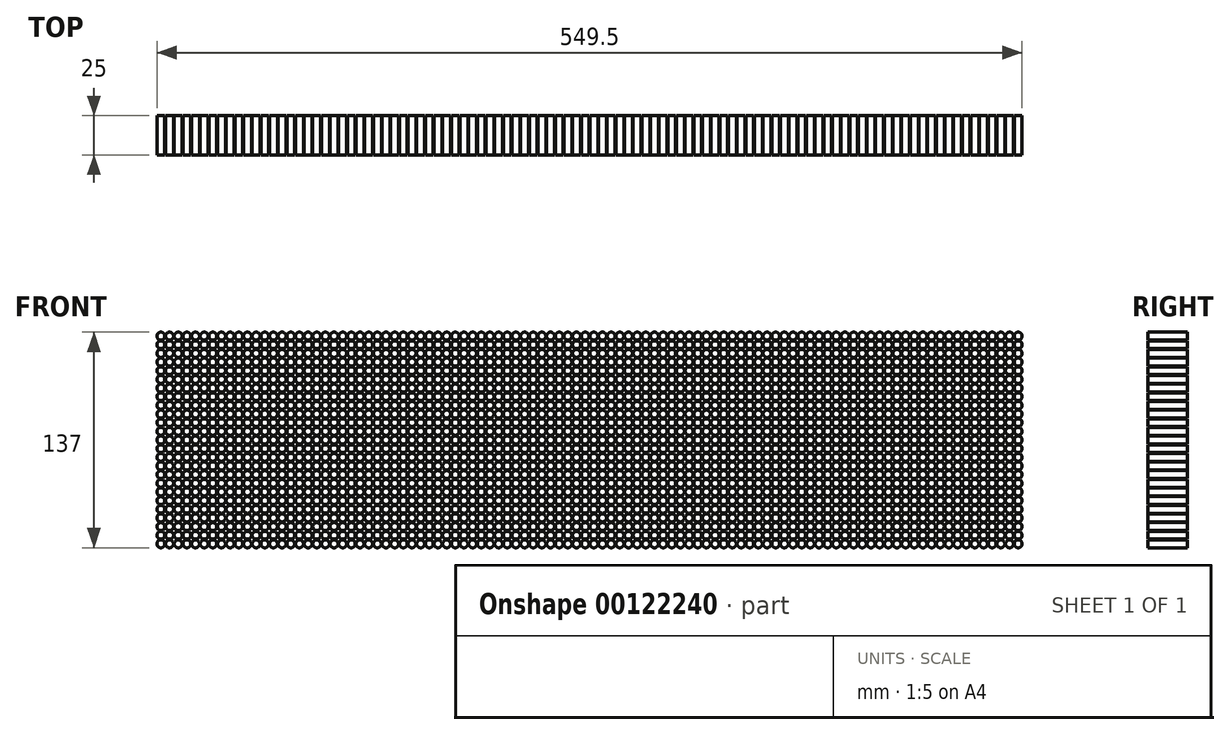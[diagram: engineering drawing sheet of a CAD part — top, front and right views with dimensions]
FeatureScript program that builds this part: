
annotation { "Feature Type Name" : "Feature", "Feature Type Description" : "" }
export const myFeature = defineFeature(function(context is Context, id is Id, definition is map)
    precondition{}
    {
        {
            var Q0;
            Q0=qCreatedBy(makeId("Front.planeOp"),FACE);
            var sketch = newSketch(context, id + "F0", { "sketchPlane" : qUnion([Q0])});
            skCircle(sketch, "E0", {"center": v(0, 0) * mm, "radius": 2.5 * mm});
            skCircle(sketch, "E1.0.1.0", {"center": v(0, -5.5) * mm, "radius": 2.5 * mm});
            skCircle(sketch, "E1.0.2.0", {"center": v(0, -11) * mm, "radius": 2.5 * mm});
            skCircle(sketch, "E1.0.3.0", {"center": v(0, -16.5) * mm, "radius": 2.5 * mm});
            skCircle(sketch, "E1.0.4.0", {"center": v(0, -22) * mm, "radius": 2.5 * mm});
            skCircle(sketch, "E1.0.5.0", {"center": v(0, -27.5) * mm, "radius": 2.5 * mm});
            skCircle(sketch, "E1.0.6.0", {"center": v(0, -33) * mm, "radius": 2.5 * mm});
            skCircle(sketch, "E1.0.7.0", {"center": v(0, -38.5) * mm, "radius": 2.5 * mm});
            skCircle(sketch, "E1.0.8.0", {"center": v(0, -44) * mm, "radius": 2.5 * mm});
            skCircle(sketch, "E1.0.9.0", {"center": v(0, -49.5) * mm, "radius": 2.5 * mm});
            skCircle(sketch, "E1.0.10.0", {"center": v(0, -55) * mm, "radius": 2.5 * mm});
            skCircle(sketch, "E1.0.11.0", {"center": v(0, -60.5) * mm, "radius": 2.5 * mm});
            skCircle(sketch, "E1.0.12.0", {"center": v(0, -66) * mm, "radius": 2.5 * mm});
            skCircle(sketch, "E1.0.13.0", {"center": v(0, -71.5) * mm, "radius": 2.5 * mm});
            skCircle(sketch, "E1.0.14.0", {"center": v(0, -77) * mm, "radius": 2.5 * mm});
            skCircle(sketch, "E1.0.15.0", {"center": v(0, -82.5) * mm, "radius": 2.5 * mm});
            skCircle(sketch, "E1.0.16.0", {"center": v(0, -88) * mm, "radius": 2.5 * mm});
            skCircle(sketch, "E1.0.17.0", {"center": v(0, -93.5) * mm, "radius": 2.5 * mm});
            skCircle(sketch, "E1.0.18.0", {"center": v(0, -99) * mm, "radius": 2.5 * mm});
            skCircle(sketch, "E1.0.19.0", {"center": v(0, -104.5) * mm, "radius": 2.5 * mm});
            skCircle(sketch, "E1.0.20.0", {"center": v(0, -110) * mm, "radius": 2.5 * mm});
            skCircle(sketch, "E1.0.21.0", {"center": v(0, -115.5) * mm, "radius": 2.5 * mm});
            skCircle(sketch, "E1.0.22.0", {"center": v(0, -121) * mm, "radius": 2.5 * mm});
            skCircle(sketch, "E1.0.23.0", {"center": v(0, -126.5) * mm, "radius": 2.5 * mm});
            skCircle(sketch, "E1.0.24.0", {"center": v(0, -132) * mm, "radius": 2.5 * mm});
            skCircle(sketch, "E1.1.0.0", {"center": v(5.5, 0) * mm, "radius": 2.5 * mm});
            skCircle(sketch, "E1.1.1.0", {"center": v(5.5, -5.5) * mm, "radius": 2.5 * mm});
            skCircle(sketch, "E1.1.2.0", {"center": v(5.5, -11) * mm, "radius": 2.5 * mm});
            skCircle(sketch, "E1.1.3.0", {"center": v(5.5, -16.5) * mm, "radius": 2.5 * mm});
            skCircle(sketch, "E1.1.4.0", {"center": v(5.5, -22) * mm, "radius": 2.5 * mm});
            skCircle(sketch, "E1.1.5.0", {"center": v(5.5, -27.5) * mm, "radius": 2.5 * mm});
            skCircle(sketch, "E1.1.6.0", {"center": v(5.5, -33) * mm, "radius": 2.5 * mm});
            skCircle(sketch, "E1.1.7.0", {"center": v(5.5, -38.5) * mm, "radius": 2.5 * mm});
            skCircle(sketch, "E1.1.8.0", {"center": v(5.5, -44) * mm, "radius": 2.5 * mm});
            skCircle(sketch, "E1.1.9.0", {"center": v(5.5, -49.5) * mm, "radius": 2.5 * mm});
            skCircle(sketch, "E1.1.10.0", {"center": v(5.5, -55) * mm, "radius": 2.5 * mm});
            skCircle(sketch, "E1.1.11.0", {"center": v(5.5, -60.5) * mm, "radius": 2.5 * mm});
            skCircle(sketch, "E1.1.12.0", {"center": v(5.5, -66) * mm, "radius": 2.5 * mm});
            skCircle(sketch, "E1.1.13.0", {"center": v(5.5, -71.5) * mm, "radius": 2.5 * mm});
            skCircle(sketch, "E1.1.14.0", {"center": v(5.5, -77) * mm, "radius": 2.5 * mm});
            skCircle(sketch, "E1.1.15.0", {"center": v(5.5, -82.5) * mm, "radius": 2.5 * mm});
            skCircle(sketch, "E1.1.16.0", {"center": v(5.5, -88) * mm, "radius": 2.5 * mm});
            skCircle(sketch, "E1.1.17.0", {"center": v(5.5, -93.5) * mm, "radius": 2.5 * mm});
            skCircle(sketch, "E1.1.18.0", {"center": v(5.5, -99) * mm, "radius": 2.5 * mm});
            skCircle(sketch, "E1.1.19.0", {"center": v(5.5, -104.5) * mm, "radius": 2.5 * mm});
            skCircle(sketch, "E1.1.20.0", {"center": v(5.5, -110) * mm, "radius": 2.5 * mm});
            skCircle(sketch, "E1.1.21.0", {"center": v(5.5, -115.5) * mm, "radius": 2.5 * mm});
            skCircle(sketch, "E1.1.22.0", {"center": v(5.5, -121) * mm, "radius": 2.5 * mm});
            skCircle(sketch, "E1.1.23.0", {"center": v(5.5, -126.5) * mm, "radius": 2.5 * mm});
            skCircle(sketch, "E1.1.24.0", {"center": v(5.5, -132) * mm, "radius": 2.5 * mm});
            skCircle(sketch, "E1.2.0.0", {"center": v(11, 0) * mm, "radius": 2.5 * mm});
            skCircle(sketch, "E1.2.1.0", {"center": v(11, -5.5) * mm, "radius": 2.5 * mm});
            skCircle(sketch, "E1.2.2.0", {"center": v(11, -11) * mm, "radius": 2.5 * mm});
            skCircle(sketch, "E1.2.3.0", {"center": v(11, -16.5) * mm, "radius": 2.5 * mm});
            skCircle(sketch, "E1.2.4.0", {"center": v(11, -22) * mm, "radius": 2.5 * mm});
            skCircle(sketch, "E1.2.5.0", {"center": v(11, -27.5) * mm, "radius": 2.5 * mm});
            skCircle(sketch, "E1.2.6.0", {"center": v(11, -33) * mm, "radius": 2.5 * mm});
            skCircle(sketch, "E1.2.7.0", {"center": v(11, -38.5) * mm, "radius": 2.5 * mm});
            skCircle(sketch, "E1.2.8.0", {"center": v(11, -44) * mm, "radius": 2.5 * mm});
            skCircle(sketch, "E1.2.9.0", {"center": v(11, -49.5) * mm, "radius": 2.5 * mm});
            skCircle(sketch, "E1.2.10.0", {"center": v(11, -55) * mm, "radius": 2.5 * mm});
            skCircle(sketch, "E1.2.11.0", {"center": v(11, -60.5) * mm, "radius": 2.5 * mm});
            skCircle(sketch, "E1.2.12.0", {"center": v(11, -66) * mm, "radius": 2.5 * mm});
            skCircle(sketch, "E1.2.13.0", {"center": v(11, -71.5) * mm, "radius": 2.5 * mm});
            skCircle(sketch, "E1.2.14.0", {"center": v(11, -77) * mm, "radius": 2.5 * mm});
            skCircle(sketch, "E1.2.15.0", {"center": v(11, -82.5) * mm, "radius": 2.5 * mm});
            skCircle(sketch, "E1.2.16.0", {"center": v(11, -88) * mm, "radius": 2.5 * mm});
            skCircle(sketch, "E1.2.17.0", {"center": v(11, -93.5) * mm, "radius": 2.5 * mm});
            skCircle(sketch, "E1.2.18.0", {"center": v(11, -99) * mm, "radius": 2.5 * mm});
            skCircle(sketch, "E1.2.19.0", {"center": v(11, -104.5) * mm, "radius": 2.5 * mm});
            skCircle(sketch, "E1.2.20.0", {"center": v(11, -110) * mm, "radius": 2.5 * mm});
            skCircle(sketch, "E1.2.21.0", {"center": v(11, -115.5) * mm, "radius": 2.5 * mm});
            skCircle(sketch, "E1.2.22.0", {"center": v(11, -121) * mm, "radius": 2.5 * mm});
            skCircle(sketch, "E1.2.23.0", {"center": v(11, -126.5) * mm, "radius": 2.5 * mm});
            skCircle(sketch, "E1.2.24.0", {"center": v(11, -132) * mm, "radius": 2.5 * mm});
            skCircle(sketch, "E1.3.0.0", {"center": v(16.5, 0) * mm, "radius": 2.5 * mm});
            skCircle(sketch, "E1.3.1.0", {"center": v(16.5, -5.5) * mm, "radius": 2.5 * mm});
            skCircle(sketch, "E1.3.2.0", {"center": v(16.5, -11) * mm, "radius": 2.5 * mm});
            skCircle(sketch, "E1.3.3.0", {"center": v(16.5, -16.5) * mm, "radius": 2.5 * mm});
            skCircle(sketch, "E1.3.4.0", {"center": v(16.5, -22) * mm, "radius": 2.5 * mm});
            skCircle(sketch, "E1.3.5.0", {"center": v(16.5, -27.5) * mm, "radius": 2.5 * mm});
            skCircle(sketch, "E1.3.6.0", {"center": v(16.5, -33) * mm, "radius": 2.5 * mm});
            skCircle(sketch, "E1.3.7.0", {"center": v(16.5, -38.5) * mm, "radius": 2.5 * mm});
            skCircle(sketch, "E1.3.8.0", {"center": v(16.5, -44) * mm, "radius": 2.5 * mm});
            skCircle(sketch, "E1.3.9.0", {"center": v(16.5, -49.5) * mm, "radius": 2.5 * mm});
            skCircle(sketch, "E1.3.10.0", {"center": v(16.5, -55) * mm, "radius": 2.5 * mm});
            skCircle(sketch, "E1.3.11.0", {"center": v(16.5, -60.5) * mm, "radius": 2.5 * mm});
            skCircle(sketch, "E1.3.12.0", {"center": v(16.5, -66) * mm, "radius": 2.5 * mm});
            skCircle(sketch, "E1.3.13.0", {"center": v(16.5, -71.5) * mm, "radius": 2.5 * mm});
            skCircle(sketch, "E1.3.14.0", {"center": v(16.5, -77) * mm, "radius": 2.5 * mm});
            skCircle(sketch, "E1.3.15.0", {"center": v(16.5, -82.5) * mm, "radius": 2.5 * mm});
            skCircle(sketch, "E1.3.16.0", {"center": v(16.5, -88) * mm, "radius": 2.5 * mm});
            skCircle(sketch, "E1.3.17.0", {"center": v(16.5, -93.5) * mm, "radius": 2.5 * mm});
            skCircle(sketch, "E1.3.18.0", {"center": v(16.5, -99) * mm, "radius": 2.5 * mm});
            skCircle(sketch, "E1.3.19.0", {"center": v(16.5, -104.5) * mm, "radius": 2.5 * mm});
            skCircle(sketch, "E1.3.20.0", {"center": v(16.5, -110) * mm, "radius": 2.5 * mm});
            skCircle(sketch, "E1.3.21.0", {"center": v(16.5, -115.5) * mm, "radius": 2.5 * mm});
            skCircle(sketch, "E1.3.22.0", {"center": v(16.5, -121) * mm, "radius": 2.5 * mm});
            skCircle(sketch, "E1.3.23.0", {"center": v(16.5, -126.5) * mm, "radius": 2.5 * mm});
            skCircle(sketch, "E1.3.24.0", {"center": v(16.5, -132) * mm, "radius": 2.5 * mm});
            skCircle(sketch, "E1.4.0.0", {"center": v(22, 0) * mm, "radius": 2.5 * mm});
            skCircle(sketch, "E1.4.1.0", {"center": v(22, -5.5) * mm, "radius": 2.5 * mm});
            skCircle(sketch, "E1.4.2.0", {"center": v(22, -11) * mm, "radius": 2.5 * mm});
            skCircle(sketch, "E1.4.3.0", {"center": v(22, -16.5) * mm, "radius": 2.5 * mm});
            skCircle(sketch, "E1.4.4.0", {"center": v(22, -22) * mm, "radius": 2.5 * mm});
            skCircle(sketch, "E1.4.5.0", {"center": v(22, -27.5) * mm, "radius": 2.5 * mm});
            skCircle(sketch, "E1.4.6.0", {"center": v(22, -33) * mm, "radius": 2.5 * mm});
            skCircle(sketch, "E1.4.7.0", {"center": v(22, -38.5) * mm, "radius": 2.5 * mm});
            skCircle(sketch, "E1.4.8.0", {"center": v(22, -44) * mm, "radius": 2.5 * mm});
            skCircle(sketch, "E1.4.9.0", {"center": v(22, -49.5) * mm, "radius": 2.5 * mm});
            skCircle(sketch, "E1.4.10.0", {"center": v(22, -55) * mm, "radius": 2.5 * mm});
            skCircle(sketch, "E1.4.11.0", {"center": v(22, -60.5) * mm, "radius": 2.5 * mm});
            skCircle(sketch, "E1.4.12.0", {"center": v(22, -66) * mm, "radius": 2.5 * mm});
            skCircle(sketch, "E1.4.13.0", {"center": v(22, -71.5) * mm, "radius": 2.5 * mm});
            skCircle(sketch, "E1.4.14.0", {"center": v(22, -77) * mm, "radius": 2.5 * mm});
            skCircle(sketch, "E1.4.15.0", {"center": v(22, -82.5) * mm, "radius": 2.5 * mm});
            skCircle(sketch, "E1.4.16.0", {"center": v(22, -88) * mm, "radius": 2.5 * mm});
            skCircle(sketch, "E1.4.17.0", {"center": v(22, -93.5) * mm, "radius": 2.5 * mm});
            skCircle(sketch, "E1.4.18.0", {"center": v(22, -99) * mm, "radius": 2.5 * mm});
            skCircle(sketch, "E1.4.19.0", {"center": v(22, -104.5) * mm, "radius": 2.5 * mm});
            skCircle(sketch, "E1.4.20.0", {"center": v(22, -110) * mm, "radius": 2.5 * mm});
            skCircle(sketch, "E1.4.21.0", {"center": v(22, -115.5) * mm, "radius": 2.5 * mm});
            skCircle(sketch, "E1.4.22.0", {"center": v(22, -121) * mm, "radius": 2.5 * mm});
            skCircle(sketch, "E1.4.23.0", {"center": v(22, -126.5) * mm, "radius": 2.5 * mm});
            skCircle(sketch, "E1.4.24.0", {"center": v(22, -132) * mm, "radius": 2.5 * mm});
            skCircle(sketch, "E1.5.0.0", {"center": v(27.5, 0) * mm, "radius": 2.5 * mm});
            skCircle(sketch, "E1.5.1.0", {"center": v(27.5, -5.5) * mm, "radius": 2.5 * mm});
            skCircle(sketch, "E1.5.2.0", {"center": v(27.5, -11) * mm, "radius": 2.5 * mm});
            skCircle(sketch, "E1.5.3.0", {"center": v(27.5, -16.5) * mm, "radius": 2.5 * mm});
            skCircle(sketch, "E1.5.4.0", {"center": v(27.5, -22) * mm, "radius": 2.5 * mm});
            skCircle(sketch, "E1.5.5.0", {"center": v(27.5, -27.5) * mm, "radius": 2.5 * mm});
            skCircle(sketch, "E1.5.6.0", {"center": v(27.5, -33) * mm, "radius": 2.5 * mm});
            skCircle(sketch, "E1.5.7.0", {"center": v(27.5, -38.5) * mm, "radius": 2.5 * mm});
            skCircle(sketch, "E1.5.8.0", {"center": v(27.5, -44) * mm, "radius": 2.5 * mm});
            skCircle(sketch, "E1.5.9.0", {"center": v(27.5, -49.5) * mm, "radius": 2.5 * mm});
            skCircle(sketch, "E1.5.10.0", {"center": v(27.5, -55) * mm, "radius": 2.5 * mm});
            skCircle(sketch, "E1.5.11.0", {"center": v(27.5, -60.5) * mm, "radius": 2.5 * mm});
            skCircle(sketch, "E1.5.12.0", {"center": v(27.5, -66) * mm, "radius": 2.5 * mm});
            skCircle(sketch, "E1.5.13.0", {"center": v(27.5, -71.5) * mm, "radius": 2.5 * mm});
            skCircle(sketch, "E1.5.14.0", {"center": v(27.5, -77) * mm, "radius": 2.5 * mm});
            skCircle(sketch, "E1.5.15.0", {"center": v(27.5, -82.5) * mm, "radius": 2.5 * mm});
            skCircle(sketch, "E1.5.16.0", {"center": v(27.5, -88) * mm, "radius": 2.5 * mm});
            skCircle(sketch, "E1.5.17.0", {"center": v(27.5, -93.5) * mm, "radius": 2.5 * mm});
            skCircle(sketch, "E1.5.18.0", {"center": v(27.5, -99) * mm, "radius": 2.5 * mm});
            skCircle(sketch, "E1.5.19.0", {"center": v(27.5, -104.5) * mm, "radius": 2.5 * mm});
            skCircle(sketch, "E1.5.20.0", {"center": v(27.5, -110) * mm, "radius": 2.5 * mm});
            skCircle(sketch, "E1.5.21.0", {"center": v(27.5, -115.5) * mm, "radius": 2.5 * mm});
            skCircle(sketch, "E1.5.22.0", {"center": v(27.5, -121) * mm, "radius": 2.5 * mm});
            skCircle(sketch, "E1.5.23.0", {"center": v(27.5, -126.5) * mm, "radius": 2.5 * mm});
            skCircle(sketch, "E1.5.24.0", {"center": v(27.5, -132) * mm, "radius": 2.5 * mm});
            skCircle(sketch, "E1.6.0.0", {"center": v(33, 0) * mm, "radius": 2.5 * mm});
            skCircle(sketch, "E1.6.1.0", {"center": v(33, -5.5) * mm, "radius": 2.5 * mm});
            skCircle(sketch, "E1.6.2.0", {"center": v(33, -11) * mm, "radius": 2.5 * mm});
            skCircle(sketch, "E1.6.3.0", {"center": v(33, -16.5) * mm, "radius": 2.5 * mm});
            skCircle(sketch, "E1.6.4.0", {"center": v(33, -22) * mm, "radius": 2.5 * mm});
            skCircle(sketch, "E1.6.5.0", {"center": v(33, -27.5) * mm, "radius": 2.5 * mm});
            skCircle(sketch, "E1.6.6.0", {"center": v(33, -33) * mm, "radius": 2.5 * mm});
            skCircle(sketch, "E1.6.7.0", {"center": v(33, -38.5) * mm, "radius": 2.5 * mm});
            skCircle(sketch, "E1.6.8.0", {"center": v(33, -44) * mm, "radius": 2.5 * mm});
            skCircle(sketch, "E1.6.9.0", {"center": v(33, -49.5) * mm, "radius": 2.5 * mm});
            skCircle(sketch, "E1.6.10.0", {"center": v(33, -55) * mm, "radius": 2.5 * mm});
            skCircle(sketch, "E1.6.11.0", {"center": v(33, -60.5) * mm, "radius": 2.5 * mm});
            skCircle(sketch, "E1.6.12.0", {"center": v(33, -66) * mm, "radius": 2.5 * mm});
            skCircle(sketch, "E1.6.13.0", {"center": v(33, -71.5) * mm, "radius": 2.5 * mm});
            skCircle(sketch, "E1.6.14.0", {"center": v(33, -77) * mm, "radius": 2.5 * mm});
            skCircle(sketch, "E1.6.15.0", {"center": v(33, -82.5) * mm, "radius": 2.5 * mm});
            skCircle(sketch, "E1.6.16.0", {"center": v(33, -88) * mm, "radius": 2.5 * mm});
            skCircle(sketch, "E1.6.17.0", {"center": v(33, -93.5) * mm, "radius": 2.5 * mm});
            skCircle(sketch, "E1.6.18.0", {"center": v(33, -99) * mm, "radius": 2.5 * mm});
            skCircle(sketch, "E1.6.19.0", {"center": v(33, -104.5) * mm, "radius": 2.5 * mm});
            skCircle(sketch, "E1.6.20.0", {"center": v(33, -110) * mm, "radius": 2.5 * mm});
            skCircle(sketch, "E1.6.21.0", {"center": v(33, -115.5) * mm, "radius": 2.5 * mm});
            skCircle(sketch, "E1.6.22.0", {"center": v(33, -121) * mm, "radius": 2.5 * mm});
            skCircle(sketch, "E1.6.23.0", {"center": v(33, -126.5) * mm, "radius": 2.5 * mm});
            skCircle(sketch, "E1.6.24.0", {"center": v(33, -132) * mm, "radius": 2.5 * mm});
            skCircle(sketch, "E1.7.0.0", {"center": v(38.5, 0) * mm, "radius": 2.5 * mm});
            skCircle(sketch, "E1.7.1.0", {"center": v(38.5, -5.5) * mm, "radius": 2.5 * mm});
            skCircle(sketch, "E1.7.2.0", {"center": v(38.5, -11) * mm, "radius": 2.5 * mm});
            skCircle(sketch, "E1.7.3.0", {"center": v(38.5, -16.5) * mm, "radius": 2.5 * mm});
            skCircle(sketch, "E1.7.4.0", {"center": v(38.5, -22) * mm, "radius": 2.5 * mm});
            skCircle(sketch, "E1.7.5.0", {"center": v(38.5, -27.5) * mm, "radius": 2.5 * mm});
            skCircle(sketch, "E1.7.6.0", {"center": v(38.5, -33) * mm, "radius": 2.5 * mm});
            skCircle(sketch, "E1.7.7.0", {"center": v(38.5, -38.5) * mm, "radius": 2.5 * mm});
            skCircle(sketch, "E1.7.8.0", {"center": v(38.5, -44) * mm, "radius": 2.5 * mm});
            skCircle(sketch, "E1.7.9.0", {"center": v(38.5, -49.5) * mm, "radius": 2.5 * mm});
            skCircle(sketch, "E1.7.10.0", {"center": v(38.5, -55) * mm, "radius": 2.5 * mm});
            skCircle(sketch, "E1.7.11.0", {"center": v(38.5, -60.5) * mm, "radius": 2.5 * mm});
            skCircle(sketch, "E1.7.12.0", {"center": v(38.5, -66) * mm, "radius": 2.5 * mm});
            skCircle(sketch, "E1.7.13.0", {"center": v(38.5, -71.5) * mm, "radius": 2.5 * mm});
            skCircle(sketch, "E1.7.14.0", {"center": v(38.5, -77) * mm, "radius": 2.5 * mm});
            skCircle(sketch, "E1.7.15.0", {"center": v(38.5, -82.5) * mm, "radius": 2.5 * mm});
            skCircle(sketch, "E1.7.16.0", {"center": v(38.5, -88) * mm, "radius": 2.5 * mm});
            skCircle(sketch, "E1.7.17.0", {"center": v(38.5, -93.5) * mm, "radius": 2.5 * mm});
            skCircle(sketch, "E1.7.18.0", {"center": v(38.5, -99) * mm, "radius": 2.5 * mm});
            skCircle(sketch, "E1.7.19.0", {"center": v(38.5, -104.5) * mm, "radius": 2.5 * mm});
            skCircle(sketch, "E1.7.20.0", {"center": v(38.5, -110) * mm, "radius": 2.5 * mm});
            skCircle(sketch, "E1.7.21.0", {"center": v(38.5, -115.5) * mm, "radius": 2.5 * mm});
            skCircle(sketch, "E1.7.22.0", {"center": v(38.5, -121) * mm, "radius": 2.5 * mm});
            skCircle(sketch, "E1.7.23.0", {"center": v(38.5, -126.5) * mm, "radius": 2.5 * mm});
            skCircle(sketch, "E1.7.24.0", {"center": v(38.5, -132) * mm, "radius": 2.5 * mm});
            skCircle(sketch, "E1.8.0.0", {"center": v(44, 0) * mm, "radius": 2.5 * mm});
            skCircle(sketch, "E1.8.1.0", {"center": v(44, -5.5) * mm, "radius": 2.5 * mm});
            skCircle(sketch, "E1.8.2.0", {"center": v(44, -11) * mm, "radius": 2.5 * mm});
            skCircle(sketch, "E1.8.3.0", {"center": v(44, -16.5) * mm, "radius": 2.5 * mm});
            skCircle(sketch, "E1.8.4.0", {"center": v(44, -22) * mm, "radius": 2.5 * mm});
            skCircle(sketch, "E1.8.5.0", {"center": v(44, -27.5) * mm, "radius": 2.5 * mm});
            skCircle(sketch, "E1.8.6.0", {"center": v(44, -33) * mm, "radius": 2.5 * mm});
            skCircle(sketch, "E1.8.7.0", {"center": v(44, -38.5) * mm, "radius": 2.5 * mm});
            skCircle(sketch, "E1.8.8.0", {"center": v(44, -44) * mm, "radius": 2.5 * mm});
            skCircle(sketch, "E1.8.9.0", {"center": v(44, -49.5) * mm, "radius": 2.5 * mm});
            skCircle(sketch, "E1.8.10.0", {"center": v(44, -55) * mm, "radius": 2.5 * mm});
            skCircle(sketch, "E1.8.11.0", {"center": v(44, -60.5) * mm, "radius": 2.5 * mm});
            skCircle(sketch, "E1.8.12.0", {"center": v(44, -66) * mm, "radius": 2.5 * mm});
            skCircle(sketch, "E1.8.13.0", {"center": v(44, -71.5) * mm, "radius": 2.5 * mm});
            skCircle(sketch, "E1.8.14.0", {"center": v(44, -77) * mm, "radius": 2.5 * mm});
            skCircle(sketch, "E1.8.15.0", {"center": v(44, -82.5) * mm, "radius": 2.5 * mm});
            skCircle(sketch, "E1.8.16.0", {"center": v(44, -88) * mm, "radius": 2.5 * mm});
            skCircle(sketch, "E1.8.17.0", {"center": v(44, -93.5) * mm, "radius": 2.5 * mm});
            skCircle(sketch, "E1.8.18.0", {"center": v(44, -99) * mm, "radius": 2.5 * mm});
            skCircle(sketch, "E1.8.19.0", {"center": v(44, -104.5) * mm, "radius": 2.5 * mm});
            skCircle(sketch, "E1.8.20.0", {"center": v(44, -110) * mm, "radius": 2.5 * mm});
            skCircle(sketch, "E1.8.21.0", {"center": v(44, -115.5) * mm, "radius": 2.5 * mm});
            skCircle(sketch, "E1.8.22.0", {"center": v(44, -121) * mm, "radius": 2.5 * mm});
            skCircle(sketch, "E1.8.23.0", {"center": v(44, -126.5) * mm, "radius": 2.5 * mm});
            skCircle(sketch, "E1.8.24.0", {"center": v(44, -132) * mm, "radius": 2.5 * mm});
            skCircle(sketch, "E1.9.0.0", {"center": v(49.5, 0) * mm, "radius": 2.5 * mm});
            skCircle(sketch, "E1.9.1.0", {"center": v(49.5, -5.5) * mm, "radius": 2.5 * mm});
            skCircle(sketch, "E1.9.2.0", {"center": v(49.5, -11) * mm, "radius": 2.5 * mm});
            skCircle(sketch, "E1.9.3.0", {"center": v(49.5, -16.5) * mm, "radius": 2.5 * mm});
            skCircle(sketch, "E1.9.4.0", {"center": v(49.5, -22) * mm, "radius": 2.5 * mm});
            skCircle(sketch, "E1.9.5.0", {"center": v(49.5, -27.5) * mm, "radius": 2.5 * mm});
            skCircle(sketch, "E1.9.6.0", {"center": v(49.5, -33) * mm, "radius": 2.5 * mm});
            skCircle(sketch, "E1.9.7.0", {"center": v(49.5, -38.5) * mm, "radius": 2.5 * mm});
            skCircle(sketch, "E1.9.8.0", {"center": v(49.5, -44) * mm, "radius": 2.5 * mm});
            skCircle(sketch, "E1.9.9.0", {"center": v(49.5, -49.5) * mm, "radius": 2.5 * mm});
            skCircle(sketch, "E1.9.10.0", {"center": v(49.5, -55) * mm, "radius": 2.5 * mm});
            skCircle(sketch, "E1.9.11.0", {"center": v(49.5, -60.5) * mm, "radius": 2.5 * mm});
            skCircle(sketch, "E1.9.12.0", {"center": v(49.5, -66) * mm, "radius": 2.5 * mm});
            skCircle(sketch, "E1.9.13.0", {"center": v(49.5, -71.5) * mm, "radius": 2.5 * mm});
            skCircle(sketch, "E1.9.14.0", {"center": v(49.5, -77) * mm, "radius": 2.5 * mm});
            skCircle(sketch, "E1.9.15.0", {"center": v(49.5, -82.5) * mm, "radius": 2.5 * mm});
            skCircle(sketch, "E1.9.16.0", {"center": v(49.5, -88) * mm, "radius": 2.5 * mm});
            skCircle(sketch, "E1.9.17.0", {"center": v(49.5, -93.5) * mm, "radius": 2.5 * mm});
            skCircle(sketch, "E1.9.18.0", {"center": v(49.5, -99) * mm, "radius": 2.5 * mm});
            skCircle(sketch, "E1.9.19.0", {"center": v(49.5, -104.5) * mm, "radius": 2.5 * mm});
            skCircle(sketch, "E1.9.20.0", {"center": v(49.5, -110) * mm, "radius": 2.5 * mm});
            skCircle(sketch, "E1.9.21.0", {"center": v(49.5, -115.5) * mm, "radius": 2.5 * mm});
            skCircle(sketch, "E1.9.22.0", {"center": v(49.5, -121) * mm, "radius": 2.5 * mm});
            skCircle(sketch, "E1.9.23.0", {"center": v(49.5, -126.5) * mm, "radius": 2.5 * mm});
            skCircle(sketch, "E1.9.24.0", {"center": v(49.5, -132) * mm, "radius": 2.5 * mm});
            skCircle(sketch, "E1.10.0.0", {"center": v(55, 0) * mm, "radius": 2.5 * mm});
            skCircle(sketch, "E1.10.1.0", {"center": v(55, -5.5) * mm, "radius": 2.5 * mm});
            skCircle(sketch, "E1.10.2.0", {"center": v(55, -11) * mm, "radius": 2.5 * mm});
            skCircle(sketch, "E1.10.3.0", {"center": v(55, -16.5) * mm, "radius": 2.5 * mm});
            skCircle(sketch, "E1.10.4.0", {"center": v(55, -22) * mm, "radius": 2.5 * mm});
            skCircle(sketch, "E1.10.5.0", {"center": v(55, -27.5) * mm, "radius": 2.5 * mm});
            skCircle(sketch, "E1.10.6.0", {"center": v(55, -33) * mm, "radius": 2.5 * mm});
            skCircle(sketch, "E1.10.7.0", {"center": v(55, -38.5) * mm, "radius": 2.5 * mm});
            skCircle(sketch, "E1.10.8.0", {"center": v(55, -44) * mm, "radius": 2.5 * mm});
            skCircle(sketch, "E1.10.9.0", {"center": v(55, -49.5) * mm, "radius": 2.5 * mm});
            skCircle(sketch, "E1.10.10.0", {"center": v(55, -55) * mm, "radius": 2.5 * mm});
            skCircle(sketch, "E1.10.11.0", {"center": v(55, -60.5) * mm, "radius": 2.5 * mm});
            skCircle(sketch, "E1.10.12.0", {"center": v(55, -66) * mm, "radius": 2.5 * mm});
            skCircle(sketch, "E1.10.13.0", {"center": v(55, -71.5) * mm, "radius": 2.5 * mm});
            skCircle(sketch, "E1.10.14.0", {"center": v(55, -77) * mm, "radius": 2.5 * mm});
            skCircle(sketch, "E1.10.15.0", {"center": v(55, -82.5) * mm, "radius": 2.5 * mm});
            skCircle(sketch, "E1.10.16.0", {"center": v(55, -88) * mm, "radius": 2.5 * mm});
            skCircle(sketch, "E1.10.17.0", {"center": v(55, -93.5) * mm, "radius": 2.5 * mm});
            skCircle(sketch, "E1.10.18.0", {"center": v(55, -99) * mm, "radius": 2.5 * mm});
            skCircle(sketch, "E1.10.19.0", {"center": v(55, -104.5) * mm, "radius": 2.5 * mm});
            skCircle(sketch, "E1.10.20.0", {"center": v(55, -110) * mm, "radius": 2.5 * mm});
            skCircle(sketch, "E1.10.21.0", {"center": v(55, -115.5) * mm, "radius": 2.5 * mm});
            skCircle(sketch, "E1.10.22.0", {"center": v(55, -121) * mm, "radius": 2.5 * mm});
            skCircle(sketch, "E1.10.23.0", {"center": v(55, -126.5) * mm, "radius": 2.5 * mm});
            skCircle(sketch, "E1.10.24.0", {"center": v(55, -132) * mm, "radius": 2.5 * mm});
            skCircle(sketch, "E1.11.0.0", {"center": v(60.5, 0) * mm, "radius": 2.5 * mm});
            skCircle(sketch, "E1.11.1.0", {"center": v(60.5, -5.5) * mm, "radius": 2.5 * mm});
            skCircle(sketch, "E1.11.2.0", {"center": v(60.5, -11) * mm, "radius": 2.5 * mm});
            skCircle(sketch, "E1.11.3.0", {"center": v(60.5, -16.5) * mm, "radius": 2.5 * mm});
            skCircle(sketch, "E1.11.4.0", {"center": v(60.5, -22) * mm, "radius": 2.5 * mm});
            skCircle(sketch, "E1.11.5.0", {"center": v(60.5, -27.5) * mm, "radius": 2.5 * mm});
            skCircle(sketch, "E1.11.6.0", {"center": v(60.5, -33) * mm, "radius": 2.5 * mm});
            skCircle(sketch, "E1.11.7.0", {"center": v(60.5, -38.5) * mm, "radius": 2.5 * mm});
            skCircle(sketch, "E1.11.8.0", {"center": v(60.5, -44) * mm, "radius": 2.5 * mm});
            skCircle(sketch, "E1.11.9.0", {"center": v(60.5, -49.5) * mm, "radius": 2.5 * mm});
            skCircle(sketch, "E1.11.10.0", {"center": v(60.5, -55) * mm, "radius": 2.5 * mm});
            skCircle(sketch, "E1.11.11.0", {"center": v(60.5, -60.5) * mm, "radius": 2.5 * mm});
            skCircle(sketch, "E1.11.12.0", {"center": v(60.5, -66) * mm, "radius": 2.5 * mm});
            skCircle(sketch, "E1.11.13.0", {"center": v(60.5, -71.5) * mm, "radius": 2.5 * mm});
            skCircle(sketch, "E1.11.14.0", {"center": v(60.5, -77) * mm, "radius": 2.5 * mm});
            skCircle(sketch, "E1.11.15.0", {"center": v(60.5, -82.5) * mm, "radius": 2.5 * mm});
            skCircle(sketch, "E1.11.16.0", {"center": v(60.5, -88) * mm, "radius": 2.5 * mm});
            skCircle(sketch, "E1.11.17.0", {"center": v(60.5, -93.5) * mm, "radius": 2.5 * mm});
            skCircle(sketch, "E1.11.18.0", {"center": v(60.5, -99) * mm, "radius": 2.5 * mm});
            skCircle(sketch, "E1.11.19.0", {"center": v(60.5, -104.5) * mm, "radius": 2.5 * mm});
            skCircle(sketch, "E1.11.20.0", {"center": v(60.5, -110) * mm, "radius": 2.5 * mm});
            skCircle(sketch, "E1.11.21.0", {"center": v(60.5, -115.5) * mm, "radius": 2.5 * mm});
            skCircle(sketch, "E1.11.22.0", {"center": v(60.5, -121) * mm, "radius": 2.5 * mm});
            skCircle(sketch, "E1.11.23.0", {"center": v(60.5, -126.5) * mm, "radius": 2.5 * mm});
            skCircle(sketch, "E1.11.24.0", {"center": v(60.5, -132) * mm, "radius": 2.5 * mm});
            skCircle(sketch, "E1.12.0.0", {"center": v(66, 0) * mm, "radius": 2.5 * mm});
            skCircle(sketch, "E1.12.1.0", {"center": v(66, -5.5) * mm, "radius": 2.5 * mm});
            skCircle(sketch, "E1.12.2.0", {"center": v(66, -11) * mm, "radius": 2.5 * mm});
            skCircle(sketch, "E1.12.3.0", {"center": v(66, -16.5) * mm, "radius": 2.5 * mm});
            skCircle(sketch, "E1.12.4.0", {"center": v(66, -22) * mm, "radius": 2.5 * mm});
            skCircle(sketch, "E1.12.5.0", {"center": v(66, -27.5) * mm, "radius": 2.5 * mm});
            skCircle(sketch, "E1.12.6.0", {"center": v(66, -33) * mm, "radius": 2.5 * mm});
            skCircle(sketch, "E1.12.7.0", {"center": v(66, -38.5) * mm, "radius": 2.5 * mm});
            skCircle(sketch, "E1.12.8.0", {"center": v(66, -44) * mm, "radius": 2.5 * mm});
            skCircle(sketch, "E1.12.9.0", {"center": v(66, -49.5) * mm, "radius": 2.5 * mm});
            skCircle(sketch, "E1.12.10.0", {"center": v(66, -55) * mm, "radius": 2.5 * mm});
            skCircle(sketch, "E1.12.11.0", {"center": v(66, -60.5) * mm, "radius": 2.5 * mm});
            skCircle(sketch, "E1.12.12.0", {"center": v(66, -66) * mm, "radius": 2.5 * mm});
            skCircle(sketch, "E1.12.13.0", {"center": v(66, -71.5) * mm, "radius": 2.5 * mm});
            skCircle(sketch, "E1.12.14.0", {"center": v(66, -77) * mm, "radius": 2.5 * mm});
            skCircle(sketch, "E1.12.15.0", {"center": v(66, -82.5) * mm, "radius": 2.5 * mm});
            skCircle(sketch, "E1.12.16.0", {"center": v(66, -88) * mm, "radius": 2.5 * mm});
            skCircle(sketch, "E1.12.17.0", {"center": v(66, -93.5) * mm, "radius": 2.5 * mm});
            skCircle(sketch, "E1.12.18.0", {"center": v(66, -99) * mm, "radius": 2.5 * mm});
            skCircle(sketch, "E1.12.19.0", {"center": v(66, -104.5) * mm, "radius": 2.5 * mm});
            skCircle(sketch, "E1.12.20.0", {"center": v(66, -110) * mm, "radius": 2.5 * mm});
            skCircle(sketch, "E1.12.21.0", {"center": v(66, -115.5) * mm, "radius": 2.5 * mm});
            skCircle(sketch, "E1.12.22.0", {"center": v(66, -121) * mm, "radius": 2.5 * mm});
            skCircle(sketch, "E1.12.23.0", {"center": v(66, -126.5) * mm, "radius": 2.5 * mm});
            skCircle(sketch, "E1.12.24.0", {"center": v(66, -132) * mm, "radius": 2.5 * mm});
            skCircle(sketch, "E1.13.0.0", {"center": v(71.5, 0) * mm, "radius": 2.5 * mm});
            skCircle(sketch, "E1.13.1.0", {"center": v(71.5, -5.5) * mm, "radius": 2.5 * mm});
            skCircle(sketch, "E1.13.2.0", {"center": v(71.5, -11) * mm, "radius": 2.5 * mm});
            skCircle(sketch, "E1.13.3.0", {"center": v(71.5, -16.5) * mm, "radius": 2.5 * mm});
            skCircle(sketch, "E1.13.4.0", {"center": v(71.5, -22) * mm, "radius": 2.5 * mm});
            skCircle(sketch, "E1.13.5.0", {"center": v(71.5, -27.5) * mm, "radius": 2.5 * mm});
            skCircle(sketch, "E1.13.6.0", {"center": v(71.5, -33) * mm, "radius": 2.5 * mm});
            skCircle(sketch, "E1.13.7.0", {"center": v(71.5, -38.5) * mm, "radius": 2.5 * mm});
            skCircle(sketch, "E1.13.8.0", {"center": v(71.5, -44) * mm, "radius": 2.5 * mm});
            skCircle(sketch, "E1.13.9.0", {"center": v(71.5, -49.5) * mm, "radius": 2.5 * mm});
            skCircle(sketch, "E1.13.10.0", {"center": v(71.5, -55) * mm, "radius": 2.5 * mm});
            skCircle(sketch, "E1.13.11.0", {"center": v(71.5, -60.5) * mm, "radius": 2.5 * mm});
            skCircle(sketch, "E1.13.12.0", {"center": v(71.5, -66) * mm, "radius": 2.5 * mm});
            skCircle(sketch, "E1.13.13.0", {"center": v(71.5, -71.5) * mm, "radius": 2.5 * mm});
            skCircle(sketch, "E1.13.14.0", {"center": v(71.5, -77) * mm, "radius": 2.5 * mm});
            skCircle(sketch, "E1.13.15.0", {"center": v(71.5, -82.5) * mm, "radius": 2.5 * mm});
            skCircle(sketch, "E1.13.16.0", {"center": v(71.5, -88) * mm, "radius": 2.5 * mm});
            skCircle(sketch, "E1.13.17.0", {"center": v(71.5, -93.5) * mm, "radius": 2.5 * mm});
            skCircle(sketch, "E1.13.18.0", {"center": v(71.5, -99) * mm, "radius": 2.5 * mm});
            skCircle(sketch, "E1.13.19.0", {"center": v(71.5, -104.5) * mm, "radius": 2.5 * mm});
            skCircle(sketch, "E1.13.20.0", {"center": v(71.5, -110) * mm, "radius": 2.5 * mm});
            skCircle(sketch, "E1.13.21.0", {"center": v(71.5, -115.5) * mm, "radius": 2.5 * mm});
            skCircle(sketch, "E1.13.22.0", {"center": v(71.5, -121) * mm, "radius": 2.5 * mm});
            skCircle(sketch, "E1.13.23.0", {"center": v(71.5, -126.5) * mm, "radius": 2.5 * mm});
            skCircle(sketch, "E1.13.24.0", {"center": v(71.5, -132) * mm, "radius": 2.5 * mm});
            skCircle(sketch, "E1.14.0.0", {"center": v(77, 0) * mm, "radius": 2.5 * mm});
            skCircle(sketch, "E1.14.1.0", {"center": v(77, -5.5) * mm, "radius": 2.5 * mm});
            skCircle(sketch, "E1.14.2.0", {"center": v(77, -11) * mm, "radius": 2.5 * mm});
            skCircle(sketch, "E1.14.3.0", {"center": v(77, -16.5) * mm, "radius": 2.5 * mm});
            skCircle(sketch, "E1.14.4.0", {"center": v(77, -22) * mm, "radius": 2.5 * mm});
            skCircle(sketch, "E1.14.5.0", {"center": v(77, -27.5) * mm, "radius": 2.5 * mm});
            skCircle(sketch, "E1.14.6.0", {"center": v(77, -33) * mm, "radius": 2.5 * mm});
            skCircle(sketch, "E1.14.7.0", {"center": v(77, -38.5) * mm, "radius": 2.5 * mm});
            skCircle(sketch, "E1.14.8.0", {"center": v(77, -44) * mm, "radius": 2.5 * mm});
            skCircle(sketch, "E1.14.9.0", {"center": v(77, -49.5) * mm, "radius": 2.5 * mm});
            skCircle(sketch, "E1.14.10.0", {"center": v(77, -55) * mm, "radius": 2.5 * mm});
            skCircle(sketch, "E1.14.11.0", {"center": v(77, -60.5) * mm, "radius": 2.5 * mm});
            skCircle(sketch, "E1.14.12.0", {"center": v(77, -66) * mm, "radius": 2.5 * mm});
            skCircle(sketch, "E1.14.13.0", {"center": v(77, -71.5) * mm, "radius": 2.5 * mm});
            skCircle(sketch, "E1.14.14.0", {"center": v(77, -77) * mm, "radius": 2.5 * mm});
            skCircle(sketch, "E1.14.15.0", {"center": v(77, -82.5) * mm, "radius": 2.5 * mm});
            skCircle(sketch, "E1.14.16.0", {"center": v(77, -88) * mm, "radius": 2.5 * mm});
            skCircle(sketch, "E1.14.17.0", {"center": v(77, -93.5) * mm, "radius": 2.5 * mm});
            skCircle(sketch, "E1.14.18.0", {"center": v(77, -99) * mm, "radius": 2.5 * mm});
            skCircle(sketch, "E1.14.19.0", {"center": v(77, -104.5) * mm, "radius": 2.5 * mm});
            skCircle(sketch, "E1.14.20.0", {"center": v(77, -110) * mm, "radius": 2.5 * mm});
            skCircle(sketch, "E1.14.21.0", {"center": v(77, -115.5) * mm, "radius": 2.5 * mm});
            skCircle(sketch, "E1.14.22.0", {"center": v(77, -121) * mm, "radius": 2.5 * mm});
            skCircle(sketch, "E1.14.23.0", {"center": v(77, -126.5) * mm, "radius": 2.5 * mm});
            skCircle(sketch, "E1.14.24.0", {"center": v(77, -132) * mm, "radius": 2.5 * mm});
            skCircle(sketch, "E1.15.0.0", {"center": v(82.5, 0) * mm, "radius": 2.5 * mm});
            skCircle(sketch, "E1.15.1.0", {"center": v(82.5, -5.5) * mm, "radius": 2.5 * mm});
            skCircle(sketch, "E1.15.2.0", {"center": v(82.5, -11) * mm, "radius": 2.5 * mm});
            skCircle(sketch, "E1.15.3.0", {"center": v(82.5, -16.5) * mm, "radius": 2.5 * mm});
            skCircle(sketch, "E1.15.4.0", {"center": v(82.5, -22) * mm, "radius": 2.5 * mm});
            skCircle(sketch, "E1.15.5.0", {"center": v(82.5, -27.5) * mm, "radius": 2.5 * mm});
            skCircle(sketch, "E1.15.6.0", {"center": v(82.5, -33) * mm, "radius": 2.5 * mm});
            skCircle(sketch, "E1.15.7.0", {"center": v(82.5, -38.5) * mm, "radius": 2.5 * mm});
            skCircle(sketch, "E1.15.8.0", {"center": v(82.5, -44) * mm, "radius": 2.5 * mm});
            skCircle(sketch, "E1.15.9.0", {"center": v(82.5, -49.5) * mm, "radius": 2.5 * mm});
            skCircle(sketch, "E1.15.10.0", {"center": v(82.5, -55) * mm, "radius": 2.5 * mm});
            skCircle(sketch, "E1.15.11.0", {"center": v(82.5, -60.5) * mm, "radius": 2.5 * mm});
            skCircle(sketch, "E1.15.12.0", {"center": v(82.5, -66) * mm, "radius": 2.5 * mm});
            skCircle(sketch, "E1.15.13.0", {"center": v(82.5, -71.5) * mm, "radius": 2.5 * mm});
            skCircle(sketch, "E1.15.14.0", {"center": v(82.5, -77) * mm, "radius": 2.5 * mm});
            skCircle(sketch, "E1.15.15.0", {"center": v(82.5, -82.5) * mm, "radius": 2.5 * mm});
            skCircle(sketch, "E1.15.16.0", {"center": v(82.5, -88) * mm, "radius": 2.5 * mm});
            skCircle(sketch, "E1.15.17.0", {"center": v(82.5, -93.5) * mm, "radius": 2.5 * mm});
            skCircle(sketch, "E1.15.18.0", {"center": v(82.5, -99) * mm, "radius": 2.5 * mm});
            skCircle(sketch, "E1.15.19.0", {"center": v(82.5, -104.5) * mm, "radius": 2.5 * mm});
            skCircle(sketch, "E1.15.20.0", {"center": v(82.5, -110) * mm, "radius": 2.5 * mm});
            skCircle(sketch, "E1.15.21.0", {"center": v(82.5, -115.5) * mm, "radius": 2.5 * mm});
            skCircle(sketch, "E1.15.22.0", {"center": v(82.5, -121) * mm, "radius": 2.5 * mm});
            skCircle(sketch, "E1.15.23.0", {"center": v(82.5, -126.5) * mm, "radius": 2.5 * mm});
            skCircle(sketch, "E1.15.24.0", {"center": v(82.5, -132) * mm, "radius": 2.5 * mm});
            skCircle(sketch, "E1.16.0.0", {"center": v(88, 0) * mm, "radius": 2.5 * mm});
            skCircle(sketch, "E1.16.1.0", {"center": v(88, -5.5) * mm, "radius": 2.5 * mm});
            skCircle(sketch, "E1.16.2.0", {"center": v(88, -11) * mm, "radius": 2.5 * mm});
            skCircle(sketch, "E1.16.3.0", {"center": v(88, -16.5) * mm, "radius": 2.5 * mm});
            skCircle(sketch, "E1.16.4.0", {"center": v(88, -22) * mm, "radius": 2.5 * mm});
            skCircle(sketch, "E1.16.5.0", {"center": v(88, -27.5) * mm, "radius": 2.5 * mm});
            skCircle(sketch, "E1.16.6.0", {"center": v(88, -33) * mm, "radius": 2.5 * mm});
            skCircle(sketch, "E1.16.7.0", {"center": v(88, -38.5) * mm, "radius": 2.5 * mm});
            skCircle(sketch, "E1.16.8.0", {"center": v(88, -44) * mm, "radius": 2.5 * mm});
            skCircle(sketch, "E1.16.9.0", {"center": v(88, -49.5) * mm, "radius": 2.5 * mm});
            skCircle(sketch, "E1.16.10.0", {"center": v(88, -55) * mm, "radius": 2.5 * mm});
            skCircle(sketch, "E1.16.11.0", {"center": v(88, -60.5) * mm, "radius": 2.5 * mm});
            skCircle(sketch, "E1.16.12.0", {"center": v(88, -66) * mm, "radius": 2.5 * mm});
            skCircle(sketch, "E1.16.13.0", {"center": v(88, -71.5) * mm, "radius": 2.5 * mm});
            skCircle(sketch, "E1.16.14.0", {"center": v(88, -77) * mm, "radius": 2.5 * mm});
            skCircle(sketch, "E1.16.15.0", {"center": v(88, -82.5) * mm, "radius": 2.5 * mm});
            skCircle(sketch, "E1.16.16.0", {"center": v(88, -88) * mm, "radius": 2.5 * mm});
            skCircle(sketch, "E1.16.17.0", {"center": v(88, -93.5) * mm, "radius": 2.5 * mm});
            skCircle(sketch, "E1.16.18.0", {"center": v(88, -99) * mm, "radius": 2.5 * mm});
            skCircle(sketch, "E1.16.19.0", {"center": v(88, -104.5) * mm, "radius": 2.5 * mm});
            skCircle(sketch, "E1.16.20.0", {"center": v(88, -110) * mm, "radius": 2.5 * mm});
            skCircle(sketch, "E1.16.21.0", {"center": v(88, -115.5) * mm, "radius": 2.5 * mm});
            skCircle(sketch, "E1.16.22.0", {"center": v(88, -121) * mm, "radius": 2.5 * mm});
            skCircle(sketch, "E1.16.23.0", {"center": v(88, -126.5) * mm, "radius": 2.5 * mm});
            skCircle(sketch, "E1.16.24.0", {"center": v(88, -132) * mm, "radius": 2.5 * mm});
            skCircle(sketch, "E1.17.0.0", {"center": v(93.5, 0) * mm, "radius": 2.5 * mm});
            skCircle(sketch, "E1.17.1.0", {"center": v(93.5, -5.5) * mm, "radius": 2.5 * mm});
            skCircle(sketch, "E1.17.2.0", {"center": v(93.5, -11) * mm, "radius": 2.5 * mm});
            skCircle(sketch, "E1.17.3.0", {"center": v(93.5, -16.5) * mm, "radius": 2.5 * mm});
            skCircle(sketch, "E1.17.4.0", {"center": v(93.5, -22) * mm, "radius": 2.5 * mm});
            skCircle(sketch, "E1.17.5.0", {"center": v(93.5, -27.5) * mm, "radius": 2.5 * mm});
            skCircle(sketch, "E1.17.6.0", {"center": v(93.5, -33) * mm, "radius": 2.5 * mm});
            skCircle(sketch, "E1.17.7.0", {"center": v(93.5, -38.5) * mm, "radius": 2.5 * mm});
            skCircle(sketch, "E1.17.8.0", {"center": v(93.5, -44) * mm, "radius": 2.5 * mm});
            skCircle(sketch, "E1.17.9.0", {"center": v(93.5, -49.5) * mm, "radius": 2.5 * mm});
            skCircle(sketch, "E1.17.10.0", {"center": v(93.5, -55) * mm, "radius": 2.5 * mm});
            skCircle(sketch, "E1.17.11.0", {"center": v(93.5, -60.5) * mm, "radius": 2.5 * mm});
            skCircle(sketch, "E1.17.12.0", {"center": v(93.5, -66) * mm, "radius": 2.5 * mm});
            skCircle(sketch, "E1.17.13.0", {"center": v(93.5, -71.5) * mm, "radius": 2.5 * mm});
            skCircle(sketch, "E1.17.14.0", {"center": v(93.5, -77) * mm, "radius": 2.5 * mm});
            skCircle(sketch, "E1.17.15.0", {"center": v(93.5, -82.5) * mm, "radius": 2.5 * mm});
            skCircle(sketch, "E1.17.16.0", {"center": v(93.5, -88) * mm, "radius": 2.5 * mm});
            skCircle(sketch, "E1.17.17.0", {"center": v(93.5, -93.5) * mm, "radius": 2.5 * mm});
            skCircle(sketch, "E1.17.18.0", {"center": v(93.5, -99) * mm, "radius": 2.5 * mm});
            skCircle(sketch, "E1.17.19.0", {"center": v(93.5, -104.5) * mm, "radius": 2.5 * mm});
            skCircle(sketch, "E1.17.20.0", {"center": v(93.5, -110) * mm, "radius": 2.5 * mm});
            skCircle(sketch, "E1.17.21.0", {"center": v(93.5, -115.5) * mm, "radius": 2.5 * mm});
            skCircle(sketch, "E1.17.22.0", {"center": v(93.5, -121) * mm, "radius": 2.5 * mm});
            skCircle(sketch, "E1.17.23.0", {"center": v(93.5, -126.5) * mm, "radius": 2.5 * mm});
            skCircle(sketch, "E1.17.24.0", {"center": v(93.5, -132) * mm, "radius": 2.5 * mm});
            skCircle(sketch, "E1.18.0.0", {"center": v(99, 0) * mm, "radius": 2.5 * mm});
            skCircle(sketch, "E1.18.1.0", {"center": v(99, -5.5) * mm, "radius": 2.5 * mm});
            skCircle(sketch, "E1.18.2.0", {"center": v(99, -11) * mm, "radius": 2.5 * mm});
            skCircle(sketch, "E1.18.3.0", {"center": v(99, -16.5) * mm, "radius": 2.5 * mm});
            skCircle(sketch, "E1.18.4.0", {"center": v(99, -22) * mm, "radius": 2.5 * mm});
            skCircle(sketch, "E1.18.5.0", {"center": v(99, -27.5) * mm, "radius": 2.5 * mm});
            skCircle(sketch, "E1.18.6.0", {"center": v(99, -33) * mm, "radius": 2.5 * mm});
            skCircle(sketch, "E1.18.7.0", {"center": v(99, -38.5) * mm, "radius": 2.5 * mm});
            skCircle(sketch, "E1.18.8.0", {"center": v(99, -44) * mm, "radius": 2.5 * mm});
            skCircle(sketch, "E1.18.9.0", {"center": v(99, -49.5) * mm, "radius": 2.5 * mm});
            skCircle(sketch, "E1.18.10.0", {"center": v(99, -55) * mm, "radius": 2.5 * mm});
            skCircle(sketch, "E1.18.11.0", {"center": v(99, -60.5) * mm, "radius": 2.5 * mm});
            skCircle(sketch, "E1.18.12.0", {"center": v(99, -66) * mm, "radius": 2.5 * mm});
            skCircle(sketch, "E1.18.13.0", {"center": v(99, -71.5) * mm, "radius": 2.5 * mm});
            skCircle(sketch, "E1.18.14.0", {"center": v(99, -77) * mm, "radius": 2.5 * mm});
            skCircle(sketch, "E1.18.15.0", {"center": v(99, -82.5) * mm, "radius": 2.5 * mm});
            skCircle(sketch, "E1.18.16.0", {"center": v(99, -88) * mm, "radius": 2.5 * mm});
            skCircle(sketch, "E1.18.17.0", {"center": v(99, -93.5) * mm, "radius": 2.5 * mm});
            skCircle(sketch, "E1.18.18.0", {"center": v(99, -99) * mm, "radius": 2.5 * mm});
            skCircle(sketch, "E1.18.19.0", {"center": v(99, -104.5) * mm, "radius": 2.5 * mm});
            skCircle(sketch, "E1.18.20.0", {"center": v(99, -110) * mm, "radius": 2.5 * mm});
            skCircle(sketch, "E1.18.21.0", {"center": v(99, -115.5) * mm, "radius": 2.5 * mm});
            skCircle(sketch, "E1.18.22.0", {"center": v(99, -121) * mm, "radius": 2.5 * mm});
            skCircle(sketch, "E1.18.23.0", {"center": v(99, -126.5) * mm, "radius": 2.5 * mm});
            skCircle(sketch, "E1.18.24.0", {"center": v(99, -132) * mm, "radius": 2.5 * mm});
            skCircle(sketch, "E1.19.0.0", {"center": v(104.5, 0) * mm, "radius": 2.5 * mm});
            skCircle(sketch, "E1.19.1.0", {"center": v(104.5, -5.5) * mm, "radius": 2.5 * mm});
            skCircle(sketch, "E1.19.2.0", {"center": v(104.5, -11) * mm, "radius": 2.5 * mm});
            skCircle(sketch, "E1.19.3.0", {"center": v(104.5, -16.5) * mm, "radius": 2.5 * mm});
            skCircle(sketch, "E1.19.4.0", {"center": v(104.5, -22) * mm, "radius": 2.5 * mm});
            skCircle(sketch, "E1.19.5.0", {"center": v(104.5, -27.5) * mm, "radius": 2.5 * mm});
            skCircle(sketch, "E1.19.6.0", {"center": v(104.5, -33) * mm, "radius": 2.5 * mm});
            skCircle(sketch, "E1.19.7.0", {"center": v(104.5, -38.5) * mm, "radius": 2.5 * mm});
            skCircle(sketch, "E1.19.8.0", {"center": v(104.5, -44) * mm, "radius": 2.5 * mm});
            skCircle(sketch, "E1.19.9.0", {"center": v(104.5, -49.5) * mm, "radius": 2.5 * mm});
            skCircle(sketch, "E1.19.10.0", {"center": v(104.5, -55) * mm, "radius": 2.5 * mm});
            skCircle(sketch, "E1.19.11.0", {"center": v(104.5, -60.5) * mm, "radius": 2.5 * mm});
            skCircle(sketch, "E1.19.12.0", {"center": v(104.5, -66) * mm, "radius": 2.5 * mm});
            skCircle(sketch, "E1.19.13.0", {"center": v(104.5, -71.5) * mm, "radius": 2.5 * mm});
            skCircle(sketch, "E1.19.14.0", {"center": v(104.5, -77) * mm, "radius": 2.5 * mm});
            skCircle(sketch, "E1.19.15.0", {"center": v(104.5, -82.5) * mm, "radius": 2.5 * mm});
            skCircle(sketch, "E1.19.16.0", {"center": v(104.5, -88) * mm, "radius": 2.5 * mm});
            skCircle(sketch, "E1.19.17.0", {"center": v(104.5, -93.5) * mm, "radius": 2.5 * mm});
            skCircle(sketch, "E1.19.18.0", {"center": v(104.5, -99) * mm, "radius": 2.5 * mm});
            skCircle(sketch, "E1.19.19.0", {"center": v(104.5, -104.5) * mm, "radius": 2.5 * mm});
            skCircle(sketch, "E1.19.20.0", {"center": v(104.5, -110) * mm, "radius": 2.5 * mm});
            skCircle(sketch, "E1.19.21.0", {"center": v(104.5, -115.5) * mm, "radius": 2.5 * mm});
            skCircle(sketch, "E1.19.22.0", {"center": v(104.5, -121) * mm, "radius": 2.5 * mm});
            skCircle(sketch, "E1.19.23.0", {"center": v(104.5, -126.5) * mm, "radius": 2.5 * mm});
            skCircle(sketch, "E1.19.24.0", {"center": v(104.5, -132) * mm, "radius": 2.5 * mm});
            skCircle(sketch, "E1.20.0.0", {"center": v(110, 0) * mm, "radius": 2.5 * mm});
            skCircle(sketch, "E1.20.1.0", {"center": v(110, -5.5) * mm, "radius": 2.5 * mm});
            skCircle(sketch, "E1.20.2.0", {"center": v(110, -11) * mm, "radius": 2.5 * mm});
            skCircle(sketch, "E1.20.3.0", {"center": v(110, -16.5) * mm, "radius": 2.5 * mm});
            skCircle(sketch, "E1.20.4.0", {"center": v(110, -22) * mm, "radius": 2.5 * mm});
            skCircle(sketch, "E1.20.5.0", {"center": v(110, -27.5) * mm, "radius": 2.5 * mm});
            skCircle(sketch, "E1.20.6.0", {"center": v(110, -33) * mm, "radius": 2.5 * mm});
            skCircle(sketch, "E1.20.7.0", {"center": v(110, -38.5) * mm, "radius": 2.5 * mm});
            skCircle(sketch, "E1.20.8.0", {"center": v(110, -44) * mm, "radius": 2.5 * mm});
            skCircle(sketch, "E1.20.9.0", {"center": v(110, -49.5) * mm, "radius": 2.5 * mm});
            skCircle(sketch, "E1.20.10.0", {"center": v(110, -55) * mm, "radius": 2.5 * mm});
            skCircle(sketch, "E1.20.11.0", {"center": v(110, -60.5) * mm, "radius": 2.5 * mm});
            skCircle(sketch, "E1.20.12.0", {"center": v(110, -66) * mm, "radius": 2.5 * mm});
            skCircle(sketch, "E1.20.13.0", {"center": v(110, -71.5) * mm, "radius": 2.5 * mm});
            skCircle(sketch, "E1.20.14.0", {"center": v(110, -77) * mm, "radius": 2.5 * mm});
            skCircle(sketch, "E1.20.15.0", {"center": v(110, -82.5) * mm, "radius": 2.5 * mm});
            skCircle(sketch, "E1.20.16.0", {"center": v(110, -88) * mm, "radius": 2.5 * mm});
            skCircle(sketch, "E1.20.17.0", {"center": v(110, -93.5) * mm, "radius": 2.5 * mm});
            skCircle(sketch, "E1.20.18.0", {"center": v(110, -99) * mm, "radius": 2.5 * mm});
            skCircle(sketch, "E1.20.19.0", {"center": v(110, -104.5) * mm, "radius": 2.5 * mm});
            skCircle(sketch, "E1.20.20.0", {"center": v(110, -110) * mm, "radius": 2.5 * mm});
            skCircle(sketch, "E1.20.21.0", {"center": v(110, -115.5) * mm, "radius": 2.5 * mm});
            skCircle(sketch, "E1.20.22.0", {"center": v(110, -121) * mm, "radius": 2.5 * mm});
            skCircle(sketch, "E1.20.23.0", {"center": v(110, -126.5) * mm, "radius": 2.5 * mm});
            skCircle(sketch, "E1.20.24.0", {"center": v(110, -132) * mm, "radius": 2.5 * mm});
            skCircle(sketch, "E1.21.0.0", {"center": v(115.5, 0) * mm, "radius": 2.5 * mm});
            skCircle(sketch, "E1.21.1.0", {"center": v(115.5, -5.5) * mm, "radius": 2.5 * mm});
            skCircle(sketch, "E1.21.2.0", {"center": v(115.5, -11) * mm, "radius": 2.5 * mm});
            skCircle(sketch, "E1.21.3.0", {"center": v(115.5, -16.5) * mm, "radius": 2.5 * mm});
            skCircle(sketch, "E1.21.4.0", {"center": v(115.5, -22) * mm, "radius": 2.5 * mm});
            skCircle(sketch, "E1.21.5.0", {"center": v(115.5, -27.5) * mm, "radius": 2.5 * mm});
            skCircle(sketch, "E1.21.6.0", {"center": v(115.5, -33) * mm, "radius": 2.5 * mm});
            skCircle(sketch, "E1.21.7.0", {"center": v(115.5, -38.5) * mm, "radius": 2.5 * mm});
            skCircle(sketch, "E1.21.8.0", {"center": v(115.5, -44) * mm, "radius": 2.5 * mm});
            skCircle(sketch, "E1.21.9.0", {"center": v(115.5, -49.5) * mm, "radius": 2.5 * mm});
            skCircle(sketch, "E1.21.10.0", {"center": v(115.5, -55) * mm, "radius": 2.5 * mm});
            skCircle(sketch, "E1.21.11.0", {"center": v(115.5, -60.5) * mm, "radius": 2.5 * mm});
            skCircle(sketch, "E1.21.12.0", {"center": v(115.5, -66) * mm, "radius": 2.5 * mm});
            skCircle(sketch, "E1.21.13.0", {"center": v(115.5, -71.5) * mm, "radius": 2.5 * mm});
            skCircle(sketch, "E1.21.14.0", {"center": v(115.5, -77) * mm, "radius": 2.5 * mm});
            skCircle(sketch, "E1.21.15.0", {"center": v(115.5, -82.5) * mm, "radius": 2.5 * mm});
            skCircle(sketch, "E1.21.16.0", {"center": v(115.5, -88) * mm, "radius": 2.5 * mm});
            skCircle(sketch, "E1.21.17.0", {"center": v(115.5, -93.5) * mm, "radius": 2.5 * mm});
            skCircle(sketch, "E1.21.18.0", {"center": v(115.5, -99) * mm, "radius": 2.5 * mm});
            skCircle(sketch, "E1.21.19.0", {"center": v(115.5, -104.5) * mm, "radius": 2.5 * mm});
            skCircle(sketch, "E1.21.20.0", {"center": v(115.5, -110) * mm, "radius": 2.5 * mm});
            skCircle(sketch, "E1.21.21.0", {"center": v(115.5, -115.5) * mm, "radius": 2.5 * mm});
            skCircle(sketch, "E1.21.22.0", {"center": v(115.5, -121) * mm, "radius": 2.5 * mm});
            skCircle(sketch, "E1.21.23.0", {"center": v(115.5, -126.5) * mm, "radius": 2.5 * mm});
            skCircle(sketch, "E1.21.24.0", {"center": v(115.5, -132) * mm, "radius": 2.5 * mm});
            skCircle(sketch, "E1.22.0.0", {"center": v(121, 0) * mm, "radius": 2.5 * mm});
            skCircle(sketch, "E1.22.1.0", {"center": v(121, -5.5) * mm, "radius": 2.5 * mm});
            skCircle(sketch, "E1.22.2.0", {"center": v(121, -11) * mm, "radius": 2.5 * mm});
            skCircle(sketch, "E1.22.3.0", {"center": v(121, -16.5) * mm, "radius": 2.5 * mm});
            skCircle(sketch, "E1.22.4.0", {"center": v(121, -22) * mm, "radius": 2.5 * mm});
            skCircle(sketch, "E1.22.5.0", {"center": v(121, -27.5) * mm, "radius": 2.5 * mm});
            skCircle(sketch, "E1.22.6.0", {"center": v(121, -33) * mm, "radius": 2.5 * mm});
            skCircle(sketch, "E1.22.7.0", {"center": v(121, -38.5) * mm, "radius": 2.5 * mm});
            skCircle(sketch, "E1.22.8.0", {"center": v(121, -44) * mm, "radius": 2.5 * mm});
            skCircle(sketch, "E1.22.9.0", {"center": v(121, -49.5) * mm, "radius": 2.5 * mm});
            skCircle(sketch, "E1.22.10.0", {"center": v(121, -55) * mm, "radius": 2.5 * mm});
            skCircle(sketch, "E1.22.11.0", {"center": v(121, -60.5) * mm, "radius": 2.5 * mm});
            skCircle(sketch, "E1.22.12.0", {"center": v(121, -66) * mm, "radius": 2.5 * mm});
            skCircle(sketch, "E1.22.13.0", {"center": v(121, -71.5) * mm, "radius": 2.5 * mm});
            skCircle(sketch, "E1.22.14.0", {"center": v(121, -77) * mm, "radius": 2.5 * mm});
            skCircle(sketch, "E1.22.15.0", {"center": v(121, -82.5) * mm, "radius": 2.5 * mm});
            skCircle(sketch, "E1.22.16.0", {"center": v(121, -88) * mm, "radius": 2.5 * mm});
            skCircle(sketch, "E1.22.17.0", {"center": v(121, -93.5) * mm, "radius": 2.5 * mm});
            skCircle(sketch, "E1.22.18.0", {"center": v(121, -99) * mm, "radius": 2.5 * mm});
            skCircle(sketch, "E1.22.19.0", {"center": v(121, -104.5) * mm, "radius": 2.5 * mm});
            skCircle(sketch, "E1.22.20.0", {"center": v(121, -110) * mm, "radius": 2.5 * mm});
            skCircle(sketch, "E1.22.21.0", {"center": v(121, -115.5) * mm, "radius": 2.5 * mm});
            skCircle(sketch, "E1.22.22.0", {"center": v(121, -121) * mm, "radius": 2.5 * mm});
            skCircle(sketch, "E1.22.23.0", {"center": v(121, -126.5) * mm, "radius": 2.5 * mm});
            skCircle(sketch, "E1.22.24.0", {"center": v(121, -132) * mm, "radius": 2.5 * mm});
            skCircle(sketch, "E1.23.0.0", {"center": v(126.5, 0) * mm, "radius": 2.5 * mm});
            skCircle(sketch, "E1.23.1.0", {"center": v(126.5, -5.5) * mm, "radius": 2.5 * mm});
            skCircle(sketch, "E1.23.2.0", {"center": v(126.5, -11) * mm, "radius": 2.5 * mm});
            skCircle(sketch, "E1.23.3.0", {"center": v(126.5, -16.5) * mm, "radius": 2.5 * mm});
            skCircle(sketch, "E1.23.4.0", {"center": v(126.5, -22) * mm, "radius": 2.5 * mm});
            skCircle(sketch, "E1.23.5.0", {"center": v(126.5, -27.5) * mm, "radius": 2.5 * mm});
            skCircle(sketch, "E1.23.6.0", {"center": v(126.5, -33) * mm, "radius": 2.5 * mm});
            skCircle(sketch, "E1.23.7.0", {"center": v(126.5, -38.5) * mm, "radius": 2.5 * mm});
            skCircle(sketch, "E1.23.8.0", {"center": v(126.5, -44) * mm, "radius": 2.5 * mm});
            skCircle(sketch, "E1.23.9.0", {"center": v(126.5, -49.5) * mm, "radius": 2.5 * mm});
            skCircle(sketch, "E1.23.10.0", {"center": v(126.5, -55) * mm, "radius": 2.5 * mm});
            skCircle(sketch, "E1.23.11.0", {"center": v(126.5, -60.5) * mm, "radius": 2.5 * mm});
            skCircle(sketch, "E1.23.12.0", {"center": v(126.5, -66) * mm, "radius": 2.5 * mm});
            skCircle(sketch, "E1.23.13.0", {"center": v(126.5, -71.5) * mm, "radius": 2.5 * mm});
            skCircle(sketch, "E1.23.14.0", {"center": v(126.5, -77) * mm, "radius": 2.5 * mm});
            skCircle(sketch, "E1.23.15.0", {"center": v(126.5, -82.5) * mm, "radius": 2.5 * mm});
            skCircle(sketch, "E1.23.16.0", {"center": v(126.5, -88) * mm, "radius": 2.5 * mm});
            skCircle(sketch, "E1.23.17.0", {"center": v(126.5, -93.5) * mm, "radius": 2.5 * mm});
            skCircle(sketch, "E1.23.18.0", {"center": v(126.5, -99) * mm, "radius": 2.5 * mm});
            skCircle(sketch, "E1.23.19.0", {"center": v(126.5, -104.5) * mm, "radius": 2.5 * mm});
            skCircle(sketch, "E1.23.20.0", {"center": v(126.5, -110) * mm, "radius": 2.5 * mm});
            skCircle(sketch, "E1.23.21.0", {"center": v(126.5, -115.5) * mm, "radius": 2.5 * mm});
            skCircle(sketch, "E1.23.22.0", {"center": v(126.5, -121) * mm, "radius": 2.5 * mm});
            skCircle(sketch, "E1.23.23.0", {"center": v(126.5, -126.5) * mm, "radius": 2.5 * mm});
            skCircle(sketch, "E1.23.24.0", {"center": v(126.5, -132) * mm, "radius": 2.5 * mm});
            skCircle(sketch, "E1.24.0.0", {"center": v(132, 0) * mm, "radius": 2.5 * mm});
            skCircle(sketch, "E1.24.1.0", {"center": v(132, -5.5) * mm, "radius": 2.5 * mm});
            skCircle(sketch, "E1.24.2.0", {"center": v(132, -11) * mm, "radius": 2.5 * mm});
            skCircle(sketch, "E1.24.3.0", {"center": v(132, -16.5) * mm, "radius": 2.5 * mm});
            skCircle(sketch, "E1.24.4.0", {"center": v(132, -22) * mm, "radius": 2.5 * mm});
            skCircle(sketch, "E1.24.5.0", {"center": v(132, -27.5) * mm, "radius": 2.5 * mm});
            skCircle(sketch, "E1.24.6.0", {"center": v(132, -33) * mm, "radius": 2.5 * mm});
            skCircle(sketch, "E1.24.7.0", {"center": v(132, -38.5) * mm, "radius": 2.5 * mm});
            skCircle(sketch, "E1.24.8.0", {"center": v(132, -44) * mm, "radius": 2.5 * mm});
            skCircle(sketch, "E1.24.9.0", {"center": v(132, -49.5) * mm, "radius": 2.5 * mm});
            skCircle(sketch, "E1.24.10.0", {"center": v(132, -55) * mm, "radius": 2.5 * mm});
            skCircle(sketch, "E1.24.11.0", {"center": v(132, -60.5) * mm, "radius": 2.5 * mm});
            skCircle(sketch, "E1.24.12.0", {"center": v(132, -66) * mm, "radius": 2.5 * mm});
            skCircle(sketch, "E1.24.13.0", {"center": v(132, -71.5) * mm, "radius": 2.5 * mm});
            skCircle(sketch, "E1.24.14.0", {"center": v(132, -77) * mm, "radius": 2.5 * mm});
            skCircle(sketch, "E1.24.15.0", {"center": v(132, -82.5) * mm, "radius": 2.5 * mm});
            skCircle(sketch, "E1.24.16.0", {"center": v(132, -88) * mm, "radius": 2.5 * mm});
            skCircle(sketch, "E1.24.17.0", {"center": v(132, -93.5) * mm, "radius": 2.5 * mm});
            skCircle(sketch, "E1.24.18.0", {"center": v(132, -99) * mm, "radius": 2.5 * mm});
            skCircle(sketch, "E1.24.19.0", {"center": v(132, -104.5) * mm, "radius": 2.5 * mm});
            skCircle(sketch, "E1.24.20.0", {"center": v(132, -110) * mm, "radius": 2.5 * mm});
            skCircle(sketch, "E1.24.21.0", {"center": v(132, -115.5) * mm, "radius": 2.5 * mm});
            skCircle(sketch, "E1.24.22.0", {"center": v(132, -121) * mm, "radius": 2.5 * mm});
            skCircle(sketch, "E1.24.23.0", {"center": v(132, -126.5) * mm, "radius": 2.5 * mm});
            skCircle(sketch, "E1.24.24.0", {"center": v(132, -132) * mm, "radius": 2.5 * mm});
            skCircle(sketch, "E1.25.0.0", {"center": v(137.5, 0) * mm, "radius": 2.5 * mm});
            skCircle(sketch, "E1.25.1.0", {"center": v(137.5, -5.5) * mm, "radius": 2.5 * mm});
            skCircle(sketch, "E1.25.2.0", {"center": v(137.5, -11) * mm, "radius": 2.5 * mm});
            skCircle(sketch, "E1.25.3.0", {"center": v(137.5, -16.5) * mm, "radius": 2.5 * mm});
            skCircle(sketch, "E1.25.4.0", {"center": v(137.5, -22) * mm, "radius": 2.5 * mm});
            skCircle(sketch, "E1.25.5.0", {"center": v(137.5, -27.5) * mm, "radius": 2.5 * mm});
            skCircle(sketch, "E1.25.6.0", {"center": v(137.5, -33) * mm, "radius": 2.5 * mm});
            skCircle(sketch, "E1.25.7.0", {"center": v(137.5, -38.5) * mm, "radius": 2.5 * mm});
            skCircle(sketch, "E1.25.8.0", {"center": v(137.5, -44) * mm, "radius": 2.5 * mm});
            skCircle(sketch, "E1.25.9.0", {"center": v(137.5, -49.5) * mm, "radius": 2.5 * mm});
            skCircle(sketch, "E1.25.10.0", {"center": v(137.5, -55) * mm, "radius": 2.5 * mm});
            skCircle(sketch, "E1.25.11.0", {"center": v(137.5, -60.5) * mm, "radius": 2.5 * mm});
            skCircle(sketch, "E1.25.12.0", {"center": v(137.5, -66) * mm, "radius": 2.5 * mm});
            skCircle(sketch, "E1.25.13.0", {"center": v(137.5, -71.5) * mm, "radius": 2.5 * mm});
            skCircle(sketch, "E1.25.14.0", {"center": v(137.5, -77) * mm, "radius": 2.5 * mm});
            skCircle(sketch, "E1.25.15.0", {"center": v(137.5, -82.5) * mm, "radius": 2.5 * mm});
            skCircle(sketch, "E1.25.16.0", {"center": v(137.5, -88) * mm, "radius": 2.5 * mm});
            skCircle(sketch, "E1.25.17.0", {"center": v(137.5, -93.5) * mm, "radius": 2.5 * mm});
            skCircle(sketch, "E1.25.18.0", {"center": v(137.5, -99) * mm, "radius": 2.5 * mm});
            skCircle(sketch, "E1.25.19.0", {"center": v(137.5, -104.5) * mm, "radius": 2.5 * mm});
            skCircle(sketch, "E1.25.20.0", {"center": v(137.5, -110) * mm, "radius": 2.5 * mm});
            skCircle(sketch, "E1.25.21.0", {"center": v(137.5, -115.5) * mm, "radius": 2.5 * mm});
            skCircle(sketch, "E1.25.22.0", {"center": v(137.5, -121) * mm, "radius": 2.5 * mm});
            skCircle(sketch, "E1.25.23.0", {"center": v(137.5, -126.5) * mm, "radius": 2.5 * mm});
            skCircle(sketch, "E1.25.24.0", {"center": v(137.5, -132) * mm, "radius": 2.5 * mm});
            skCircle(sketch, "E1.26.0.0", {"center": v(143, 0) * mm, "radius": 2.5 * mm});
            skCircle(sketch, "E1.26.1.0", {"center": v(143, -5.5) * mm, "radius": 2.5 * mm});
            skCircle(sketch, "E1.26.2.0", {"center": v(143, -11) * mm, "radius": 2.5 * mm});
            skCircle(sketch, "E1.26.3.0", {"center": v(143, -16.5) * mm, "radius": 2.5 * mm});
            skCircle(sketch, "E1.26.4.0", {"center": v(143, -22) * mm, "radius": 2.5 * mm});
            skCircle(sketch, "E1.26.5.0", {"center": v(143, -27.5) * mm, "radius": 2.5 * mm});
            skCircle(sketch, "E1.26.6.0", {"center": v(143, -33) * mm, "radius": 2.5 * mm});
            skCircle(sketch, "E1.26.7.0", {"center": v(143, -38.5) * mm, "radius": 2.5 * mm});
            skCircle(sketch, "E1.26.8.0", {"center": v(143, -44) * mm, "radius": 2.5 * mm});
            skCircle(sketch, "E1.26.9.0", {"center": v(143, -49.5) * mm, "radius": 2.5 * mm});
            skCircle(sketch, "E1.26.10.0", {"center": v(143, -55) * mm, "radius": 2.5 * mm});
            skCircle(sketch, "E1.26.11.0", {"center": v(143, -60.5) * mm, "radius": 2.5 * mm});
            skCircle(sketch, "E1.26.12.0", {"center": v(143, -66) * mm, "radius": 2.5 * mm});
            skCircle(sketch, "E1.26.13.0", {"center": v(143, -71.5) * mm, "radius": 2.5 * mm});
            skCircle(sketch, "E1.26.14.0", {"center": v(143, -77) * mm, "radius": 2.5 * mm});
            skCircle(sketch, "E1.26.15.0", {"center": v(143, -82.5) * mm, "radius": 2.5 * mm});
            skCircle(sketch, "E1.26.16.0", {"center": v(143, -88) * mm, "radius": 2.5 * mm});
            skCircle(sketch, "E1.26.17.0", {"center": v(143, -93.5) * mm, "radius": 2.5 * mm});
            skCircle(sketch, "E1.26.18.0", {"center": v(143, -99) * mm, "radius": 2.5 * mm});
            skCircle(sketch, "E1.26.19.0", {"center": v(143, -104.5) * mm, "radius": 2.5 * mm});
            skCircle(sketch, "E1.26.20.0", {"center": v(143, -110) * mm, "radius": 2.5 * mm});
            skCircle(sketch, "E1.26.21.0", {"center": v(143, -115.5) * mm, "radius": 2.5 * mm});
            skCircle(sketch, "E1.26.22.0", {"center": v(143, -121) * mm, "radius": 2.5 * mm});
            skCircle(sketch, "E1.26.23.0", {"center": v(143, -126.5) * mm, "radius": 2.5 * mm});
            skCircle(sketch, "E1.26.24.0", {"center": v(143, -132) * mm, "radius": 2.5 * mm});
            skCircle(sketch, "E1.27.0.0", {"center": v(148.5, 0) * mm, "radius": 2.5 * mm});
            skCircle(sketch, "E1.27.1.0", {"center": v(148.5, -5.5) * mm, "radius": 2.5 * mm});
            skCircle(sketch, "E1.27.2.0", {"center": v(148.5, -11) * mm, "radius": 2.5 * mm});
            skCircle(sketch, "E1.27.3.0", {"center": v(148.5, -16.5) * mm, "radius": 2.5 * mm});
            skCircle(sketch, "E1.27.4.0", {"center": v(148.5, -22) * mm, "radius": 2.5 * mm});
            skCircle(sketch, "E1.27.5.0", {"center": v(148.5, -27.5) * mm, "radius": 2.5 * mm});
            skCircle(sketch, "E1.27.6.0", {"center": v(148.5, -33) * mm, "radius": 2.5 * mm});
            skCircle(sketch, "E1.27.7.0", {"center": v(148.5, -38.5) * mm, "radius": 2.5 * mm});
            skCircle(sketch, "E1.27.8.0", {"center": v(148.5, -44) * mm, "radius": 2.5 * mm});
            skCircle(sketch, "E1.27.9.0", {"center": v(148.5, -49.5) * mm, "radius": 2.5 * mm});
            skCircle(sketch, "E1.27.10.0", {"center": v(148.5, -55) * mm, "radius": 2.5 * mm});
            skCircle(sketch, "E1.27.11.0", {"center": v(148.5, -60.5) * mm, "radius": 2.5 * mm});
            skCircle(sketch, "E1.27.12.0", {"center": v(148.5, -66) * mm, "radius": 2.5 * mm});
            skCircle(sketch, "E1.27.13.0", {"center": v(148.5, -71.5) * mm, "radius": 2.5 * mm});
            skCircle(sketch, "E1.27.14.0", {"center": v(148.5, -77) * mm, "radius": 2.5 * mm});
            skCircle(sketch, "E1.27.15.0", {"center": v(148.5, -82.5) * mm, "radius": 2.5 * mm});
            skCircle(sketch, "E1.27.16.0", {"center": v(148.5, -88) * mm, "radius": 2.5 * mm});
            skCircle(sketch, "E1.27.17.0", {"center": v(148.5, -93.5) * mm, "radius": 2.5 * mm});
            skCircle(sketch, "E1.27.18.0", {"center": v(148.5, -99) * mm, "radius": 2.5 * mm});
            skCircle(sketch, "E1.27.19.0", {"center": v(148.5, -104.5) * mm, "radius": 2.5 * mm});
            skCircle(sketch, "E1.27.20.0", {"center": v(148.5, -110) * mm, "radius": 2.5 * mm});
            skCircle(sketch, "E1.27.21.0", {"center": v(148.5, -115.5) * mm, "radius": 2.5 * mm});
            skCircle(sketch, "E1.27.22.0", {"center": v(148.5, -121) * mm, "radius": 2.5 * mm});
            skCircle(sketch, "E1.27.23.0", {"center": v(148.5, -126.5) * mm, "radius": 2.5 * mm});
            skCircle(sketch, "E1.27.24.0", {"center": v(148.5, -132) * mm, "radius": 2.5 * mm});
            skCircle(sketch, "E1.28.0.0", {"center": v(154, 0) * mm, "radius": 2.5 * mm});
            skCircle(sketch, "E1.28.1.0", {"center": v(154, -5.5) * mm, "radius": 2.5 * mm});
            skCircle(sketch, "E1.28.2.0", {"center": v(154, -11) * mm, "radius": 2.5 * mm});
            skCircle(sketch, "E1.28.3.0", {"center": v(154, -16.5) * mm, "radius": 2.5 * mm});
            skCircle(sketch, "E1.28.4.0", {"center": v(154, -22) * mm, "radius": 2.5 * mm});
            skCircle(sketch, "E1.28.5.0", {"center": v(154, -27.5) * mm, "radius": 2.5 * mm});
            skCircle(sketch, "E1.28.6.0", {"center": v(154, -33) * mm, "radius": 2.5 * mm});
            skCircle(sketch, "E1.28.7.0", {"center": v(154, -38.5) * mm, "radius": 2.5 * mm});
            skCircle(sketch, "E1.28.8.0", {"center": v(154, -44) * mm, "radius": 2.5 * mm});
            skCircle(sketch, "E1.28.9.0", {"center": v(154, -49.5) * mm, "radius": 2.5 * mm});
            skCircle(sketch, "E1.28.10.0", {"center": v(154, -55) * mm, "radius": 2.5 * mm});
            skCircle(sketch, "E1.28.11.0", {"center": v(154, -60.5) * mm, "radius": 2.5 * mm});
            skCircle(sketch, "E1.28.12.0", {"center": v(154, -66) * mm, "radius": 2.5 * mm});
            skCircle(sketch, "E1.28.13.0", {"center": v(154, -71.5) * mm, "radius": 2.5 * mm});
            skCircle(sketch, "E1.28.14.0", {"center": v(154, -77) * mm, "radius": 2.5 * mm});
            skCircle(sketch, "E1.28.15.0", {"center": v(154, -82.5) * mm, "radius": 2.5 * mm});
            skCircle(sketch, "E1.28.16.0", {"center": v(154, -88) * mm, "radius": 2.5 * mm});
            skCircle(sketch, "E1.28.17.0", {"center": v(154, -93.5) * mm, "radius": 2.5 * mm});
            skCircle(sketch, "E1.28.18.0", {"center": v(154, -99) * mm, "radius": 2.5 * mm});
            skCircle(sketch, "E1.28.19.0", {"center": v(154, -104.5) * mm, "radius": 2.5 * mm});
            skCircle(sketch, "E1.28.20.0", {"center": v(154, -110) * mm, "radius": 2.5 * mm});
            skCircle(sketch, "E1.28.21.0", {"center": v(154, -115.5) * mm, "radius": 2.5 * mm});
            skCircle(sketch, "E1.28.22.0", {"center": v(154, -121) * mm, "radius": 2.5 * mm});
            skCircle(sketch, "E1.28.23.0", {"center": v(154, -126.5) * mm, "radius": 2.5 * mm});
            skCircle(sketch, "E1.28.24.0", {"center": v(154, -132) * mm, "radius": 2.5 * mm});
            skCircle(sketch, "E1.29.0.0", {"center": v(159.5, 0) * mm, "radius": 2.5 * mm});
            skCircle(sketch, "E1.29.1.0", {"center": v(159.5, -5.5) * mm, "radius": 2.5 * mm});
            skCircle(sketch, "E1.29.2.0", {"center": v(159.5, -11) * mm, "radius": 2.5 * mm});
            skCircle(sketch, "E1.29.3.0", {"center": v(159.5, -16.5) * mm, "radius": 2.5 * mm});
            skCircle(sketch, "E1.29.4.0", {"center": v(159.5, -22) * mm, "radius": 2.5 * mm});
            skCircle(sketch, "E1.29.5.0", {"center": v(159.5, -27.5) * mm, "radius": 2.5 * mm});
            skCircle(sketch, "E1.29.6.0", {"center": v(159.5, -33) * mm, "radius": 2.5 * mm});
            skCircle(sketch, "E1.29.7.0", {"center": v(159.5, -38.5) * mm, "radius": 2.5 * mm});
            skCircle(sketch, "E1.29.8.0", {"center": v(159.5, -44) * mm, "radius": 2.5 * mm});
            skCircle(sketch, "E1.29.9.0", {"center": v(159.5, -49.5) * mm, "radius": 2.5 * mm});
            skCircle(sketch, "E1.29.10.0", {"center": v(159.5, -55) * mm, "radius": 2.5 * mm});
            skCircle(sketch, "E1.29.11.0", {"center": v(159.5, -60.5) * mm, "radius": 2.5 * mm});
            skCircle(sketch, "E1.29.12.0", {"center": v(159.5, -66) * mm, "radius": 2.5 * mm});
            skCircle(sketch, "E1.29.13.0", {"center": v(159.5, -71.5) * mm, "radius": 2.5 * mm});
            skCircle(sketch, "E1.29.14.0", {"center": v(159.5, -77) * mm, "radius": 2.5 * mm});
            skCircle(sketch, "E1.29.15.0", {"center": v(159.5, -82.5) * mm, "radius": 2.5 * mm});
            skCircle(sketch, "E1.29.16.0", {"center": v(159.5, -88) * mm, "radius": 2.5 * mm});
            skCircle(sketch, "E1.29.17.0", {"center": v(159.5, -93.5) * mm, "radius": 2.5 * mm});
            skCircle(sketch, "E1.29.18.0", {"center": v(159.5, -99) * mm, "radius": 2.5 * mm});
            skCircle(sketch, "E1.29.19.0", {"center": v(159.5, -104.5) * mm, "radius": 2.5 * mm});
            skCircle(sketch, "E1.29.20.0", {"center": v(159.5, -110) * mm, "radius": 2.5 * mm});
            skCircle(sketch, "E1.29.21.0", {"center": v(159.5, -115.5) * mm, "radius": 2.5 * mm});
            skCircle(sketch, "E1.29.22.0", {"center": v(159.5, -121) * mm, "radius": 2.5 * mm});
            skCircle(sketch, "E1.29.23.0", {"center": v(159.5, -126.5) * mm, "radius": 2.5 * mm});
            skCircle(sketch, "E1.29.24.0", {"center": v(159.5, -132) * mm, "radius": 2.5 * mm});
            skCircle(sketch, "E1.30.0.0", {"center": v(165, 0) * mm, "radius": 2.5 * mm});
            skCircle(sketch, "E1.30.1.0", {"center": v(165, -5.5) * mm, "radius": 2.5 * mm});
            skCircle(sketch, "E1.30.2.0", {"center": v(165, -11) * mm, "radius": 2.5 * mm});
            skCircle(sketch, "E1.30.3.0", {"center": v(165, -16.5) * mm, "radius": 2.5 * mm});
            skCircle(sketch, "E1.30.4.0", {"center": v(165, -22) * mm, "radius": 2.5 * mm});
            skCircle(sketch, "E1.30.5.0", {"center": v(165, -27.5) * mm, "radius": 2.5 * mm});
            skCircle(sketch, "E1.30.6.0", {"center": v(165, -33) * mm, "radius": 2.5 * mm});
            skCircle(sketch, "E1.30.7.0", {"center": v(165, -38.5) * mm, "radius": 2.5 * mm});
            skCircle(sketch, "E1.30.8.0", {"center": v(165, -44) * mm, "radius": 2.5 * mm});
            skCircle(sketch, "E1.30.9.0", {"center": v(165, -49.5) * mm, "radius": 2.5 * mm});
            skCircle(sketch, "E1.30.10.0", {"center": v(165, -55) * mm, "radius": 2.5 * mm});
            skCircle(sketch, "E1.30.11.0", {"center": v(165, -60.5) * mm, "radius": 2.5 * mm});
            skCircle(sketch, "E1.30.12.0", {"center": v(165, -66) * mm, "radius": 2.5 * mm});
            skCircle(sketch, "E1.30.13.0", {"center": v(165, -71.5) * mm, "radius": 2.5 * mm});
            skCircle(sketch, "E1.30.14.0", {"center": v(165, -77) * mm, "radius": 2.5 * mm});
            skCircle(sketch, "E1.30.15.0", {"center": v(165, -82.5) * mm, "radius": 2.5 * mm});
            skCircle(sketch, "E1.30.16.0", {"center": v(165, -88) * mm, "radius": 2.5 * mm});
            skCircle(sketch, "E1.30.17.0", {"center": v(165, -93.5) * mm, "radius": 2.5 * mm});
            skCircle(sketch, "E1.30.18.0", {"center": v(165, -99) * mm, "radius": 2.5 * mm});
            skCircle(sketch, "E1.30.19.0", {"center": v(165, -104.5) * mm, "radius": 2.5 * mm});
            skCircle(sketch, "E1.30.20.0", {"center": v(165, -110) * mm, "radius": 2.5 * mm});
            skCircle(sketch, "E1.30.21.0", {"center": v(165, -115.5) * mm, "radius": 2.5 * mm});
            skCircle(sketch, "E1.30.22.0", {"center": v(165, -121) * mm, "radius": 2.5 * mm});
            skCircle(sketch, "E1.30.23.0", {"center": v(165, -126.5) * mm, "radius": 2.5 * mm});
            skCircle(sketch, "E1.30.24.0", {"center": v(165, -132) * mm, "radius": 2.5 * mm});
            skCircle(sketch, "E1.31.0.0", {"center": v(170.5, 0) * mm, "radius": 2.5 * mm});
            skCircle(sketch, "E1.31.1.0", {"center": v(170.5, -5.5) * mm, "radius": 2.5 * mm});
            skCircle(sketch, "E1.31.2.0", {"center": v(170.5, -11) * mm, "radius": 2.5 * mm});
            skCircle(sketch, "E1.31.3.0", {"center": v(170.5, -16.5) * mm, "radius": 2.5 * mm});
            skCircle(sketch, "E1.31.4.0", {"center": v(170.5, -22) * mm, "radius": 2.5 * mm});
            skCircle(sketch, "E1.31.5.0", {"center": v(170.5, -27.5) * mm, "radius": 2.5 * mm});
            skCircle(sketch, "E1.31.6.0", {"center": v(170.5, -33) * mm, "radius": 2.5 * mm});
            skCircle(sketch, "E1.31.7.0", {"center": v(170.5, -38.5) * mm, "radius": 2.5 * mm});
            skCircle(sketch, "E1.31.8.0", {"center": v(170.5, -44) * mm, "radius": 2.5 * mm});
            skCircle(sketch, "E1.31.9.0", {"center": v(170.5, -49.5) * mm, "radius": 2.5 * mm});
            skCircle(sketch, "E1.31.10.0", {"center": v(170.5, -55) * mm, "radius": 2.5 * mm});
            skCircle(sketch, "E1.31.11.0", {"center": v(170.5, -60.5) * mm, "radius": 2.5 * mm});
            skCircle(sketch, "E1.31.12.0", {"center": v(170.5, -66) * mm, "radius": 2.5 * mm});
            skCircle(sketch, "E1.31.13.0", {"center": v(170.5, -71.5) * mm, "radius": 2.5 * mm});
            skCircle(sketch, "E1.31.14.0", {"center": v(170.5, -77) * mm, "radius": 2.5 * mm});
            skCircle(sketch, "E1.31.15.0", {"center": v(170.5, -82.5) * mm, "radius": 2.5 * mm});
            skCircle(sketch, "E1.31.16.0", {"center": v(170.5, -88) * mm, "radius": 2.5 * mm});
            skCircle(sketch, "E1.31.17.0", {"center": v(170.5, -93.5) * mm, "radius": 2.5 * mm});
            skCircle(sketch, "E1.31.18.0", {"center": v(170.5, -99) * mm, "radius": 2.5 * mm});
            skCircle(sketch, "E1.31.19.0", {"center": v(170.5, -104.5) * mm, "radius": 2.5 * mm});
            skCircle(sketch, "E1.31.20.0", {"center": v(170.5, -110) * mm, "radius": 2.5 * mm});
            skCircle(sketch, "E1.31.21.0", {"center": v(170.5, -115.5) * mm, "radius": 2.5 * mm});
            skCircle(sketch, "E1.31.22.0", {"center": v(170.5, -121) * mm, "radius": 2.5 * mm});
            skCircle(sketch, "E1.31.23.0", {"center": v(170.5, -126.5) * mm, "radius": 2.5 * mm});
            skCircle(sketch, "E1.31.24.0", {"center": v(170.5, -132) * mm, "radius": 2.5 * mm});
            skCircle(sketch, "E1.32.0.0", {"center": v(176, 0) * mm, "radius": 2.5 * mm});
            skCircle(sketch, "E1.32.1.0", {"center": v(176, -5.5) * mm, "radius": 2.5 * mm});
            skCircle(sketch, "E1.32.2.0", {"center": v(176, -11) * mm, "radius": 2.5 * mm});
            skCircle(sketch, "E1.32.3.0", {"center": v(176, -16.5) * mm, "radius": 2.5 * mm});
            skCircle(sketch, "E1.32.4.0", {"center": v(176, -22) * mm, "radius": 2.5 * mm});
            skCircle(sketch, "E1.32.5.0", {"center": v(176, -27.5) * mm, "radius": 2.5 * mm});
            skCircle(sketch, "E1.32.6.0", {"center": v(176, -33) * mm, "radius": 2.5 * mm});
            skCircle(sketch, "E1.32.7.0", {"center": v(176, -38.5) * mm, "radius": 2.5 * mm});
            skCircle(sketch, "E1.32.8.0", {"center": v(176, -44) * mm, "radius": 2.5 * mm});
            skCircle(sketch, "E1.32.9.0", {"center": v(176, -49.5) * mm, "radius": 2.5 * mm});
            skCircle(sketch, "E1.32.10.0", {"center": v(176, -55) * mm, "radius": 2.5 * mm});
            skCircle(sketch, "E1.32.11.0", {"center": v(176, -60.5) * mm, "radius": 2.5 * mm});
            skCircle(sketch, "E1.32.12.0", {"center": v(176, -66) * mm, "radius": 2.5 * mm});
            skCircle(sketch, "E1.32.13.0", {"center": v(176, -71.5) * mm, "radius": 2.5 * mm});
            skCircle(sketch, "E1.32.14.0", {"center": v(176, -77) * mm, "radius": 2.5 * mm});
            skCircle(sketch, "E1.32.15.0", {"center": v(176, -82.5) * mm, "radius": 2.5 * mm});
            skCircle(sketch, "E1.32.16.0", {"center": v(176, -88) * mm, "radius": 2.5 * mm});
            skCircle(sketch, "E1.32.17.0", {"center": v(176, -93.5) * mm, "radius": 2.5 * mm});
            skCircle(sketch, "E1.32.18.0", {"center": v(176, -99) * mm, "radius": 2.5 * mm});
            skCircle(sketch, "E1.32.19.0", {"center": v(176, -104.5) * mm, "radius": 2.5 * mm});
            skCircle(sketch, "E1.32.20.0", {"center": v(176, -110) * mm, "radius": 2.5 * mm});
            skCircle(sketch, "E1.32.21.0", {"center": v(176, -115.5) * mm, "radius": 2.5 * mm});
            skCircle(sketch, "E1.32.22.0", {"center": v(176, -121) * mm, "radius": 2.5 * mm});
            skCircle(sketch, "E1.32.23.0", {"center": v(176, -126.5) * mm, "radius": 2.5 * mm});
            skCircle(sketch, "E1.32.24.0", {"center": v(176, -132) * mm, "radius": 2.5 * mm});
            skCircle(sketch, "E1.33.0.0", {"center": v(181.5, 0) * mm, "radius": 2.5 * mm});
            skCircle(sketch, "E1.33.1.0", {"center": v(181.5, -5.5) * mm, "radius": 2.5 * mm});
            skCircle(sketch, "E1.33.2.0", {"center": v(181.5, -11) * mm, "radius": 2.5 * mm});
            skCircle(sketch, "E1.33.3.0", {"center": v(181.5, -16.5) * mm, "radius": 2.5 * mm});
            skCircle(sketch, "E1.33.4.0", {"center": v(181.5, -22) * mm, "radius": 2.5 * mm});
            skCircle(sketch, "E1.33.5.0", {"center": v(181.5, -27.5) * mm, "radius": 2.5 * mm});
            skCircle(sketch, "E1.33.6.0", {"center": v(181.5, -33) * mm, "radius": 2.5 * mm});
            skCircle(sketch, "E1.33.7.0", {"center": v(181.5, -38.5) * mm, "radius": 2.5 * mm});
            skCircle(sketch, "E1.33.8.0", {"center": v(181.5, -44) * mm, "radius": 2.5 * mm});
            skCircle(sketch, "E1.33.9.0", {"center": v(181.5, -49.5) * mm, "radius": 2.5 * mm});
            skCircle(sketch, "E1.33.10.0", {"center": v(181.5, -55) * mm, "radius": 2.5 * mm});
            skCircle(sketch, "E1.33.11.0", {"center": v(181.5, -60.5) * mm, "radius": 2.5 * mm});
            skCircle(sketch, "E1.33.12.0", {"center": v(181.5, -66) * mm, "radius": 2.5 * mm});
            skCircle(sketch, "E1.33.13.0", {"center": v(181.5, -71.5) * mm, "radius": 2.5 * mm});
            skCircle(sketch, "E1.33.14.0", {"center": v(181.5, -77) * mm, "radius": 2.5 * mm});
            skCircle(sketch, "E1.33.15.0", {"center": v(181.5, -82.5) * mm, "radius": 2.5 * mm});
            skCircle(sketch, "E1.33.16.0", {"center": v(181.5, -88) * mm, "radius": 2.5 * mm});
            skCircle(sketch, "E1.33.17.0", {"center": v(181.5, -93.5) * mm, "radius": 2.5 * mm});
            skCircle(sketch, "E1.33.18.0", {"center": v(181.5, -99) * mm, "radius": 2.5 * mm});
            skCircle(sketch, "E1.33.19.0", {"center": v(181.5, -104.5) * mm, "radius": 2.5 * mm});
            skCircle(sketch, "E1.33.20.0", {"center": v(181.5, -110) * mm, "radius": 2.5 * mm});
            skCircle(sketch, "E1.33.21.0", {"center": v(181.5, -115.5) * mm, "radius": 2.5 * mm});
            skCircle(sketch, "E1.33.22.0", {"center": v(181.5, -121) * mm, "radius": 2.5 * mm});
            skCircle(sketch, "E1.33.23.0", {"center": v(181.5, -126.5) * mm, "radius": 2.5 * mm});
            skCircle(sketch, "E1.33.24.0", {"center": v(181.5, -132) * mm, "radius": 2.5 * mm});
            skCircle(sketch, "E1.34.0.0", {"center": v(187, 0) * mm, "radius": 2.5 * mm});
            skCircle(sketch, "E1.34.1.0", {"center": v(187, -5.5) * mm, "radius": 2.5 * mm});
            skCircle(sketch, "E1.34.2.0", {"center": v(187, -11) * mm, "radius": 2.5 * mm});
            skCircle(sketch, "E1.34.3.0", {"center": v(187, -16.5) * mm, "radius": 2.5 * mm});
            skCircle(sketch, "E1.34.4.0", {"center": v(187, -22) * mm, "radius": 2.5 * mm});
            skCircle(sketch, "E1.34.5.0", {"center": v(187, -27.5) * mm, "radius": 2.5 * mm});
            skCircle(sketch, "E1.34.6.0", {"center": v(187, -33) * mm, "radius": 2.5 * mm});
            skCircle(sketch, "E1.34.7.0", {"center": v(187, -38.5) * mm, "radius": 2.5 * mm});
            skCircle(sketch, "E1.34.8.0", {"center": v(187, -44) * mm, "radius": 2.5 * mm});
            skCircle(sketch, "E1.34.9.0", {"center": v(187, -49.5) * mm, "radius": 2.5 * mm});
            skCircle(sketch, "E1.34.10.0", {"center": v(187, -55) * mm, "radius": 2.5 * mm});
            skCircle(sketch, "E1.34.11.0", {"center": v(187, -60.5) * mm, "radius": 2.5 * mm});
            skCircle(sketch, "E1.34.12.0", {"center": v(187, -66) * mm, "radius": 2.5 * mm});
            skCircle(sketch, "E1.34.13.0", {"center": v(187, -71.5) * mm, "radius": 2.5 * mm});
            skCircle(sketch, "E1.34.14.0", {"center": v(187, -77) * mm, "radius": 2.5 * mm});
            skCircle(sketch, "E1.34.15.0", {"center": v(187, -82.5) * mm, "radius": 2.5 * mm});
            skCircle(sketch, "E1.34.16.0", {"center": v(187, -88) * mm, "radius": 2.5 * mm});
            skCircle(sketch, "E1.34.17.0", {"center": v(187, -93.5) * mm, "radius": 2.5 * mm});
            skCircle(sketch, "E1.34.18.0", {"center": v(187, -99) * mm, "radius": 2.5 * mm});
            skCircle(sketch, "E1.34.19.0", {"center": v(187, -104.5) * mm, "radius": 2.5 * mm});
            skCircle(sketch, "E1.34.20.0", {"center": v(187, -110) * mm, "radius": 2.5 * mm});
            skCircle(sketch, "E1.34.21.0", {"center": v(187, -115.5) * mm, "radius": 2.5 * mm});
            skCircle(sketch, "E1.34.22.0", {"center": v(187, -121) * mm, "radius": 2.5 * mm});
            skCircle(sketch, "E1.34.23.0", {"center": v(187, -126.5) * mm, "radius": 2.5 * mm});
            skCircle(sketch, "E1.34.24.0", {"center": v(187, -132) * mm, "radius": 2.5 * mm});
            skCircle(sketch, "E1.35.0.0", {"center": v(192.5, 0) * mm, "radius": 2.5 * mm});
            skCircle(sketch, "E1.35.1.0", {"center": v(192.5, -5.5) * mm, "radius": 2.5 * mm});
            skCircle(sketch, "E1.35.2.0", {"center": v(192.5, -11) * mm, "radius": 2.5 * mm});
            skCircle(sketch, "E1.35.3.0", {"center": v(192.5, -16.5) * mm, "radius": 2.5 * mm});
            skCircle(sketch, "E1.35.4.0", {"center": v(192.5, -22) * mm, "radius": 2.5 * mm});
            skCircle(sketch, "E1.35.5.0", {"center": v(192.5, -27.5) * mm, "radius": 2.5 * mm});
            skCircle(sketch, "E1.35.6.0", {"center": v(192.5, -33) * mm, "radius": 2.5 * mm});
            skCircle(sketch, "E1.35.7.0", {"center": v(192.5, -38.5) * mm, "radius": 2.5 * mm});
            skCircle(sketch, "E1.35.8.0", {"center": v(192.5, -44) * mm, "radius": 2.5 * mm});
            skCircle(sketch, "E1.35.9.0", {"center": v(192.5, -49.5) * mm, "radius": 2.5 * mm});
            skCircle(sketch, "E1.35.10.0", {"center": v(192.5, -55) * mm, "radius": 2.5 * mm});
            skCircle(sketch, "E1.35.11.0", {"center": v(192.5, -60.5) * mm, "radius": 2.5 * mm});
            skCircle(sketch, "E1.35.12.0", {"center": v(192.5, -66) * mm, "radius": 2.5 * mm});
            skCircle(sketch, "E1.35.13.0", {"center": v(192.5, -71.5) * mm, "radius": 2.5 * mm});
            skCircle(sketch, "E1.35.14.0", {"center": v(192.5, -77) * mm, "radius": 2.5 * mm});
            skCircle(sketch, "E1.35.15.0", {"center": v(192.5, -82.5) * mm, "radius": 2.5 * mm});
            skCircle(sketch, "E1.35.16.0", {"center": v(192.5, -88) * mm, "radius": 2.5 * mm});
            skCircle(sketch, "E1.35.17.0", {"center": v(192.5, -93.5) * mm, "radius": 2.5 * mm});
            skCircle(sketch, "E1.35.18.0", {"center": v(192.5, -99) * mm, "radius": 2.5 * mm});
            skCircle(sketch, "E1.35.19.0", {"center": v(192.5, -104.5) * mm, "radius": 2.5 * mm});
            skCircle(sketch, "E1.35.20.0", {"center": v(192.5, -110) * mm, "radius": 2.5 * mm});
            skCircle(sketch, "E1.35.21.0", {"center": v(192.5, -115.5) * mm, "radius": 2.5 * mm});
            skCircle(sketch, "E1.35.22.0", {"center": v(192.5, -121) * mm, "radius": 2.5 * mm});
            skCircle(sketch, "E1.35.23.0", {"center": v(192.5, -126.5) * mm, "radius": 2.5 * mm});
            skCircle(sketch, "E1.35.24.0", {"center": v(192.5, -132) * mm, "radius": 2.5 * mm});
            skCircle(sketch, "E1.36.0.0", {"center": v(198, 0) * mm, "radius": 2.5 * mm});
            skCircle(sketch, "E1.36.1.0", {"center": v(198, -5.5) * mm, "radius": 2.5 * mm});
            skCircle(sketch, "E1.36.2.0", {"center": v(198, -11) * mm, "radius": 2.5 * mm});
            skCircle(sketch, "E1.36.3.0", {"center": v(198, -16.5) * mm, "radius": 2.5 * mm});
            skCircle(sketch, "E1.36.4.0", {"center": v(198, -22) * mm, "radius": 2.5 * mm});
            skCircle(sketch, "E1.36.5.0", {"center": v(198, -27.5) * mm, "radius": 2.5 * mm});
            skCircle(sketch, "E1.36.6.0", {"center": v(198, -33) * mm, "radius": 2.5 * mm});
            skCircle(sketch, "E1.36.7.0", {"center": v(198, -38.5) * mm, "radius": 2.5 * mm});
            skCircle(sketch, "E1.36.8.0", {"center": v(198, -44) * mm, "radius": 2.5 * mm});
            skCircle(sketch, "E1.36.9.0", {"center": v(198, -49.5) * mm, "radius": 2.5 * mm});
            skCircle(sketch, "E1.36.10.0", {"center": v(198, -55) * mm, "radius": 2.5 * mm});
            skCircle(sketch, "E1.36.11.0", {"center": v(198, -60.5) * mm, "radius": 2.5 * mm});
            skCircle(sketch, "E1.36.12.0", {"center": v(198, -66) * mm, "radius": 2.5 * mm});
            skCircle(sketch, "E1.36.13.0", {"center": v(198, -71.5) * mm, "radius": 2.5 * mm});
            skCircle(sketch, "E1.36.14.0", {"center": v(198, -77) * mm, "radius": 2.5 * mm});
            skCircle(sketch, "E1.36.15.0", {"center": v(198, -82.5) * mm, "radius": 2.5 * mm});
            skCircle(sketch, "E1.36.16.0", {"center": v(198, -88) * mm, "radius": 2.5 * mm});
            skCircle(sketch, "E1.36.17.0", {"center": v(198, -93.5) * mm, "radius": 2.5 * mm});
            skCircle(sketch, "E1.36.18.0", {"center": v(198, -99) * mm, "radius": 2.5 * mm});
            skCircle(sketch, "E1.36.19.0", {"center": v(198, -104.5) * mm, "radius": 2.5 * mm});
            skCircle(sketch, "E1.36.20.0", {"center": v(198, -110) * mm, "radius": 2.5 * mm});
            skCircle(sketch, "E1.36.21.0", {"center": v(198, -115.5) * mm, "radius": 2.5 * mm});
            skCircle(sketch, "E1.36.22.0", {"center": v(198, -121) * mm, "radius": 2.5 * mm});
            skCircle(sketch, "E1.36.23.0", {"center": v(198, -126.5) * mm, "radius": 2.5 * mm});
            skCircle(sketch, "E1.36.24.0", {"center": v(198, -132) * mm, "radius": 2.5 * mm});
            skCircle(sketch, "E1.37.0.0", {"center": v(203.5, 0) * mm, "radius": 2.5 * mm});
            skCircle(sketch, "E1.37.1.0", {"center": v(203.5, -5.5) * mm, "radius": 2.5 * mm});
            skCircle(sketch, "E1.37.2.0", {"center": v(203.5, -11) * mm, "radius": 2.5 * mm});
            skCircle(sketch, "E1.37.3.0", {"center": v(203.5, -16.5) * mm, "radius": 2.5 * mm});
            skCircle(sketch, "E1.37.4.0", {"center": v(203.5, -22) * mm, "radius": 2.5 * mm});
            skCircle(sketch, "E1.37.5.0", {"center": v(203.5, -27.5) * mm, "radius": 2.5 * mm});
            skCircle(sketch, "E1.37.6.0", {"center": v(203.5, -33) * mm, "radius": 2.5 * mm});
            skCircle(sketch, "E1.37.7.0", {"center": v(203.5, -38.5) * mm, "radius": 2.5 * mm});
            skCircle(sketch, "E1.37.8.0", {"center": v(203.5, -44) * mm, "radius": 2.5 * mm});
            skCircle(sketch, "E1.37.9.0", {"center": v(203.5, -49.5) * mm, "radius": 2.5 * mm});
            skCircle(sketch, "E1.37.10.0", {"center": v(203.5, -55) * mm, "radius": 2.5 * mm});
            skCircle(sketch, "E1.37.11.0", {"center": v(203.5, -60.5) * mm, "radius": 2.5 * mm});
            skCircle(sketch, "E1.37.12.0", {"center": v(203.5, -66) * mm, "radius": 2.5 * mm});
            skCircle(sketch, "E1.37.13.0", {"center": v(203.5, -71.5) * mm, "radius": 2.5 * mm});
            skCircle(sketch, "E1.37.14.0", {"center": v(203.5, -77) * mm, "radius": 2.5 * mm});
            skCircle(sketch, "E1.37.15.0", {"center": v(203.5, -82.5) * mm, "radius": 2.5 * mm});
            skCircle(sketch, "E1.37.16.0", {"center": v(203.5, -88) * mm, "radius": 2.5 * mm});
            skCircle(sketch, "E1.37.17.0", {"center": v(203.5, -93.5) * mm, "radius": 2.5 * mm});
            skCircle(sketch, "E1.37.18.0", {"center": v(203.5, -99) * mm, "radius": 2.5 * mm});
            skCircle(sketch, "E1.37.19.0", {"center": v(203.5, -104.5) * mm, "radius": 2.5 * mm});
            skCircle(sketch, "E1.37.20.0", {"center": v(203.5, -110) * mm, "radius": 2.5 * mm});
            skCircle(sketch, "E1.37.21.0", {"center": v(203.5, -115.5) * mm, "radius": 2.5 * mm});
            skCircle(sketch, "E1.37.22.0", {"center": v(203.5, -121) * mm, "radius": 2.5 * mm});
            skCircle(sketch, "E1.37.23.0", {"center": v(203.5, -126.5) * mm, "radius": 2.5 * mm});
            skCircle(sketch, "E1.37.24.0", {"center": v(203.5, -132) * mm, "radius": 2.5 * mm});
            skCircle(sketch, "E1.38.0.0", {"center": v(209, 0) * mm, "radius": 2.5 * mm});
            skCircle(sketch, "E1.38.1.0", {"center": v(209, -5.5) * mm, "radius": 2.5 * mm});
            skCircle(sketch, "E1.38.2.0", {"center": v(209, -11) * mm, "radius": 2.5 * mm});
            skCircle(sketch, "E1.38.3.0", {"center": v(209, -16.5) * mm, "radius": 2.5 * mm});
            skCircle(sketch, "E1.38.4.0", {"center": v(209, -22) * mm, "radius": 2.5 * mm});
            skCircle(sketch, "E1.38.5.0", {"center": v(209, -27.5) * mm, "radius": 2.5 * mm});
            skCircle(sketch, "E1.38.6.0", {"center": v(209, -33) * mm, "radius": 2.5 * mm});
            skCircle(sketch, "E1.38.7.0", {"center": v(209, -38.5) * mm, "radius": 2.5 * mm});
            skCircle(sketch, "E1.38.8.0", {"center": v(209, -44) * mm, "radius": 2.5 * mm});
            skCircle(sketch, "E1.38.9.0", {"center": v(209, -49.5) * mm, "radius": 2.5 * mm});
            skCircle(sketch, "E1.38.10.0", {"center": v(209, -55) * mm, "radius": 2.5 * mm});
            skCircle(sketch, "E1.38.11.0", {"center": v(209, -60.5) * mm, "radius": 2.5 * mm});
            skCircle(sketch, "E1.38.12.0", {"center": v(209, -66) * mm, "radius": 2.5 * mm});
            skCircle(sketch, "E1.38.13.0", {"center": v(209, -71.5) * mm, "radius": 2.5 * mm});
            skCircle(sketch, "E1.38.14.0", {"center": v(209, -77) * mm, "radius": 2.5 * mm});
            skCircle(sketch, "E1.38.15.0", {"center": v(209, -82.5) * mm, "radius": 2.5 * mm});
            skCircle(sketch, "E1.38.16.0", {"center": v(209, -88) * mm, "radius": 2.5 * mm});
            skCircle(sketch, "E1.38.17.0", {"center": v(209, -93.5) * mm, "radius": 2.5 * mm});
            skCircle(sketch, "E1.38.18.0", {"center": v(209, -99) * mm, "radius": 2.5 * mm});
            skCircle(sketch, "E1.38.19.0", {"center": v(209, -104.5) * mm, "radius": 2.5 * mm});
            skCircle(sketch, "E1.38.20.0", {"center": v(209, -110) * mm, "radius": 2.5 * mm});
            skCircle(sketch, "E1.38.21.0", {"center": v(209, -115.5) * mm, "radius": 2.5 * mm});
            skCircle(sketch, "E1.38.22.0", {"center": v(209, -121) * mm, "radius": 2.5 * mm});
            skCircle(sketch, "E1.38.23.0", {"center": v(209, -126.5) * mm, "radius": 2.5 * mm});
            skCircle(sketch, "E1.38.24.0", {"center": v(209, -132) * mm, "radius": 2.5 * mm});
            skCircle(sketch, "E1.39.0.0", {"center": v(214.5, 0) * mm, "radius": 2.5 * mm});
            skCircle(sketch, "E1.39.1.0", {"center": v(214.5, -5.5) * mm, "radius": 2.5 * mm});
            skCircle(sketch, "E1.39.2.0", {"center": v(214.5, -11) * mm, "radius": 2.5 * mm});
            skCircle(sketch, "E1.39.3.0", {"center": v(214.5, -16.5) * mm, "radius": 2.5 * mm});
            skCircle(sketch, "E1.39.4.0", {"center": v(214.5, -22) * mm, "radius": 2.5 * mm});
            skCircle(sketch, "E1.39.5.0", {"center": v(214.5, -27.5) * mm, "radius": 2.5 * mm});
            skCircle(sketch, "E1.39.6.0", {"center": v(214.5, -33) * mm, "radius": 2.5 * mm});
            skCircle(sketch, "E1.39.7.0", {"center": v(214.5, -38.5) * mm, "radius": 2.5 * mm});
            skCircle(sketch, "E1.39.8.0", {"center": v(214.5, -44) * mm, "radius": 2.5 * mm});
            skCircle(sketch, "E1.39.9.0", {"center": v(214.5, -49.5) * mm, "radius": 2.5 * mm});
            skCircle(sketch, "E1.39.10.0", {"center": v(214.5, -55) * mm, "radius": 2.5 * mm});
            skCircle(sketch, "E1.39.11.0", {"center": v(214.5, -60.5) * mm, "radius": 2.5 * mm});
            skCircle(sketch, "E1.39.12.0", {"center": v(214.5, -66) * mm, "radius": 2.5 * mm});
            skCircle(sketch, "E1.39.13.0", {"center": v(214.5, -71.5) * mm, "radius": 2.5 * mm});
            skCircle(sketch, "E1.39.14.0", {"center": v(214.5, -77) * mm, "radius": 2.5 * mm});
            skCircle(sketch, "E1.39.15.0", {"center": v(214.5, -82.5) * mm, "radius": 2.5 * mm});
            skCircle(sketch, "E1.39.16.0", {"center": v(214.5, -88) * mm, "radius": 2.5 * mm});
            skCircle(sketch, "E1.39.17.0", {"center": v(214.5, -93.5) * mm, "radius": 2.5 * mm});
            skCircle(sketch, "E1.39.18.0", {"center": v(214.5, -99) * mm, "radius": 2.5 * mm});
            skCircle(sketch, "E1.39.19.0", {"center": v(214.5, -104.5) * mm, "radius": 2.5 * mm});
            skCircle(sketch, "E1.39.20.0", {"center": v(214.5, -110) * mm, "radius": 2.5 * mm});
            skCircle(sketch, "E1.39.21.0", {"center": v(214.5, -115.5) * mm, "radius": 2.5 * mm});
            skCircle(sketch, "E1.39.22.0", {"center": v(214.5, -121) * mm, "radius": 2.5 * mm});
            skCircle(sketch, "E1.39.23.0", {"center": v(214.5, -126.5) * mm, "radius": 2.5 * mm});
            skCircle(sketch, "E1.39.24.0", {"center": v(214.5, -132) * mm, "radius": 2.5 * mm});
            skCircle(sketch, "E1.40.0.0", {"center": v(220, 0) * mm, "radius": 2.5 * mm});
            skCircle(sketch, "E1.40.1.0", {"center": v(220, -5.5) * mm, "radius": 2.5 * mm});
            skCircle(sketch, "E1.40.2.0", {"center": v(220, -11) * mm, "radius": 2.5 * mm});
            skCircle(sketch, "E1.40.3.0", {"center": v(220, -16.5) * mm, "radius": 2.5 * mm});
            skCircle(sketch, "E1.40.4.0", {"center": v(220, -22) * mm, "radius": 2.5 * mm});
            skCircle(sketch, "E1.40.5.0", {"center": v(220, -27.5) * mm, "radius": 2.5 * mm});
            skCircle(sketch, "E1.40.6.0", {"center": v(220, -33) * mm, "radius": 2.5 * mm});
            skCircle(sketch, "E1.40.7.0", {"center": v(220, -38.5) * mm, "radius": 2.5 * mm});
            skCircle(sketch, "E1.40.8.0", {"center": v(220, -44) * mm, "radius": 2.5 * mm});
            skCircle(sketch, "E1.40.9.0", {"center": v(220, -49.5) * mm, "radius": 2.5 * mm});
            skCircle(sketch, "E1.40.10.0", {"center": v(220, -55) * mm, "radius": 2.5 * mm});
            skCircle(sketch, "E1.40.11.0", {"center": v(220, -60.5) * mm, "radius": 2.5 * mm});
            skCircle(sketch, "E1.40.12.0", {"center": v(220, -66) * mm, "radius": 2.5 * mm});
            skCircle(sketch, "E1.40.13.0", {"center": v(220, -71.5) * mm, "radius": 2.5 * mm});
            skCircle(sketch, "E1.40.14.0", {"center": v(220, -77) * mm, "radius": 2.5 * mm});
            skCircle(sketch, "E1.40.15.0", {"center": v(220, -82.5) * mm, "radius": 2.5 * mm});
            skCircle(sketch, "E1.40.16.0", {"center": v(220, -88) * mm, "radius": 2.5 * mm});
            skCircle(sketch, "E1.40.17.0", {"center": v(220, -93.5) * mm, "radius": 2.5 * mm});
            skCircle(sketch, "E1.40.18.0", {"center": v(220, -99) * mm, "radius": 2.5 * mm});
            skCircle(sketch, "E1.40.19.0", {"center": v(220, -104.5) * mm, "radius": 2.5 * mm});
            skCircle(sketch, "E1.40.20.0", {"center": v(220, -110) * mm, "radius": 2.5 * mm});
            skCircle(sketch, "E1.40.21.0", {"center": v(220, -115.5) * mm, "radius": 2.5 * mm});
            skCircle(sketch, "E1.40.22.0", {"center": v(220, -121) * mm, "radius": 2.5 * mm});
            skCircle(sketch, "E1.40.23.0", {"center": v(220, -126.5) * mm, "radius": 2.5 * mm});
            skCircle(sketch, "E1.40.24.0", {"center": v(220, -132) * mm, "radius": 2.5 * mm});
            skCircle(sketch, "E1.41.0.0", {"center": v(225.5, 0) * mm, "radius": 2.5 * mm});
            skCircle(sketch, "E1.41.1.0", {"center": v(225.5, -5.5) * mm, "radius": 2.5 * mm});
            skCircle(sketch, "E1.41.2.0", {"center": v(225.5, -11) * mm, "radius": 2.5 * mm});
            skCircle(sketch, "E1.41.3.0", {"center": v(225.5, -16.5) * mm, "radius": 2.5 * mm});
            skCircle(sketch, "E1.41.4.0", {"center": v(225.5, -22) * mm, "radius": 2.5 * mm});
            skCircle(sketch, "E1.41.5.0", {"center": v(225.5, -27.5) * mm, "radius": 2.5 * mm});
            skCircle(sketch, "E1.41.6.0", {"center": v(225.5, -33) * mm, "radius": 2.5 * mm});
            skCircle(sketch, "E1.41.7.0", {"center": v(225.5, -38.5) * mm, "radius": 2.5 * mm});
            skCircle(sketch, "E1.41.8.0", {"center": v(225.5, -44) * mm, "radius": 2.5 * mm});
            skCircle(sketch, "E1.41.9.0", {"center": v(225.5, -49.5) * mm, "radius": 2.5 * mm});
            skCircle(sketch, "E1.41.10.0", {"center": v(225.5, -55) * mm, "radius": 2.5 * mm});
            skCircle(sketch, "E1.41.11.0", {"center": v(225.5, -60.5) * mm, "radius": 2.5 * mm});
            skCircle(sketch, "E1.41.12.0", {"center": v(225.5, -66) * mm, "radius": 2.5 * mm});
            skCircle(sketch, "E1.41.13.0", {"center": v(225.5, -71.5) * mm, "radius": 2.5 * mm});
            skCircle(sketch, "E1.41.14.0", {"center": v(225.5, -77) * mm, "radius": 2.5 * mm});
            skCircle(sketch, "E1.41.15.0", {"center": v(225.5, -82.5) * mm, "radius": 2.5 * mm});
            skCircle(sketch, "E1.41.16.0", {"center": v(225.5, -88) * mm, "radius": 2.5 * mm});
            skCircle(sketch, "E1.41.17.0", {"center": v(225.5, -93.5) * mm, "radius": 2.5 * mm});
            skCircle(sketch, "E1.41.18.0", {"center": v(225.5, -99) * mm, "radius": 2.5 * mm});
            skCircle(sketch, "E1.41.19.0", {"center": v(225.5, -104.5) * mm, "radius": 2.5 * mm});
            skCircle(sketch, "E1.41.20.0", {"center": v(225.5, -110) * mm, "radius": 2.5 * mm});
            skCircle(sketch, "E1.41.21.0", {"center": v(225.5, -115.5) * mm, "radius": 2.5 * mm});
            skCircle(sketch, "E1.41.22.0", {"center": v(225.5, -121) * mm, "radius": 2.5 * mm});
            skCircle(sketch, "E1.41.23.0", {"center": v(225.5, -126.5) * mm, "radius": 2.5 * mm});
            skCircle(sketch, "E1.41.24.0", {"center": v(225.5, -132) * mm, "radius": 2.5 * mm});
            skCircle(sketch, "E1.42.0.0", {"center": v(231, 0) * mm, "radius": 2.5 * mm});
            skCircle(sketch, "E1.42.1.0", {"center": v(231, -5.5) * mm, "radius": 2.5 * mm});
            skCircle(sketch, "E1.42.2.0", {"center": v(231, -11) * mm, "radius": 2.5 * mm});
            skCircle(sketch, "E1.42.3.0", {"center": v(231, -16.5) * mm, "radius": 2.5 * mm});
            skCircle(sketch, "E1.42.4.0", {"center": v(231, -22) * mm, "radius": 2.5 * mm});
            skCircle(sketch, "E1.42.5.0", {"center": v(231, -27.5) * mm, "radius": 2.5 * mm});
            skCircle(sketch, "E1.42.6.0", {"center": v(231, -33) * mm, "radius": 2.5 * mm});
            skCircle(sketch, "E1.42.7.0", {"center": v(231, -38.5) * mm, "radius": 2.5 * mm});
            skCircle(sketch, "E1.42.8.0", {"center": v(231, -44) * mm, "radius": 2.5 * mm});
            skCircle(sketch, "E1.42.9.0", {"center": v(231, -49.5) * mm, "radius": 2.5 * mm});
            skCircle(sketch, "E1.42.10.0", {"center": v(231, -55) * mm, "radius": 2.5 * mm});
            skCircle(sketch, "E1.42.11.0", {"center": v(231, -60.5) * mm, "radius": 2.5 * mm});
            skCircle(sketch, "E1.42.12.0", {"center": v(231, -66) * mm, "radius": 2.5 * mm});
            skCircle(sketch, "E1.42.13.0", {"center": v(231, -71.5) * mm, "radius": 2.5 * mm});
            skCircle(sketch, "E1.42.14.0", {"center": v(231, -77) * mm, "radius": 2.5 * mm});
            skCircle(sketch, "E1.42.15.0", {"center": v(231, -82.5) * mm, "radius": 2.5 * mm});
            skCircle(sketch, "E1.42.16.0", {"center": v(231, -88) * mm, "radius": 2.5 * mm});
            skCircle(sketch, "E1.42.17.0", {"center": v(231, -93.5) * mm, "radius": 2.5 * mm});
            skCircle(sketch, "E1.42.18.0", {"center": v(231, -99) * mm, "radius": 2.5 * mm});
            skCircle(sketch, "E1.42.19.0", {"center": v(231, -104.5) * mm, "radius": 2.5 * mm});
            skCircle(sketch, "E1.42.20.0", {"center": v(231, -110) * mm, "radius": 2.5 * mm});
            skCircle(sketch, "E1.42.21.0", {"center": v(231, -115.5) * mm, "radius": 2.5 * mm});
            skCircle(sketch, "E1.42.22.0", {"center": v(231, -121) * mm, "radius": 2.5 * mm});
            skCircle(sketch, "E1.42.23.0", {"center": v(231, -126.5) * mm, "radius": 2.5 * mm});
            skCircle(sketch, "E1.42.24.0", {"center": v(231, -132) * mm, "radius": 2.5 * mm});
            skCircle(sketch, "E1.43.0.0", {"center": v(236.5, 0) * mm, "radius": 2.5 * mm});
            skCircle(sketch, "E1.43.1.0", {"center": v(236.5, -5.5) * mm, "radius": 2.5 * mm});
            skCircle(sketch, "E1.43.2.0", {"center": v(236.5, -11) * mm, "radius": 2.5 * mm});
            skCircle(sketch, "E1.43.3.0", {"center": v(236.5, -16.5) * mm, "radius": 2.5 * mm});
            skCircle(sketch, "E1.43.4.0", {"center": v(236.5, -22) * mm, "radius": 2.5 * mm});
            skCircle(sketch, "E1.43.5.0", {"center": v(236.5, -27.5) * mm, "radius": 2.5 * mm});
            skCircle(sketch, "E1.43.6.0", {"center": v(236.5, -33) * mm, "radius": 2.5 * mm});
            skCircle(sketch, "E1.43.7.0", {"center": v(236.5, -38.5) * mm, "radius": 2.5 * mm});
            skCircle(sketch, "E1.43.8.0", {"center": v(236.5, -44) * mm, "radius": 2.5 * mm});
            skCircle(sketch, "E1.43.9.0", {"center": v(236.5, -49.5) * mm, "radius": 2.5 * mm});
            skCircle(sketch, "E1.43.10.0", {"center": v(236.5, -55) * mm, "radius": 2.5 * mm});
            skCircle(sketch, "E1.43.11.0", {"center": v(236.5, -60.5) * mm, "radius": 2.5 * mm});
            skCircle(sketch, "E1.43.12.0", {"center": v(236.5, -66) * mm, "radius": 2.5 * mm});
            skCircle(sketch, "E1.43.13.0", {"center": v(236.5, -71.5) * mm, "radius": 2.5 * mm});
            skCircle(sketch, "E1.43.14.0", {"center": v(236.5, -77) * mm, "radius": 2.5 * mm});
            skCircle(sketch, "E1.43.15.0", {"center": v(236.5, -82.5) * mm, "radius": 2.5 * mm});
            skCircle(sketch, "E1.43.16.0", {"center": v(236.5, -88) * mm, "radius": 2.5 * mm});
            skCircle(sketch, "E1.43.17.0", {"center": v(236.5, -93.5) * mm, "radius": 2.5 * mm});
            skCircle(sketch, "E1.43.18.0", {"center": v(236.5, -99) * mm, "radius": 2.5 * mm});
            skCircle(sketch, "E1.43.19.0", {"center": v(236.5, -104.5) * mm, "radius": 2.5 * mm});
            skCircle(sketch, "E1.43.20.0", {"center": v(236.5, -110) * mm, "radius": 2.5 * mm});
            skCircle(sketch, "E1.43.21.0", {"center": v(236.5, -115.5) * mm, "radius": 2.5 * mm});
            skCircle(sketch, "E1.43.22.0", {"center": v(236.5, -121) * mm, "radius": 2.5 * mm});
            skCircle(sketch, "E1.43.23.0", {"center": v(236.5, -126.5) * mm, "radius": 2.5 * mm});
            skCircle(sketch, "E1.43.24.0", {"center": v(236.5, -132) * mm, "radius": 2.5 * mm});
            skCircle(sketch, "E1.44.0.0", {"center": v(242, 0) * mm, "radius": 2.5 * mm});
            skCircle(sketch, "E1.44.1.0", {"center": v(242, -5.5) * mm, "radius": 2.5 * mm});
            skCircle(sketch, "E1.44.2.0", {"center": v(242, -11) * mm, "radius": 2.5 * mm});
            skCircle(sketch, "E1.44.3.0", {"center": v(242, -16.5) * mm, "radius": 2.5 * mm});
            skCircle(sketch, "E1.44.4.0", {"center": v(242, -22) * mm, "radius": 2.5 * mm});
            skCircle(sketch, "E1.44.5.0", {"center": v(242, -27.5) * mm, "radius": 2.5 * mm});
            skCircle(sketch, "E1.44.6.0", {"center": v(242, -33) * mm, "radius": 2.5 * mm});
            skCircle(sketch, "E1.44.7.0", {"center": v(242, -38.5) * mm, "radius": 2.5 * mm});
            skCircle(sketch, "E1.44.8.0", {"center": v(242, -44) * mm, "radius": 2.5 * mm});
            skCircle(sketch, "E1.44.9.0", {"center": v(242, -49.5) * mm, "radius": 2.5 * mm});
            skCircle(sketch, "E1.44.10.0", {"center": v(242, -55) * mm, "radius": 2.5 * mm});
            skCircle(sketch, "E1.44.11.0", {"center": v(242, -60.5) * mm, "radius": 2.5 * mm});
            skCircle(sketch, "E1.44.12.0", {"center": v(242, -66) * mm, "radius": 2.5 * mm});
            skCircle(sketch, "E1.44.13.0", {"center": v(242, -71.5) * mm, "radius": 2.5 * mm});
            skCircle(sketch, "E1.44.14.0", {"center": v(242, -77) * mm, "radius": 2.5 * mm});
            skCircle(sketch, "E1.44.15.0", {"center": v(242, -82.5) * mm, "radius": 2.5 * mm});
            skCircle(sketch, "E1.44.16.0", {"center": v(242, -88) * mm, "radius": 2.5 * mm});
            skCircle(sketch, "E1.44.17.0", {"center": v(242, -93.5) * mm, "radius": 2.5 * mm});
            skCircle(sketch, "E1.44.18.0", {"center": v(242, -99) * mm, "radius": 2.5 * mm});
            skCircle(sketch, "E1.44.19.0", {"center": v(242, -104.5) * mm, "radius": 2.5 * mm});
            skCircle(sketch, "E1.44.20.0", {"center": v(242, -110) * mm, "radius": 2.5 * mm});
            skCircle(sketch, "E1.44.21.0", {"center": v(242, -115.5) * mm, "radius": 2.5 * mm});
            skCircle(sketch, "E1.44.22.0", {"center": v(242, -121) * mm, "radius": 2.5 * mm});
            skCircle(sketch, "E1.44.23.0", {"center": v(242, -126.5) * mm, "radius": 2.5 * mm});
            skCircle(sketch, "E1.44.24.0", {"center": v(242, -132) * mm, "radius": 2.5 * mm});
            skCircle(sketch, "E1.45.0.0", {"center": v(247.5, 0) * mm, "radius": 2.5 * mm});
            skCircle(sketch, "E1.45.1.0", {"center": v(247.5, -5.5) * mm, "radius": 2.5 * mm});
            skCircle(sketch, "E1.45.2.0", {"center": v(247.5, -11) * mm, "radius": 2.5 * mm});
            skCircle(sketch, "E1.45.3.0", {"center": v(247.5, -16.5) * mm, "radius": 2.5 * mm});
            skCircle(sketch, "E1.45.4.0", {"center": v(247.5, -22) * mm, "radius": 2.5 * mm});
            skCircle(sketch, "E1.45.5.0", {"center": v(247.5, -27.5) * mm, "radius": 2.5 * mm});
            skCircle(sketch, "E1.45.6.0", {"center": v(247.5, -33) * mm, "radius": 2.5 * mm});
            skCircle(sketch, "E1.45.7.0", {"center": v(247.5, -38.5) * mm, "radius": 2.5 * mm});
            skCircle(sketch, "E1.45.8.0", {"center": v(247.5, -44) * mm, "radius": 2.5 * mm});
            skCircle(sketch, "E1.45.9.0", {"center": v(247.5, -49.5) * mm, "radius": 2.5 * mm});
            skCircle(sketch, "E1.45.10.0", {"center": v(247.5, -55) * mm, "radius": 2.5 * mm});
            skCircle(sketch, "E1.45.11.0", {"center": v(247.5, -60.5) * mm, "radius": 2.5 * mm});
            skCircle(sketch, "E1.45.12.0", {"center": v(247.5, -66) * mm, "radius": 2.5 * mm});
            skCircle(sketch, "E1.45.13.0", {"center": v(247.5, -71.5) * mm, "radius": 2.5 * mm});
            skCircle(sketch, "E1.45.14.0", {"center": v(247.5, -77) * mm, "radius": 2.5 * mm});
            skCircle(sketch, "E1.45.15.0", {"center": v(247.5, -82.5) * mm, "radius": 2.5 * mm});
            skCircle(sketch, "E1.45.16.0", {"center": v(247.5, -88) * mm, "radius": 2.5 * mm});
            skCircle(sketch, "E1.45.17.0", {"center": v(247.5, -93.5) * mm, "radius": 2.5 * mm});
            skCircle(sketch, "E1.45.18.0", {"center": v(247.5, -99) * mm, "radius": 2.5 * mm});
            skCircle(sketch, "E1.45.19.0", {"center": v(247.5, -104.5) * mm, "radius": 2.5 * mm});
            skCircle(sketch, "E1.45.20.0", {"center": v(247.5, -110) * mm, "radius": 2.5 * mm});
            skCircle(sketch, "E1.45.21.0", {"center": v(247.5, -115.5) * mm, "radius": 2.5 * mm});
            skCircle(sketch, "E1.45.22.0", {"center": v(247.5, -121) * mm, "radius": 2.5 * mm});
            skCircle(sketch, "E1.45.23.0", {"center": v(247.5, -126.5) * mm, "radius": 2.5 * mm});
            skCircle(sketch, "E1.45.24.0", {"center": v(247.5, -132) * mm, "radius": 2.5 * mm});
            skCircle(sketch, "E1.46.0.0", {"center": v(253, 0) * mm, "radius": 2.5 * mm});
            skCircle(sketch, "E1.46.1.0", {"center": v(253, -5.5) * mm, "radius": 2.5 * mm});
            skCircle(sketch, "E1.46.2.0", {"center": v(253, -11) * mm, "radius": 2.5 * mm});
            skCircle(sketch, "E1.46.3.0", {"center": v(253, -16.5) * mm, "radius": 2.5 * mm});
            skCircle(sketch, "E1.46.4.0", {"center": v(253, -22) * mm, "radius": 2.5 * mm});
            skCircle(sketch, "E1.46.5.0", {"center": v(253, -27.5) * mm, "radius": 2.5 * mm});
            skCircle(sketch, "E1.46.6.0", {"center": v(253, -33) * mm, "radius": 2.5 * mm});
            skCircle(sketch, "E1.46.7.0", {"center": v(253, -38.5) * mm, "radius": 2.5 * mm});
            skCircle(sketch, "E1.46.8.0", {"center": v(253, -44) * mm, "radius": 2.5 * mm});
            skCircle(sketch, "E1.46.9.0", {"center": v(253, -49.5) * mm, "radius": 2.5 * mm});
            skCircle(sketch, "E1.46.10.0", {"center": v(253, -55) * mm, "radius": 2.5 * mm});
            skCircle(sketch, "E1.46.11.0", {"center": v(253, -60.5) * mm, "radius": 2.5 * mm});
            skCircle(sketch, "E1.46.12.0", {"center": v(253, -66) * mm, "radius": 2.5 * mm});
            skCircle(sketch, "E1.46.13.0", {"center": v(253, -71.5) * mm, "radius": 2.5 * mm});
            skCircle(sketch, "E1.46.14.0", {"center": v(253, -77) * mm, "radius": 2.5 * mm});
            skCircle(sketch, "E1.46.15.0", {"center": v(253, -82.5) * mm, "radius": 2.5 * mm});
            skCircle(sketch, "E1.46.16.0", {"center": v(253, -88) * mm, "radius": 2.5 * mm});
            skCircle(sketch, "E1.46.17.0", {"center": v(253, -93.5) * mm, "radius": 2.5 * mm});
            skCircle(sketch, "E1.46.18.0", {"center": v(253, -99) * mm, "radius": 2.5 * mm});
            skCircle(sketch, "E1.46.19.0", {"center": v(253, -104.5) * mm, "radius": 2.5 * mm});
            skCircle(sketch, "E1.46.20.0", {"center": v(253, -110) * mm, "radius": 2.5 * mm});
            skCircle(sketch, "E1.46.21.0", {"center": v(253, -115.5) * mm, "radius": 2.5 * mm});
            skCircle(sketch, "E1.46.22.0", {"center": v(253, -121) * mm, "radius": 2.5 * mm});
            skCircle(sketch, "E1.46.23.0", {"center": v(253, -126.5) * mm, "radius": 2.5 * mm});
            skCircle(sketch, "E1.46.24.0", {"center": v(253, -132) * mm, "radius": 2.5 * mm});
            skCircle(sketch, "E1.47.0.0", {"center": v(258.5, 0) * mm, "radius": 2.5 * mm});
            skCircle(sketch, "E1.47.1.0", {"center": v(258.5, -5.5) * mm, "radius": 2.5 * mm});
            skCircle(sketch, "E1.47.2.0", {"center": v(258.5, -11) * mm, "radius": 2.5 * mm});
            skCircle(sketch, "E1.47.3.0", {"center": v(258.5, -16.5) * mm, "radius": 2.5 * mm});
            skCircle(sketch, "E1.47.4.0", {"center": v(258.5, -22) * mm, "radius": 2.5 * mm});
            skCircle(sketch, "E1.47.5.0", {"center": v(258.5, -27.5) * mm, "radius": 2.5 * mm});
            skCircle(sketch, "E1.47.6.0", {"center": v(258.5, -33) * mm, "radius": 2.5 * mm});
            skCircle(sketch, "E1.47.7.0", {"center": v(258.5, -38.5) * mm, "radius": 2.5 * mm});
            skCircle(sketch, "E1.47.8.0", {"center": v(258.5, -44) * mm, "radius": 2.5 * mm});
            skCircle(sketch, "E1.47.9.0", {"center": v(258.5, -49.5) * mm, "radius": 2.5 * mm});
            skCircle(sketch, "E1.47.10.0", {"center": v(258.5, -55) * mm, "radius": 2.5 * mm});
            skCircle(sketch, "E1.47.11.0", {"center": v(258.5, -60.5) * mm, "radius": 2.5 * mm});
            skCircle(sketch, "E1.47.12.0", {"center": v(258.5, -66) * mm, "radius": 2.5 * mm});
            skCircle(sketch, "E1.47.13.0", {"center": v(258.5, -71.5) * mm, "radius": 2.5 * mm});
            skCircle(sketch, "E1.47.14.0", {"center": v(258.5, -77) * mm, "radius": 2.5 * mm});
            skCircle(sketch, "E1.47.15.0", {"center": v(258.5, -82.5) * mm, "radius": 2.5 * mm});
            skCircle(sketch, "E1.47.16.0", {"center": v(258.5, -88) * mm, "radius": 2.5 * mm});
            skCircle(sketch, "E1.47.17.0", {"center": v(258.5, -93.5) * mm, "radius": 2.5 * mm});
            skCircle(sketch, "E1.47.18.0", {"center": v(258.5, -99) * mm, "radius": 2.5 * mm});
            skCircle(sketch, "E1.47.19.0", {"center": v(258.5, -104.5) * mm, "radius": 2.5 * mm});
            skCircle(sketch, "E1.47.20.0", {"center": v(258.5, -110) * mm, "radius": 2.5 * mm});
            skCircle(sketch, "E1.47.21.0", {"center": v(258.5, -115.5) * mm, "radius": 2.5 * mm});
            skCircle(sketch, "E1.47.22.0", {"center": v(258.5, -121) * mm, "radius": 2.5 * mm});
            skCircle(sketch, "E1.47.23.0", {"center": v(258.5, -126.5) * mm, "radius": 2.5 * mm});
            skCircle(sketch, "E1.47.24.0", {"center": v(258.5, -132) * mm, "radius": 2.5 * mm});
            skCircle(sketch, "E1.48.0.0", {"center": v(264, 0) * mm, "radius": 2.5 * mm});
            skCircle(sketch, "E1.48.1.0", {"center": v(264, -5.5) * mm, "radius": 2.5 * mm});
            skCircle(sketch, "E1.48.2.0", {"center": v(264, -11) * mm, "radius": 2.5 * mm});
            skCircle(sketch, "E1.48.3.0", {"center": v(264, -16.5) * mm, "radius": 2.5 * mm});
            skCircle(sketch, "E1.48.4.0", {"center": v(264, -22) * mm, "radius": 2.5 * mm});
            skCircle(sketch, "E1.48.5.0", {"center": v(264, -27.5) * mm, "radius": 2.5 * mm});
            skCircle(sketch, "E1.48.6.0", {"center": v(264, -33) * mm, "radius": 2.5 * mm});
            skCircle(sketch, "E1.48.7.0", {"center": v(264, -38.5) * mm, "radius": 2.5 * mm});
            skCircle(sketch, "E1.48.8.0", {"center": v(264, -44) * mm, "radius": 2.5 * mm});
            skCircle(sketch, "E1.48.9.0", {"center": v(264, -49.5) * mm, "radius": 2.5 * mm});
            skCircle(sketch, "E1.48.10.0", {"center": v(264, -55) * mm, "radius": 2.5 * mm});
            skCircle(sketch, "E1.48.11.0", {"center": v(264, -60.5) * mm, "radius": 2.5 * mm});
            skCircle(sketch, "E1.48.12.0", {"center": v(264, -66) * mm, "radius": 2.5 * mm});
            skCircle(sketch, "E1.48.13.0", {"center": v(264, -71.5) * mm, "radius": 2.5 * mm});
            skCircle(sketch, "E1.48.14.0", {"center": v(264, -77) * mm, "radius": 2.5 * mm});
            skCircle(sketch, "E1.48.15.0", {"center": v(264, -82.5) * mm, "radius": 2.5 * mm});
            skCircle(sketch, "E1.48.16.0", {"center": v(264, -88) * mm, "radius": 2.5 * mm});
            skCircle(sketch, "E1.48.17.0", {"center": v(264, -93.5) * mm, "radius": 2.5 * mm});
            skCircle(sketch, "E1.48.18.0", {"center": v(264, -99) * mm, "radius": 2.5 * mm});
            skCircle(sketch, "E1.48.19.0", {"center": v(264, -104.5) * mm, "radius": 2.5 * mm});
            skCircle(sketch, "E1.48.20.0", {"center": v(264, -110) * mm, "radius": 2.5 * mm});
            skCircle(sketch, "E1.48.21.0", {"center": v(264, -115.5) * mm, "radius": 2.5 * mm});
            skCircle(sketch, "E1.48.22.0", {"center": v(264, -121) * mm, "radius": 2.5 * mm});
            skCircle(sketch, "E1.48.23.0", {"center": v(264, -126.5) * mm, "radius": 2.5 * mm});
            skCircle(sketch, "E1.48.24.0", {"center": v(264, -132) * mm, "radius": 2.5 * mm});
            skCircle(sketch, "E1.49.0.0", {"center": v(269.5, 0) * mm, "radius": 2.5 * mm});
            skCircle(sketch, "E1.49.1.0", {"center": v(269.5, -5.5) * mm, "radius": 2.5 * mm});
            skCircle(sketch, "E1.49.2.0", {"center": v(269.5, -11) * mm, "radius": 2.5 * mm});
            skCircle(sketch, "E1.49.3.0", {"center": v(269.5, -16.5) * mm, "radius": 2.5 * mm});
            skCircle(sketch, "E1.49.4.0", {"center": v(269.5, -22) * mm, "radius": 2.5 * mm});
            skCircle(sketch, "E1.49.5.0", {"center": v(269.5, -27.5) * mm, "radius": 2.5 * mm});
            skCircle(sketch, "E1.49.6.0", {"center": v(269.5, -33) * mm, "radius": 2.5 * mm});
            skCircle(sketch, "E1.49.7.0", {"center": v(269.5, -38.5) * mm, "radius": 2.5 * mm});
            skCircle(sketch, "E1.49.8.0", {"center": v(269.5, -44) * mm, "radius": 2.5 * mm});
            skCircle(sketch, "E1.49.9.0", {"center": v(269.5, -49.5) * mm, "radius": 2.5 * mm});
            skCircle(sketch, "E1.49.10.0", {"center": v(269.5, -55) * mm, "radius": 2.5 * mm});
            skCircle(sketch, "E1.49.11.0", {"center": v(269.5, -60.5) * mm, "radius": 2.5 * mm});
            skCircle(sketch, "E1.49.12.0", {"center": v(269.5, -66) * mm, "radius": 2.5 * mm});
            skCircle(sketch, "E1.49.13.0", {"center": v(269.5, -71.5) * mm, "radius": 2.5 * mm});
            skCircle(sketch, "E1.49.14.0", {"center": v(269.5, -77) * mm, "radius": 2.5 * mm});
            skCircle(sketch, "E1.49.15.0", {"center": v(269.5, -82.5) * mm, "radius": 2.5 * mm});
            skCircle(sketch, "E1.49.16.0", {"center": v(269.5, -88) * mm, "radius": 2.5 * mm});
            skCircle(sketch, "E1.49.17.0", {"center": v(269.5, -93.5) * mm, "radius": 2.5 * mm});
            skCircle(sketch, "E1.49.18.0", {"center": v(269.5, -99) * mm, "radius": 2.5 * mm});
            skCircle(sketch, "E1.49.19.0", {"center": v(269.5, -104.5) * mm, "radius": 2.5 * mm});
            skCircle(sketch, "E1.49.20.0", {"center": v(269.5, -110) * mm, "radius": 2.5 * mm});
            skCircle(sketch, "E1.49.21.0", {"center": v(269.5, -115.5) * mm, "radius": 2.5 * mm});
            skCircle(sketch, "E1.49.22.0", {"center": v(269.5, -121) * mm, "radius": 2.5 * mm});
            skCircle(sketch, "E1.49.23.0", {"center": v(269.5, -126.5) * mm, "radius": 2.5 * mm});
            skCircle(sketch, "E1.49.24.0", {"center": v(269.5, -132) * mm, "radius": 2.5 * mm});
            skCircle(sketch, "E1.50.0.0", {"center": v(275, 0) * mm, "radius": 2.5 * mm});
            skCircle(sketch, "E1.50.1.0", {"center": v(275, -5.5) * mm, "radius": 2.5 * mm});
            skCircle(sketch, "E1.50.2.0", {"center": v(275, -11) * mm, "radius": 2.5 * mm});
            skCircle(sketch, "E1.50.3.0", {"center": v(275, -16.5) * mm, "radius": 2.5 * mm});
            skCircle(sketch, "E1.50.4.0", {"center": v(275, -22) * mm, "radius": 2.5 * mm});
            skCircle(sketch, "E1.50.5.0", {"center": v(275, -27.5) * mm, "radius": 2.5 * mm});
            skCircle(sketch, "E1.50.6.0", {"center": v(275, -33) * mm, "radius": 2.5 * mm});
            skCircle(sketch, "E1.50.7.0", {"center": v(275, -38.5) * mm, "radius": 2.5 * mm});
            skCircle(sketch, "E1.50.8.0", {"center": v(275, -44) * mm, "radius": 2.5 * mm});
            skCircle(sketch, "E1.50.9.0", {"center": v(275, -49.5) * mm, "radius": 2.5 * mm});
            skCircle(sketch, "E1.50.10.0", {"center": v(275, -55) * mm, "radius": 2.5 * mm});
            skCircle(sketch, "E1.50.11.0", {"center": v(275, -60.5) * mm, "radius": 2.5 * mm});
            skCircle(sketch, "E1.50.12.0", {"center": v(275, -66) * mm, "radius": 2.5 * mm});
            skCircle(sketch, "E1.50.13.0", {"center": v(275, -71.5) * mm, "radius": 2.5 * mm});
            skCircle(sketch, "E1.50.14.0", {"center": v(275, -77) * mm, "radius": 2.5 * mm});
            skCircle(sketch, "E1.50.15.0", {"center": v(275, -82.5) * mm, "radius": 2.5 * mm});
            skCircle(sketch, "E1.50.16.0", {"center": v(275, -88) * mm, "radius": 2.5 * mm});
            skCircle(sketch, "E1.50.17.0", {"center": v(275, -93.5) * mm, "radius": 2.5 * mm});
            skCircle(sketch, "E1.50.18.0", {"center": v(275, -99) * mm, "radius": 2.5 * mm});
            skCircle(sketch, "E1.50.19.0", {"center": v(275, -104.5) * mm, "radius": 2.5 * mm});
            skCircle(sketch, "E1.50.20.0", {"center": v(275, -110) * mm, "radius": 2.5 * mm});
            skCircle(sketch, "E1.50.21.0", {"center": v(275, -115.5) * mm, "radius": 2.5 * mm});
            skCircle(sketch, "E1.50.22.0", {"center": v(275, -121) * mm, "radius": 2.5 * mm});
            skCircle(sketch, "E1.50.23.0", {"center": v(275, -126.5) * mm, "radius": 2.5 * mm});
            skCircle(sketch, "E1.50.24.0", {"center": v(275, -132) * mm, "radius": 2.5 * mm});
            skCircle(sketch, "E1.51.0.0", {"center": v(280.5, 0) * mm, "radius": 2.5 * mm});
            skCircle(sketch, "E1.51.1.0", {"center": v(280.5, -5.5) * mm, "radius": 2.5 * mm});
            skCircle(sketch, "E1.51.2.0", {"center": v(280.5, -11) * mm, "radius": 2.5 * mm});
            skCircle(sketch, "E1.51.3.0", {"center": v(280.5, -16.5) * mm, "radius": 2.5 * mm});
            skCircle(sketch, "E1.51.4.0", {"center": v(280.5, -22) * mm, "radius": 2.5 * mm});
            skCircle(sketch, "E1.51.5.0", {"center": v(280.5, -27.5) * mm, "radius": 2.5 * mm});
            skCircle(sketch, "E1.51.6.0", {"center": v(280.5, -33) * mm, "radius": 2.5 * mm});
            skCircle(sketch, "E1.51.7.0", {"center": v(280.5, -38.5) * mm, "radius": 2.5 * mm});
            skCircle(sketch, "E1.51.8.0", {"center": v(280.5, -44) * mm, "radius": 2.5 * mm});
            skCircle(sketch, "E1.51.9.0", {"center": v(280.5, -49.5) * mm, "radius": 2.5 * mm});
            skCircle(sketch, "E1.51.10.0", {"center": v(280.5, -55) * mm, "radius": 2.5 * mm});
            skCircle(sketch, "E1.51.11.0", {"center": v(280.5, -60.5) * mm, "radius": 2.5 * mm});
            skCircle(sketch, "E1.51.12.0", {"center": v(280.5, -66) * mm, "radius": 2.5 * mm});
            skCircle(sketch, "E1.51.13.0", {"center": v(280.5, -71.5) * mm, "radius": 2.5 * mm});
            skCircle(sketch, "E1.51.14.0", {"center": v(280.5, -77) * mm, "radius": 2.5 * mm});
            skCircle(sketch, "E1.51.15.0", {"center": v(280.5, -82.5) * mm, "radius": 2.5 * mm});
            skCircle(sketch, "E1.51.16.0", {"center": v(280.5, -88) * mm, "radius": 2.5 * mm});
            skCircle(sketch, "E1.51.17.0", {"center": v(280.5, -93.5) * mm, "radius": 2.5 * mm});
            skCircle(sketch, "E1.51.18.0", {"center": v(280.5, -99) * mm, "radius": 2.5 * mm});
            skCircle(sketch, "E1.51.19.0", {"center": v(280.5, -104.5) * mm, "radius": 2.5 * mm});
            skCircle(sketch, "E1.51.20.0", {"center": v(280.5, -110) * mm, "radius": 2.5 * mm});
            skCircle(sketch, "E1.51.21.0", {"center": v(280.5, -115.5) * mm, "radius": 2.5 * mm});
            skCircle(sketch, "E1.51.22.0", {"center": v(280.5, -121) * mm, "radius": 2.5 * mm});
            skCircle(sketch, "E1.51.23.0", {"center": v(280.5, -126.5) * mm, "radius": 2.5 * mm});
            skCircle(sketch, "E1.51.24.0", {"center": v(280.5, -132) * mm, "radius": 2.5 * mm});
            skCircle(sketch, "E1.52.0.0", {"center": v(286, 0) * mm, "radius": 2.5 * mm});
            skCircle(sketch, "E1.52.1.0", {"center": v(286, -5.5) * mm, "radius": 2.5 * mm});
            skCircle(sketch, "E1.52.2.0", {"center": v(286, -11) * mm, "radius": 2.5 * mm});
            skCircle(sketch, "E1.52.3.0", {"center": v(286, -16.5) * mm, "radius": 2.5 * mm});
            skCircle(sketch, "E1.52.4.0", {"center": v(286, -22) * mm, "radius": 2.5 * mm});
            skCircle(sketch, "E1.52.5.0", {"center": v(286, -27.5) * mm, "radius": 2.5 * mm});
            skCircle(sketch, "E1.52.6.0", {"center": v(286, -33) * mm, "radius": 2.5 * mm});
            skCircle(sketch, "E1.52.7.0", {"center": v(286, -38.5) * mm, "radius": 2.5 * mm});
            skCircle(sketch, "E1.52.8.0", {"center": v(286, -44) * mm, "radius": 2.5 * mm});
            skCircle(sketch, "E1.52.9.0", {"center": v(286, -49.5) * mm, "radius": 2.5 * mm});
            skCircle(sketch, "E1.52.10.0", {"center": v(286, -55) * mm, "radius": 2.5 * mm});
            skCircle(sketch, "E1.52.11.0", {"center": v(286, -60.5) * mm, "radius": 2.5 * mm});
            skCircle(sketch, "E1.52.12.0", {"center": v(286, -66) * mm, "radius": 2.5 * mm});
            skCircle(sketch, "E1.52.13.0", {"center": v(286, -71.5) * mm, "radius": 2.5 * mm});
            skCircle(sketch, "E1.52.14.0", {"center": v(286, -77) * mm, "radius": 2.5 * mm});
            skCircle(sketch, "E1.52.15.0", {"center": v(286, -82.5) * mm, "radius": 2.5 * mm});
            skCircle(sketch, "E1.52.16.0", {"center": v(286, -88) * mm, "radius": 2.5 * mm});
            skCircle(sketch, "E1.52.17.0", {"center": v(286, -93.5) * mm, "radius": 2.5 * mm});
            skCircle(sketch, "E1.52.18.0", {"center": v(286, -99) * mm, "radius": 2.5 * mm});
            skCircle(sketch, "E1.52.19.0", {"center": v(286, -104.5) * mm, "radius": 2.5 * mm});
            skCircle(sketch, "E1.52.20.0", {"center": v(286, -110) * mm, "radius": 2.5 * mm});
            skCircle(sketch, "E1.52.21.0", {"center": v(286, -115.5) * mm, "radius": 2.5 * mm});
            skCircle(sketch, "E1.52.22.0", {"center": v(286, -121) * mm, "radius": 2.5 * mm});
            skCircle(sketch, "E1.52.23.0", {"center": v(286, -126.5) * mm, "radius": 2.5 * mm});
            skCircle(sketch, "E1.52.24.0", {"center": v(286, -132) * mm, "radius": 2.5 * mm});
            skCircle(sketch, "E1.53.0.0", {"center": v(291.5, 0) * mm, "radius": 2.5 * mm});
            skCircle(sketch, "E1.53.1.0", {"center": v(291.5, -5.5) * mm, "radius": 2.5 * mm});
            skCircle(sketch, "E1.53.2.0", {"center": v(291.5, -11) * mm, "radius": 2.5 * mm});
            skCircle(sketch, "E1.53.3.0", {"center": v(291.5, -16.5) * mm, "radius": 2.5 * mm});
            skCircle(sketch, "E1.53.4.0", {"center": v(291.5, -22) * mm, "radius": 2.5 * mm});
            skCircle(sketch, "E1.53.5.0", {"center": v(291.5, -27.5) * mm, "radius": 2.5 * mm});
            skCircle(sketch, "E1.53.6.0", {"center": v(291.5, -33) * mm, "radius": 2.5 * mm});
            skCircle(sketch, "E1.53.7.0", {"center": v(291.5, -38.5) * mm, "radius": 2.5 * mm});
            skCircle(sketch, "E1.53.8.0", {"center": v(291.5, -44) * mm, "radius": 2.5 * mm});
            skCircle(sketch, "E1.53.9.0", {"center": v(291.5, -49.5) * mm, "radius": 2.5 * mm});
            skCircle(sketch, "E1.53.10.0", {"center": v(291.5, -55) * mm, "radius": 2.5 * mm});
            skCircle(sketch, "E1.53.11.0", {"center": v(291.5, -60.5) * mm, "radius": 2.5 * mm});
            skCircle(sketch, "E1.53.12.0", {"center": v(291.5, -66) * mm, "radius": 2.5 * mm});
            skCircle(sketch, "E1.53.13.0", {"center": v(291.5, -71.5) * mm, "radius": 2.5 * mm});
            skCircle(sketch, "E1.53.14.0", {"center": v(291.5, -77) * mm, "radius": 2.5 * mm});
            skCircle(sketch, "E1.53.15.0", {"center": v(291.5, -82.5) * mm, "radius": 2.5 * mm});
            skCircle(sketch, "E1.53.16.0", {"center": v(291.5, -88) * mm, "radius": 2.5 * mm});
            skCircle(sketch, "E1.53.17.0", {"center": v(291.5, -93.5) * mm, "radius": 2.5 * mm});
            skCircle(sketch, "E1.53.18.0", {"center": v(291.5, -99) * mm, "radius": 2.5 * mm});
            skCircle(sketch, "E1.53.19.0", {"center": v(291.5, -104.5) * mm, "radius": 2.5 * mm});
            skCircle(sketch, "E1.53.20.0", {"center": v(291.5, -110) * mm, "radius": 2.5 * mm});
            skCircle(sketch, "E1.53.21.0", {"center": v(291.5, -115.5) * mm, "radius": 2.5 * mm});
            skCircle(sketch, "E1.53.22.0", {"center": v(291.5, -121) * mm, "radius": 2.5 * mm});
            skCircle(sketch, "E1.53.23.0", {"center": v(291.5, -126.5) * mm, "radius": 2.5 * mm});
            skCircle(sketch, "E1.53.24.0", {"center": v(291.5, -132) * mm, "radius": 2.5 * mm});
            skCircle(sketch, "E1.54.0.0", {"center": v(297, 0) * mm, "radius": 2.5 * mm});
            skCircle(sketch, "E1.54.1.0", {"center": v(297, -5.5) * mm, "radius": 2.5 * mm});
            skCircle(sketch, "E1.54.2.0", {"center": v(297, -11) * mm, "radius": 2.5 * mm});
            skCircle(sketch, "E1.54.3.0", {"center": v(297, -16.5) * mm, "radius": 2.5 * mm});
            skCircle(sketch, "E1.54.4.0", {"center": v(297, -22) * mm, "radius": 2.5 * mm});
            skCircle(sketch, "E1.54.5.0", {"center": v(297, -27.5) * mm, "radius": 2.5 * mm});
            skCircle(sketch, "E1.54.6.0", {"center": v(297, -33) * mm, "radius": 2.5 * mm});
            skCircle(sketch, "E1.54.7.0", {"center": v(297, -38.5) * mm, "radius": 2.5 * mm});
            skCircle(sketch, "E1.54.8.0", {"center": v(297, -44) * mm, "radius": 2.5 * mm});
            skCircle(sketch, "E1.54.9.0", {"center": v(297, -49.5) * mm, "radius": 2.5 * mm});
            skCircle(sketch, "E1.54.10.0", {"center": v(297, -55) * mm, "radius": 2.5 * mm});
            skCircle(sketch, "E1.54.11.0", {"center": v(297, -60.5) * mm, "radius": 2.5 * mm});
            skCircle(sketch, "E1.54.12.0", {"center": v(297, -66) * mm, "radius": 2.5 * mm});
            skCircle(sketch, "E1.54.13.0", {"center": v(297, -71.5) * mm, "radius": 2.5 * mm});
            skCircle(sketch, "E1.54.14.0", {"center": v(297, -77) * mm, "radius": 2.5 * mm});
            skCircle(sketch, "E1.54.15.0", {"center": v(297, -82.5) * mm, "radius": 2.5 * mm});
            skCircle(sketch, "E1.54.16.0", {"center": v(297, -88) * mm, "radius": 2.5 * mm});
            skCircle(sketch, "E1.54.17.0", {"center": v(297, -93.5) * mm, "radius": 2.5 * mm});
            skCircle(sketch, "E1.54.18.0", {"center": v(297, -99) * mm, "radius": 2.5 * mm});
            skCircle(sketch, "E1.54.19.0", {"center": v(297, -104.5) * mm, "radius": 2.5 * mm});
            skCircle(sketch, "E1.54.20.0", {"center": v(297, -110) * mm, "radius": 2.5 * mm});
            skCircle(sketch, "E1.54.21.0", {"center": v(297, -115.5) * mm, "radius": 2.5 * mm});
            skCircle(sketch, "E1.54.22.0", {"center": v(297, -121) * mm, "radius": 2.5 * mm});
            skCircle(sketch, "E1.54.23.0", {"center": v(297, -126.5) * mm, "radius": 2.5 * mm});
            skCircle(sketch, "E1.54.24.0", {"center": v(297, -132) * mm, "radius": 2.5 * mm});
            skCircle(sketch, "E1.55.0.0", {"center": v(302.5, 0) * mm, "radius": 2.5 * mm});
            skCircle(sketch, "E1.55.1.0", {"center": v(302.5, -5.5) * mm, "radius": 2.5 * mm});
            skCircle(sketch, "E1.55.2.0", {"center": v(302.5, -11) * mm, "radius": 2.5 * mm});
            skCircle(sketch, "E1.55.3.0", {"center": v(302.5, -16.5) * mm, "radius": 2.5 * mm});
            skCircle(sketch, "E1.55.4.0", {"center": v(302.5, -22) * mm, "radius": 2.5 * mm});
            skCircle(sketch, "E1.55.5.0", {"center": v(302.5, -27.5) * mm, "radius": 2.5 * mm});
            skCircle(sketch, "E1.55.6.0", {"center": v(302.5, -33) * mm, "radius": 2.5 * mm});
            skCircle(sketch, "E1.55.7.0", {"center": v(302.5, -38.5) * mm, "radius": 2.5 * mm});
            skCircle(sketch, "E1.55.8.0", {"center": v(302.5, -44) * mm, "radius": 2.5 * mm});
            skCircle(sketch, "E1.55.9.0", {"center": v(302.5, -49.5) * mm, "radius": 2.5 * mm});
            skCircle(sketch, "E1.55.10.0", {"center": v(302.5, -55) * mm, "radius": 2.5 * mm});
            skCircle(sketch, "E1.55.11.0", {"center": v(302.5, -60.5) * mm, "radius": 2.5 * mm});
            skCircle(sketch, "E1.55.12.0", {"center": v(302.5, -66) * mm, "radius": 2.5 * mm});
            skCircle(sketch, "E1.55.13.0", {"center": v(302.5, -71.5) * mm, "radius": 2.5 * mm});
            skCircle(sketch, "E1.55.14.0", {"center": v(302.5, -77) * mm, "radius": 2.5 * mm});
            skCircle(sketch, "E1.55.15.0", {"center": v(302.5, -82.5) * mm, "radius": 2.5 * mm});
            skCircle(sketch, "E1.55.16.0", {"center": v(302.5, -88) * mm, "radius": 2.5 * mm});
            skCircle(sketch, "E1.55.17.0", {"center": v(302.5, -93.5) * mm, "radius": 2.5 * mm});
            skCircle(sketch, "E1.55.18.0", {"center": v(302.5, -99) * mm, "radius": 2.5 * mm});
            skCircle(sketch, "E1.55.19.0", {"center": v(302.5, -104.5) * mm, "radius": 2.5 * mm});
            skCircle(sketch, "E1.55.20.0", {"center": v(302.5, -110) * mm, "radius": 2.5 * mm});
            skCircle(sketch, "E1.55.21.0", {"center": v(302.5, -115.5) * mm, "radius": 2.5 * mm});
            skCircle(sketch, "E1.55.22.0", {"center": v(302.5, -121) * mm, "radius": 2.5 * mm});
            skCircle(sketch, "E1.55.23.0", {"center": v(302.5, -126.5) * mm, "radius": 2.5 * mm});
            skCircle(sketch, "E1.55.24.0", {"center": v(302.5, -132) * mm, "radius": 2.5 * mm});
            skCircle(sketch, "E1.56.0.0", {"center": v(308, 0) * mm, "radius": 2.5 * mm});
            skCircle(sketch, "E1.56.1.0", {"center": v(308, -5.5) * mm, "radius": 2.5 * mm});
            skCircle(sketch, "E1.56.2.0", {"center": v(308, -11) * mm, "radius": 2.5 * mm});
            skCircle(sketch, "E1.56.3.0", {"center": v(308, -16.5) * mm, "radius": 2.5 * mm});
            skCircle(sketch, "E1.56.4.0", {"center": v(308, -22) * mm, "radius": 2.5 * mm});
            skCircle(sketch, "E1.56.5.0", {"center": v(308, -27.5) * mm, "radius": 2.5 * mm});
            skCircle(sketch, "E1.56.6.0", {"center": v(308, -33) * mm, "radius": 2.5 * mm});
            skCircle(sketch, "E1.56.7.0", {"center": v(308, -38.5) * mm, "radius": 2.5 * mm});
            skCircle(sketch, "E1.56.8.0", {"center": v(308, -44) * mm, "radius": 2.5 * mm});
            skCircle(sketch, "E1.56.9.0", {"center": v(308, -49.5) * mm, "radius": 2.5 * mm});
            skCircle(sketch, "E1.56.10.0", {"center": v(308, -55) * mm, "radius": 2.5 * mm});
            skCircle(sketch, "E1.56.11.0", {"center": v(308, -60.5) * mm, "radius": 2.5 * mm});
            skCircle(sketch, "E1.56.12.0", {"center": v(308, -66) * mm, "radius": 2.5 * mm});
            skCircle(sketch, "E1.56.13.0", {"center": v(308, -71.5) * mm, "radius": 2.5 * mm});
            skCircle(sketch, "E1.56.14.0", {"center": v(308, -77) * mm, "radius": 2.5 * mm});
            skCircle(sketch, "E1.56.15.0", {"center": v(308, -82.5) * mm, "radius": 2.5 * mm});
            skCircle(sketch, "E1.56.16.0", {"center": v(308, -88) * mm, "radius": 2.5 * mm});
            skCircle(sketch, "E1.56.17.0", {"center": v(308, -93.5) * mm, "radius": 2.5 * mm});
            skCircle(sketch, "E1.56.18.0", {"center": v(308, -99) * mm, "radius": 2.5 * mm});
            skCircle(sketch, "E1.56.19.0", {"center": v(308, -104.5) * mm, "radius": 2.5 * mm});
            skCircle(sketch, "E1.56.20.0", {"center": v(308, -110) * mm, "radius": 2.5 * mm});
            skCircle(sketch, "E1.56.21.0", {"center": v(308, -115.5) * mm, "radius": 2.5 * mm});
            skCircle(sketch, "E1.56.22.0", {"center": v(308, -121) * mm, "radius": 2.5 * mm});
            skCircle(sketch, "E1.56.23.0", {"center": v(308, -126.5) * mm, "radius": 2.5 * mm});
            skCircle(sketch, "E1.56.24.0", {"center": v(308, -132) * mm, "radius": 2.5 * mm});
            skCircle(sketch, "E1.57.0.0", {"center": v(313.5, 0) * mm, "radius": 2.5 * mm});
            skCircle(sketch, "E1.57.1.0", {"center": v(313.5, -5.5) * mm, "radius": 2.5 * mm});
            skCircle(sketch, "E1.57.2.0", {"center": v(313.5, -11) * mm, "radius": 2.5 * mm});
            skCircle(sketch, "E1.57.3.0", {"center": v(313.5, -16.5) * mm, "radius": 2.5 * mm});
            skCircle(sketch, "E1.57.4.0", {"center": v(313.5, -22) * mm, "radius": 2.5 * mm});
            skCircle(sketch, "E1.57.5.0", {"center": v(313.5, -27.5) * mm, "radius": 2.5 * mm});
            skCircle(sketch, "E1.57.6.0", {"center": v(313.5, -33) * mm, "radius": 2.5 * mm});
            skCircle(sketch, "E1.57.7.0", {"center": v(313.5, -38.5) * mm, "radius": 2.5 * mm});
            skCircle(sketch, "E1.57.8.0", {"center": v(313.5, -44) * mm, "radius": 2.5 * mm});
            skCircle(sketch, "E1.57.9.0", {"center": v(313.5, -49.5) * mm, "radius": 2.5 * mm});
            skCircle(sketch, "E1.57.10.0", {"center": v(313.5, -55) * mm, "radius": 2.5 * mm});
            skCircle(sketch, "E1.57.11.0", {"center": v(313.5, -60.5) * mm, "radius": 2.5 * mm});
            skCircle(sketch, "E1.57.12.0", {"center": v(313.5, -66) * mm, "radius": 2.5 * mm});
            skCircle(sketch, "E1.57.13.0", {"center": v(313.5, -71.5) * mm, "radius": 2.5 * mm});
            skCircle(sketch, "E1.57.14.0", {"center": v(313.5, -77) * mm, "radius": 2.5 * mm});
            skCircle(sketch, "E1.57.15.0", {"center": v(313.5, -82.5) * mm, "radius": 2.5 * mm});
            skCircle(sketch, "E1.57.16.0", {"center": v(313.5, -88) * mm, "radius": 2.5 * mm});
            skCircle(sketch, "E1.57.17.0", {"center": v(313.5, -93.5) * mm, "radius": 2.5 * mm});
            skCircle(sketch, "E1.57.18.0", {"center": v(313.5, -99) * mm, "radius": 2.5 * mm});
            skCircle(sketch, "E1.57.19.0", {"center": v(313.5, -104.5) * mm, "radius": 2.5 * mm});
            skCircle(sketch, "E1.57.20.0", {"center": v(313.5, -110) * mm, "radius": 2.5 * mm});
            skCircle(sketch, "E1.57.21.0", {"center": v(313.5, -115.5) * mm, "radius": 2.5 * mm});
            skCircle(sketch, "E1.57.22.0", {"center": v(313.5, -121) * mm, "radius": 2.5 * mm});
            skCircle(sketch, "E1.57.23.0", {"center": v(313.5, -126.5) * mm, "radius": 2.5 * mm});
            skCircle(sketch, "E1.57.24.0", {"center": v(313.5, -132) * mm, "radius": 2.5 * mm});
            skCircle(sketch, "E1.58.0.0", {"center": v(319, 0) * mm, "radius": 2.5 * mm});
            skCircle(sketch, "E1.58.1.0", {"center": v(319, -5.5) * mm, "radius": 2.5 * mm});
            skCircle(sketch, "E1.58.2.0", {"center": v(319, -11) * mm, "radius": 2.5 * mm});
            skCircle(sketch, "E1.58.3.0", {"center": v(319, -16.5) * mm, "radius": 2.5 * mm});
            skCircle(sketch, "E1.58.4.0", {"center": v(319, -22) * mm, "radius": 2.5 * mm});
            skCircle(sketch, "E1.58.5.0", {"center": v(319, -27.5) * mm, "radius": 2.5 * mm});
            skCircle(sketch, "E1.58.6.0", {"center": v(319, -33) * mm, "radius": 2.5 * mm});
            skCircle(sketch, "E1.58.7.0", {"center": v(319, -38.5) * mm, "radius": 2.5 * mm});
            skCircle(sketch, "E1.58.8.0", {"center": v(319, -44) * mm, "radius": 2.5 * mm});
            skCircle(sketch, "E1.58.9.0", {"center": v(319, -49.5) * mm, "radius": 2.5 * mm});
            skCircle(sketch, "E1.58.10.0", {"center": v(319, -55) * mm, "radius": 2.5 * mm});
            skCircle(sketch, "E1.58.11.0", {"center": v(319, -60.5) * mm, "radius": 2.5 * mm});
            skCircle(sketch, "E1.58.12.0", {"center": v(319, -66) * mm, "radius": 2.5 * mm});
            skCircle(sketch, "E1.58.13.0", {"center": v(319, -71.5) * mm, "radius": 2.5 * mm});
            skCircle(sketch, "E1.58.14.0", {"center": v(319, -77) * mm, "radius": 2.5 * mm});
            skCircle(sketch, "E1.58.15.0", {"center": v(319, -82.5) * mm, "radius": 2.5 * mm});
            skCircle(sketch, "E1.58.16.0", {"center": v(319, -88) * mm, "radius": 2.5 * mm});
            skCircle(sketch, "E1.58.17.0", {"center": v(319, -93.5) * mm, "radius": 2.5 * mm});
            skCircle(sketch, "E1.58.18.0", {"center": v(319, -99) * mm, "radius": 2.5 * mm});
            skCircle(sketch, "E1.58.19.0", {"center": v(319, -104.5) * mm, "radius": 2.5 * mm});
            skCircle(sketch, "E1.58.20.0", {"center": v(319, -110) * mm, "radius": 2.5 * mm});
            skCircle(sketch, "E1.58.21.0", {"center": v(319, -115.5) * mm, "radius": 2.5 * mm});
            skCircle(sketch, "E1.58.22.0", {"center": v(319, -121) * mm, "radius": 2.5 * mm});
            skCircle(sketch, "E1.58.23.0", {"center": v(319, -126.5) * mm, "radius": 2.5 * mm});
            skCircle(sketch, "E1.58.24.0", {"center": v(319, -132) * mm, "radius": 2.5 * mm});
            skCircle(sketch, "E1.59.0.0", {"center": v(324.5, 0) * mm, "radius": 2.5 * mm});
            skCircle(sketch, "E1.59.1.0", {"center": v(324.5, -5.5) * mm, "radius": 2.5 * mm});
            skCircle(sketch, "E1.59.2.0", {"center": v(324.5, -11) * mm, "radius": 2.5 * mm});
            skCircle(sketch, "E1.59.3.0", {"center": v(324.5, -16.5) * mm, "radius": 2.5 * mm});
            skCircle(sketch, "E1.59.4.0", {"center": v(324.5, -22) * mm, "radius": 2.5 * mm});
            skCircle(sketch, "E1.59.5.0", {"center": v(324.5, -27.5) * mm, "radius": 2.5 * mm});
            skCircle(sketch, "E1.59.6.0", {"center": v(324.5, -33) * mm, "radius": 2.5 * mm});
            skCircle(sketch, "E1.59.7.0", {"center": v(324.5, -38.5) * mm, "radius": 2.5 * mm});
            skCircle(sketch, "E1.59.8.0", {"center": v(324.5, -44) * mm, "radius": 2.5 * mm});
            skCircle(sketch, "E1.59.9.0", {"center": v(324.5, -49.5) * mm, "radius": 2.5 * mm});
            skCircle(sketch, "E1.59.10.0", {"center": v(324.5, -55) * mm, "radius": 2.5 * mm});
            skCircle(sketch, "E1.59.11.0", {"center": v(324.5, -60.5) * mm, "radius": 2.5 * mm});
            skCircle(sketch, "E1.59.12.0", {"center": v(324.5, -66) * mm, "radius": 2.5 * mm});
            skCircle(sketch, "E1.59.13.0", {"center": v(324.5, -71.5) * mm, "radius": 2.5 * mm});
            skCircle(sketch, "E1.59.14.0", {"center": v(324.5, -77) * mm, "radius": 2.5 * mm});
            skCircle(sketch, "E1.59.15.0", {"center": v(324.5, -82.5) * mm, "radius": 2.5 * mm});
            skCircle(sketch, "E1.59.16.0", {"center": v(324.5, -88) * mm, "radius": 2.5 * mm});
            skCircle(sketch, "E1.59.17.0", {"center": v(324.5, -93.5) * mm, "radius": 2.5 * mm});
            skCircle(sketch, "E1.59.18.0", {"center": v(324.5, -99) * mm, "radius": 2.5 * mm});
            skCircle(sketch, "E1.59.19.0", {"center": v(324.5, -104.5) * mm, "radius": 2.5 * mm});
            skCircle(sketch, "E1.59.20.0", {"center": v(324.5, -110) * mm, "radius": 2.5 * mm});
            skCircle(sketch, "E1.59.21.0", {"center": v(324.5, -115.5) * mm, "radius": 2.5 * mm});
            skCircle(sketch, "E1.59.22.0", {"center": v(324.5, -121) * mm, "radius": 2.5 * mm});
            skCircle(sketch, "E1.59.23.0", {"center": v(324.5, -126.5) * mm, "radius": 2.5 * mm});
            skCircle(sketch, "E1.59.24.0", {"center": v(324.5, -132) * mm, "radius": 2.5 * mm});
            skCircle(sketch, "E1.60.0.0", {"center": v(330, 0) * mm, "radius": 2.5 * mm});
            skCircle(sketch, "E1.60.1.0", {"center": v(330, -5.5) * mm, "radius": 2.5 * mm});
            skCircle(sketch, "E1.60.2.0", {"center": v(330, -11) * mm, "radius": 2.5 * mm});
            skCircle(sketch, "E1.60.3.0", {"center": v(330, -16.5) * mm, "radius": 2.5 * mm});
            skCircle(sketch, "E1.60.4.0", {"center": v(330, -22) * mm, "radius": 2.5 * mm});
            skCircle(sketch, "E1.60.5.0", {"center": v(330, -27.5) * mm, "radius": 2.5 * mm});
            skCircle(sketch, "E1.60.6.0", {"center": v(330, -33) * mm, "radius": 2.5 * mm});
            skCircle(sketch, "E1.60.7.0", {"center": v(330, -38.5) * mm, "radius": 2.5 * mm});
            skCircle(sketch, "E1.60.8.0", {"center": v(330, -44) * mm, "radius": 2.5 * mm});
            skCircle(sketch, "E1.60.9.0", {"center": v(330, -49.5) * mm, "radius": 2.5 * mm});
            skCircle(sketch, "E1.60.10.0", {"center": v(330, -55) * mm, "radius": 2.5 * mm});
            skCircle(sketch, "E1.60.11.0", {"center": v(330, -60.5) * mm, "radius": 2.5 * mm});
            skCircle(sketch, "E1.60.12.0", {"center": v(330, -66) * mm, "radius": 2.5 * mm});
            skCircle(sketch, "E1.60.13.0", {"center": v(330, -71.5) * mm, "radius": 2.5 * mm});
            skCircle(sketch, "E1.60.14.0", {"center": v(330, -77) * mm, "radius": 2.5 * mm});
            skCircle(sketch, "E1.60.15.0", {"center": v(330, -82.5) * mm, "radius": 2.5 * mm});
            skCircle(sketch, "E1.60.16.0", {"center": v(330, -88) * mm, "radius": 2.5 * mm});
            skCircle(sketch, "E1.60.17.0", {"center": v(330, -93.5) * mm, "radius": 2.5 * mm});
            skCircle(sketch, "E1.60.18.0", {"center": v(330, -99) * mm, "radius": 2.5 * mm});
            skCircle(sketch, "E1.60.19.0", {"center": v(330, -104.5) * mm, "radius": 2.5 * mm});
            skCircle(sketch, "E1.60.20.0", {"center": v(330, -110) * mm, "radius": 2.5 * mm});
            skCircle(sketch, "E1.60.21.0", {"center": v(330, -115.5) * mm, "radius": 2.5 * mm});
            skCircle(sketch, "E1.60.22.0", {"center": v(330, -121) * mm, "radius": 2.5 * mm});
            skCircle(sketch, "E1.60.23.0", {"center": v(330, -126.5) * mm, "radius": 2.5 * mm});
            skCircle(sketch, "E1.60.24.0", {"center": v(330, -132) * mm, "radius": 2.5 * mm});
            skCircle(sketch, "E1.61.0.0", {"center": v(335.5, 0) * mm, "radius": 2.5 * mm});
            skCircle(sketch, "E1.61.1.0", {"center": v(335.5, -5.5) * mm, "radius": 2.5 * mm});
            skCircle(sketch, "E1.61.2.0", {"center": v(335.5, -11) * mm, "radius": 2.5 * mm});
            skCircle(sketch, "E1.61.3.0", {"center": v(335.5, -16.5) * mm, "radius": 2.5 * mm});
            skCircle(sketch, "E1.61.4.0", {"center": v(335.5, -22) * mm, "radius": 2.5 * mm});
            skCircle(sketch, "E1.61.5.0", {"center": v(335.5, -27.5) * mm, "radius": 2.5 * mm});
            skCircle(sketch, "E1.61.6.0", {"center": v(335.5, -33) * mm, "radius": 2.5 * mm});
            skCircle(sketch, "E1.61.7.0", {"center": v(335.5, -38.5) * mm, "radius": 2.5 * mm});
            skCircle(sketch, "E1.61.8.0", {"center": v(335.5, -44) * mm, "radius": 2.5 * mm});
            skCircle(sketch, "E1.61.9.0", {"center": v(335.5, -49.5) * mm, "radius": 2.5 * mm});
            skCircle(sketch, "E1.61.10.0", {"center": v(335.5, -55) * mm, "radius": 2.5 * mm});
            skCircle(sketch, "E1.61.11.0", {"center": v(335.5, -60.5) * mm, "radius": 2.5 * mm});
            skCircle(sketch, "E1.61.12.0", {"center": v(335.5, -66) * mm, "radius": 2.5 * mm});
            skCircle(sketch, "E1.61.13.0", {"center": v(335.5, -71.5) * mm, "radius": 2.5 * mm});
            skCircle(sketch, "E1.61.14.0", {"center": v(335.5, -77) * mm, "radius": 2.5 * mm});
            skCircle(sketch, "E1.61.15.0", {"center": v(335.5, -82.5) * mm, "radius": 2.5 * mm});
            skCircle(sketch, "E1.61.16.0", {"center": v(335.5, -88) * mm, "radius": 2.5 * mm});
            skCircle(sketch, "E1.61.17.0", {"center": v(335.5, -93.5) * mm, "radius": 2.5 * mm});
            skCircle(sketch, "E1.61.18.0", {"center": v(335.5, -99) * mm, "radius": 2.5 * mm});
            skCircle(sketch, "E1.61.19.0", {"center": v(335.5, -104.5) * mm, "radius": 2.5 * mm});
            skCircle(sketch, "E1.61.20.0", {"center": v(335.5, -110) * mm, "radius": 2.5 * mm});
            skCircle(sketch, "E1.61.21.0", {"center": v(335.5, -115.5) * mm, "radius": 2.5 * mm});
            skCircle(sketch, "E1.61.22.0", {"center": v(335.5, -121) * mm, "radius": 2.5 * mm});
            skCircle(sketch, "E1.61.23.0", {"center": v(335.5, -126.5) * mm, "radius": 2.5 * mm});
            skCircle(sketch, "E1.61.24.0", {"center": v(335.5, -132) * mm, "radius": 2.5 * mm});
            skCircle(sketch, "E1.62.0.0", {"center": v(341, 0) * mm, "radius": 2.5 * mm});
            skCircle(sketch, "E1.62.1.0", {"center": v(341, -5.5) * mm, "radius": 2.5 * mm});
            skCircle(sketch, "E1.62.2.0", {"center": v(341, -11) * mm, "radius": 2.5 * mm});
            skCircle(sketch, "E1.62.3.0", {"center": v(341, -16.5) * mm, "radius": 2.5 * mm});
            skCircle(sketch, "E1.62.4.0", {"center": v(341, -22) * mm, "radius": 2.5 * mm});
            skCircle(sketch, "E1.62.5.0", {"center": v(341, -27.5) * mm, "radius": 2.5 * mm});
            skCircle(sketch, "E1.62.6.0", {"center": v(341, -33) * mm, "radius": 2.5 * mm});
            skCircle(sketch, "E1.62.7.0", {"center": v(341, -38.5) * mm, "radius": 2.5 * mm});
            skCircle(sketch, "E1.62.8.0", {"center": v(341, -44) * mm, "radius": 2.5 * mm});
            skCircle(sketch, "E1.62.9.0", {"center": v(341, -49.5) * mm, "radius": 2.5 * mm});
            skCircle(sketch, "E1.62.10.0", {"center": v(341, -55) * mm, "radius": 2.5 * mm});
            skCircle(sketch, "E1.62.11.0", {"center": v(341, -60.5) * mm, "radius": 2.5 * mm});
            skCircle(sketch, "E1.62.12.0", {"center": v(341, -66) * mm, "radius": 2.5 * mm});
            skCircle(sketch, "E1.62.13.0", {"center": v(341, -71.5) * mm, "radius": 2.5 * mm});
            skCircle(sketch, "E1.62.14.0", {"center": v(341, -77) * mm, "radius": 2.5 * mm});
            skCircle(sketch, "E1.62.15.0", {"center": v(341, -82.5) * mm, "radius": 2.5 * mm});
            skCircle(sketch, "E1.62.16.0", {"center": v(341, -88) * mm, "radius": 2.5 * mm});
            skCircle(sketch, "E1.62.17.0", {"center": v(341, -93.5) * mm, "radius": 2.5 * mm});
            skCircle(sketch, "E1.62.18.0", {"center": v(341, -99) * mm, "radius": 2.5 * mm});
            skCircle(sketch, "E1.62.19.0", {"center": v(341, -104.5) * mm, "radius": 2.5 * mm});
            skCircle(sketch, "E1.62.20.0", {"center": v(341, -110) * mm, "radius": 2.5 * mm});
            skCircle(sketch, "E1.62.21.0", {"center": v(341, -115.5) * mm, "radius": 2.5 * mm});
            skCircle(sketch, "E1.62.22.0", {"center": v(341, -121) * mm, "radius": 2.5 * mm});
            skCircle(sketch, "E1.62.23.0", {"center": v(341, -126.5) * mm, "radius": 2.5 * mm});
            skCircle(sketch, "E1.62.24.0", {"center": v(341, -132) * mm, "radius": 2.5 * mm});
            skCircle(sketch, "E1.63.0.0", {"center": v(346.5, 0) * mm, "radius": 2.5 * mm});
            skCircle(sketch, "E1.63.1.0", {"center": v(346.5, -5.5) * mm, "radius": 2.5 * mm});
            skCircle(sketch, "E1.63.2.0", {"center": v(346.5, -11) * mm, "radius": 2.5 * mm});
            skCircle(sketch, "E1.63.3.0", {"center": v(346.5, -16.5) * mm, "radius": 2.5 * mm});
            skCircle(sketch, "E1.63.4.0", {"center": v(346.5, -22) * mm, "radius": 2.5 * mm});
            skCircle(sketch, "E1.63.5.0", {"center": v(346.5, -27.5) * mm, "radius": 2.5 * mm});
            skCircle(sketch, "E1.63.6.0", {"center": v(346.5, -33) * mm, "radius": 2.5 * mm});
            skCircle(sketch, "E1.63.7.0", {"center": v(346.5, -38.5) * mm, "radius": 2.5 * mm});
            skCircle(sketch, "E1.63.8.0", {"center": v(346.5, -44) * mm, "radius": 2.5 * mm});
            skCircle(sketch, "E1.63.9.0", {"center": v(346.5, -49.5) * mm, "radius": 2.5 * mm});
            skCircle(sketch, "E1.63.10.0", {"center": v(346.5, -55) * mm, "radius": 2.5 * mm});
            skCircle(sketch, "E1.63.11.0", {"center": v(346.5, -60.5) * mm, "radius": 2.5 * mm});
            skCircle(sketch, "E1.63.12.0", {"center": v(346.5, -66) * mm, "radius": 2.5 * mm});
            skCircle(sketch, "E1.63.13.0", {"center": v(346.5, -71.5) * mm, "radius": 2.5 * mm});
            skCircle(sketch, "E1.63.14.0", {"center": v(346.5, -77) * mm, "radius": 2.5 * mm});
            skCircle(sketch, "E1.63.15.0", {"center": v(346.5, -82.5) * mm, "radius": 2.5 * mm});
            skCircle(sketch, "E1.63.16.0", {"center": v(346.5, -88) * mm, "radius": 2.5 * mm});
            skCircle(sketch, "E1.63.17.0", {"center": v(346.5, -93.5) * mm, "radius": 2.5 * mm});
            skCircle(sketch, "E1.63.18.0", {"center": v(346.5, -99) * mm, "radius": 2.5 * mm});
            skCircle(sketch, "E1.63.19.0", {"center": v(346.5, -104.5) * mm, "radius": 2.5 * mm});
            skCircle(sketch, "E1.63.20.0", {"center": v(346.5, -110) * mm, "radius": 2.5 * mm});
            skCircle(sketch, "E1.63.21.0", {"center": v(346.5, -115.5) * mm, "radius": 2.5 * mm});
            skCircle(sketch, "E1.63.22.0", {"center": v(346.5, -121) * mm, "radius": 2.5 * mm});
            skCircle(sketch, "E1.63.23.0", {"center": v(346.5, -126.5) * mm, "radius": 2.5 * mm});
            skCircle(sketch, "E1.63.24.0", {"center": v(346.5, -132) * mm, "radius": 2.5 * mm});
            skCircle(sketch, "E1.64.0.0", {"center": v(352, 0) * mm, "radius": 2.5 * mm});
            skCircle(sketch, "E1.64.1.0", {"center": v(352, -5.5) * mm, "radius": 2.5 * mm});
            skCircle(sketch, "E1.64.2.0", {"center": v(352, -11) * mm, "radius": 2.5 * mm});
            skCircle(sketch, "E1.64.3.0", {"center": v(352, -16.5) * mm, "radius": 2.5 * mm});
            skCircle(sketch, "E1.64.4.0", {"center": v(352, -22) * mm, "radius": 2.5 * mm});
            skCircle(sketch, "E1.64.5.0", {"center": v(352, -27.5) * mm, "radius": 2.5 * mm});
            skCircle(sketch, "E1.64.6.0", {"center": v(352, -33) * mm, "radius": 2.5 * mm});
            skCircle(sketch, "E1.64.7.0", {"center": v(352, -38.5) * mm, "radius": 2.5 * mm});
            skCircle(sketch, "E1.64.8.0", {"center": v(352, -44) * mm, "radius": 2.5 * mm});
            skCircle(sketch, "E1.64.9.0", {"center": v(352, -49.5) * mm, "radius": 2.5 * mm});
            skCircle(sketch, "E1.64.10.0", {"center": v(352, -55) * mm, "radius": 2.5 * mm});
            skCircle(sketch, "E1.64.11.0", {"center": v(352, -60.5) * mm, "radius": 2.5 * mm});
            skCircle(sketch, "E1.64.12.0", {"center": v(352, -66) * mm, "radius": 2.5 * mm});
            skCircle(sketch, "E1.64.13.0", {"center": v(352, -71.5) * mm, "radius": 2.5 * mm});
            skCircle(sketch, "E1.64.14.0", {"center": v(352, -77) * mm, "radius": 2.5 * mm});
            skCircle(sketch, "E1.64.15.0", {"center": v(352, -82.5) * mm, "radius": 2.5 * mm});
            skCircle(sketch, "E1.64.16.0", {"center": v(352, -88) * mm, "radius": 2.5 * mm});
            skCircle(sketch, "E1.64.17.0", {"center": v(352, -93.5) * mm, "radius": 2.5 * mm});
            skCircle(sketch, "E1.64.18.0", {"center": v(352, -99) * mm, "radius": 2.5 * mm});
            skCircle(sketch, "E1.64.19.0", {"center": v(352, -104.5) * mm, "radius": 2.5 * mm});
            skCircle(sketch, "E1.64.20.0", {"center": v(352, -110) * mm, "radius": 2.5 * mm});
            skCircle(sketch, "E1.64.21.0", {"center": v(352, -115.5) * mm, "radius": 2.5 * mm});
            skCircle(sketch, "E1.64.22.0", {"center": v(352, -121) * mm, "radius": 2.5 * mm});
            skCircle(sketch, "E1.64.23.0", {"center": v(352, -126.5) * mm, "radius": 2.5 * mm});
            skCircle(sketch, "E1.64.24.0", {"center": v(352, -132) * mm, "radius": 2.5 * mm});
            skCircle(sketch, "E1.65.0.0", {"center": v(357.5, 0) * mm, "radius": 2.5 * mm});
            skCircle(sketch, "E1.65.1.0", {"center": v(357.5, -5.5) * mm, "radius": 2.5 * mm});
            skCircle(sketch, "E1.65.2.0", {"center": v(357.5, -11) * mm, "radius": 2.5 * mm});
            skCircle(sketch, "E1.65.3.0", {"center": v(357.5, -16.5) * mm, "radius": 2.5 * mm});
            skCircle(sketch, "E1.65.4.0", {"center": v(357.5, -22) * mm, "radius": 2.5 * mm});
            skCircle(sketch, "E1.65.5.0", {"center": v(357.5, -27.5) * mm, "radius": 2.5 * mm});
            skCircle(sketch, "E1.65.6.0", {"center": v(357.5, -33) * mm, "radius": 2.5 * mm});
            skCircle(sketch, "E1.65.7.0", {"center": v(357.5, -38.5) * mm, "radius": 2.5 * mm});
            skCircle(sketch, "E1.65.8.0", {"center": v(357.5, -44) * mm, "radius": 2.5 * mm});
            skCircle(sketch, "E1.65.9.0", {"center": v(357.5, -49.5) * mm, "radius": 2.5 * mm});
            skCircle(sketch, "E1.65.10.0", {"center": v(357.5, -55) * mm, "radius": 2.5 * mm});
            skCircle(sketch, "E1.65.11.0", {"center": v(357.5, -60.5) * mm, "radius": 2.5 * mm});
            skCircle(sketch, "E1.65.12.0", {"center": v(357.5, -66) * mm, "radius": 2.5 * mm});
            skCircle(sketch, "E1.65.13.0", {"center": v(357.5, -71.5) * mm, "radius": 2.5 * mm});
            skCircle(sketch, "E1.65.14.0", {"center": v(357.5, -77) * mm, "radius": 2.5 * mm});
            skCircle(sketch, "E1.65.15.0", {"center": v(357.5, -82.5) * mm, "radius": 2.5 * mm});
            skCircle(sketch, "E1.65.16.0", {"center": v(357.5, -88) * mm, "radius": 2.5 * mm});
            skCircle(sketch, "E1.65.17.0", {"center": v(357.5, -93.5) * mm, "radius": 2.5 * mm});
            skCircle(sketch, "E1.65.18.0", {"center": v(357.5, -99) * mm, "radius": 2.5 * mm});
            skCircle(sketch, "E1.65.19.0", {"center": v(357.5, -104.5) * mm, "radius": 2.5 * mm});
            skCircle(sketch, "E1.65.20.0", {"center": v(357.5, -110) * mm, "radius": 2.5 * mm});
            skCircle(sketch, "E1.65.21.0", {"center": v(357.5, -115.5) * mm, "radius": 2.5 * mm});
            skCircle(sketch, "E1.65.22.0", {"center": v(357.5, -121) * mm, "radius": 2.5 * mm});
            skCircle(sketch, "E1.65.23.0", {"center": v(357.5, -126.5) * mm, "radius": 2.5 * mm});
            skCircle(sketch, "E1.65.24.0", {"center": v(357.5, -132) * mm, "radius": 2.5 * mm});
            skCircle(sketch, "E1.66.0.0", {"center": v(363, 0) * mm, "radius": 2.5 * mm});
            skCircle(sketch, "E1.66.1.0", {"center": v(363, -5.5) * mm, "radius": 2.5 * mm});
            skCircle(sketch, "E1.66.2.0", {"center": v(363, -11) * mm, "radius": 2.5 * mm});
            skCircle(sketch, "E1.66.3.0", {"center": v(363, -16.5) * mm, "radius": 2.5 * mm});
            skCircle(sketch, "E1.66.4.0", {"center": v(363, -22) * mm, "radius": 2.5 * mm});
            skCircle(sketch, "E1.66.5.0", {"center": v(363, -27.5) * mm, "radius": 2.5 * mm});
            skCircle(sketch, "E1.66.6.0", {"center": v(363, -33) * mm, "radius": 2.5 * mm});
            skCircle(sketch, "E1.66.7.0", {"center": v(363, -38.5) * mm, "radius": 2.5 * mm});
            skCircle(sketch, "E1.66.8.0", {"center": v(363, -44) * mm, "radius": 2.5 * mm});
            skCircle(sketch, "E1.66.9.0", {"center": v(363, -49.5) * mm, "radius": 2.5 * mm});
            skCircle(sketch, "E1.66.10.0", {"center": v(363, -55) * mm, "radius": 2.5 * mm});
            skCircle(sketch, "E1.66.11.0", {"center": v(363, -60.5) * mm, "radius": 2.5 * mm});
            skCircle(sketch, "E1.66.12.0", {"center": v(363, -66) * mm, "radius": 2.5 * mm});
            skCircle(sketch, "E1.66.13.0", {"center": v(363, -71.5) * mm, "radius": 2.5 * mm});
            skCircle(sketch, "E1.66.14.0", {"center": v(363, -77) * mm, "radius": 2.5 * mm});
            skCircle(sketch, "E1.66.15.0", {"center": v(363, -82.5) * mm, "radius": 2.5 * mm});
            skCircle(sketch, "E1.66.16.0", {"center": v(363, -88) * mm, "radius": 2.5 * mm});
            skCircle(sketch, "E1.66.17.0", {"center": v(363, -93.5) * mm, "radius": 2.5 * mm});
            skCircle(sketch, "E1.66.18.0", {"center": v(363, -99) * mm, "radius": 2.5 * mm});
            skCircle(sketch, "E1.66.19.0", {"center": v(363, -104.5) * mm, "radius": 2.5 * mm});
            skCircle(sketch, "E1.66.20.0", {"center": v(363, -110) * mm, "radius": 2.5 * mm});
            skCircle(sketch, "E1.66.21.0", {"center": v(363, -115.5) * mm, "radius": 2.5 * mm});
            skCircle(sketch, "E1.66.22.0", {"center": v(363, -121) * mm, "radius": 2.5 * mm});
            skCircle(sketch, "E1.66.23.0", {"center": v(363, -126.5) * mm, "radius": 2.5 * mm});
            skCircle(sketch, "E1.66.24.0", {"center": v(363, -132) * mm, "radius": 2.5 * mm});
            skCircle(sketch, "E1.67.0.0", {"center": v(368.5, 0) * mm, "radius": 2.5 * mm});
            skCircle(sketch, "E1.67.1.0", {"center": v(368.5, -5.5) * mm, "radius": 2.5 * mm});
            skCircle(sketch, "E1.67.2.0", {"center": v(368.5, -11) * mm, "radius": 2.5 * mm});
            skCircle(sketch, "E1.67.3.0", {"center": v(368.5, -16.5) * mm, "radius": 2.5 * mm});
            skCircle(sketch, "E1.67.4.0", {"center": v(368.5, -22) * mm, "radius": 2.5 * mm});
            skCircle(sketch, "E1.67.5.0", {"center": v(368.5, -27.5) * mm, "radius": 2.5 * mm});
            skCircle(sketch, "E1.67.6.0", {"center": v(368.5, -33) * mm, "radius": 2.5 * mm});
            skCircle(sketch, "E1.67.7.0", {"center": v(368.5, -38.5) * mm, "radius": 2.5 * mm});
            skCircle(sketch, "E1.67.8.0", {"center": v(368.5, -44) * mm, "radius": 2.5 * mm});
            skCircle(sketch, "E1.67.9.0", {"center": v(368.5, -49.5) * mm, "radius": 2.5 * mm});
            skCircle(sketch, "E1.67.10.0", {"center": v(368.5, -55) * mm, "radius": 2.5 * mm});
            skCircle(sketch, "E1.67.11.0", {"center": v(368.5, -60.5) * mm, "radius": 2.5 * mm});
            skCircle(sketch, "E1.67.12.0", {"center": v(368.5, -66) * mm, "radius": 2.5 * mm});
            skCircle(sketch, "E1.67.13.0", {"center": v(368.5, -71.5) * mm, "radius": 2.5 * mm});
            skCircle(sketch, "E1.67.14.0", {"center": v(368.5, -77) * mm, "radius": 2.5 * mm});
            skCircle(sketch, "E1.67.15.0", {"center": v(368.5, -82.5) * mm, "radius": 2.5 * mm});
            skCircle(sketch, "E1.67.16.0", {"center": v(368.5, -88) * mm, "radius": 2.5 * mm});
            skCircle(sketch, "E1.67.17.0", {"center": v(368.5, -93.5) * mm, "radius": 2.5 * mm});
            skCircle(sketch, "E1.67.18.0", {"center": v(368.5, -99) * mm, "radius": 2.5 * mm});
            skCircle(sketch, "E1.67.19.0", {"center": v(368.5, -104.5) * mm, "radius": 2.5 * mm});
            skCircle(sketch, "E1.67.20.0", {"center": v(368.5, -110) * mm, "radius": 2.5 * mm});
            skCircle(sketch, "E1.67.21.0", {"center": v(368.5, -115.5) * mm, "radius": 2.5 * mm});
            skCircle(sketch, "E1.67.22.0", {"center": v(368.5, -121) * mm, "radius": 2.5 * mm});
            skCircle(sketch, "E1.67.23.0", {"center": v(368.5, -126.5) * mm, "radius": 2.5 * mm});
            skCircle(sketch, "E1.67.24.0", {"center": v(368.5, -132) * mm, "radius": 2.5 * mm});
            skCircle(sketch, "E1.68.0.0", {"center": v(374, 0) * mm, "radius": 2.5 * mm});
            skCircle(sketch, "E1.68.1.0", {"center": v(374, -5.5) * mm, "radius": 2.5 * mm});
            skCircle(sketch, "E1.68.2.0", {"center": v(374, -11) * mm, "radius": 2.5 * mm});
            skCircle(sketch, "E1.68.3.0", {"center": v(374, -16.5) * mm, "radius": 2.5 * mm});
            skCircle(sketch, "E1.68.4.0", {"center": v(374, -22) * mm, "radius": 2.5 * mm});
            skCircle(sketch, "E1.68.5.0", {"center": v(374, -27.5) * mm, "radius": 2.5 * mm});
            skCircle(sketch, "E1.68.6.0", {"center": v(374, -33) * mm, "radius": 2.5 * mm});
            skCircle(sketch, "E1.68.7.0", {"center": v(374, -38.5) * mm, "radius": 2.5 * mm});
            skCircle(sketch, "E1.68.8.0", {"center": v(374, -44) * mm, "radius": 2.5 * mm});
            skCircle(sketch, "E1.68.9.0", {"center": v(374, -49.5) * mm, "radius": 2.5 * mm});
            skCircle(sketch, "E1.68.10.0", {"center": v(374, -55) * mm, "radius": 2.5 * mm});
            skCircle(sketch, "E1.68.11.0", {"center": v(374, -60.5) * mm, "radius": 2.5 * mm});
            skCircle(sketch, "E1.68.12.0", {"center": v(374, -66) * mm, "radius": 2.5 * mm});
            skCircle(sketch, "E1.68.13.0", {"center": v(374, -71.5) * mm, "radius": 2.5 * mm});
            skCircle(sketch, "E1.68.14.0", {"center": v(374, -77) * mm, "radius": 2.5 * mm});
            skCircle(sketch, "E1.68.15.0", {"center": v(374, -82.5) * mm, "radius": 2.5 * mm});
            skCircle(sketch, "E1.68.16.0", {"center": v(374, -88) * mm, "radius": 2.5 * mm});
            skCircle(sketch, "E1.68.17.0", {"center": v(374, -93.5) * mm, "radius": 2.5 * mm});
            skCircle(sketch, "E1.68.18.0", {"center": v(374, -99) * mm, "radius": 2.5 * mm});
            skCircle(sketch, "E1.68.19.0", {"center": v(374, -104.5) * mm, "radius": 2.5 * mm});
            skCircle(sketch, "E1.68.20.0", {"center": v(374, -110) * mm, "radius": 2.5 * mm});
            skCircle(sketch, "E1.68.21.0", {"center": v(374, -115.5) * mm, "radius": 2.5 * mm});
            skCircle(sketch, "E1.68.22.0", {"center": v(374, -121) * mm, "radius": 2.5 * mm});
            skCircle(sketch, "E1.68.23.0", {"center": v(374, -126.5) * mm, "radius": 2.5 * mm});
            skCircle(sketch, "E1.68.24.0", {"center": v(374, -132) * mm, "radius": 2.5 * mm});
            skCircle(sketch, "E1.69.0.0", {"center": v(379.5, 0) * mm, "radius": 2.5 * mm});
            skCircle(sketch, "E1.69.1.0", {"center": v(379.5, -5.5) * mm, "radius": 2.5 * mm});
            skCircle(sketch, "E1.69.2.0", {"center": v(379.5, -11) * mm, "radius": 2.5 * mm});
            skCircle(sketch, "E1.69.3.0", {"center": v(379.5, -16.5) * mm, "radius": 2.5 * mm});
            skCircle(sketch, "E1.69.4.0", {"center": v(379.5, -22) * mm, "radius": 2.5 * mm});
            skCircle(sketch, "E1.69.5.0", {"center": v(379.5, -27.5) * mm, "radius": 2.5 * mm});
            skCircle(sketch, "E1.69.6.0", {"center": v(379.5, -33) * mm, "radius": 2.5 * mm});
            skCircle(sketch, "E1.69.7.0", {"center": v(379.5, -38.5) * mm, "radius": 2.5 * mm});
            skCircle(sketch, "E1.69.8.0", {"center": v(379.5, -44) * mm, "radius": 2.5 * mm});
            skCircle(sketch, "E1.69.9.0", {"center": v(379.5, -49.5) * mm, "radius": 2.5 * mm});
            skCircle(sketch, "E1.69.10.0", {"center": v(379.5, -55) * mm, "radius": 2.5 * mm});
            skCircle(sketch, "E1.69.11.0", {"center": v(379.5, -60.5) * mm, "radius": 2.5 * mm});
            skCircle(sketch, "E1.69.12.0", {"center": v(379.5, -66) * mm, "radius": 2.5 * mm});
            skCircle(sketch, "E1.69.13.0", {"center": v(379.5, -71.5) * mm, "radius": 2.5 * mm});
            skCircle(sketch, "E1.69.14.0", {"center": v(379.5, -77) * mm, "radius": 2.5 * mm});
            skCircle(sketch, "E1.69.15.0", {"center": v(379.5, -82.5) * mm, "radius": 2.5 * mm});
            skCircle(sketch, "E1.69.16.0", {"center": v(379.5, -88) * mm, "radius": 2.5 * mm});
            skCircle(sketch, "E1.69.17.0", {"center": v(379.5, -93.5) * mm, "radius": 2.5 * mm});
            skCircle(sketch, "E1.69.18.0", {"center": v(379.5, -99) * mm, "radius": 2.5 * mm});
            skCircle(sketch, "E1.69.19.0", {"center": v(379.5, -104.5) * mm, "radius": 2.5 * mm});
            skCircle(sketch, "E1.69.20.0", {"center": v(379.5, -110) * mm, "radius": 2.5 * mm});
            skCircle(sketch, "E1.69.21.0", {"center": v(379.5, -115.5) * mm, "radius": 2.5 * mm});
            skCircle(sketch, "E1.69.22.0", {"center": v(379.5, -121) * mm, "radius": 2.5 * mm});
            skCircle(sketch, "E1.69.23.0", {"center": v(379.5, -126.5) * mm, "radius": 2.5 * mm});
            skCircle(sketch, "E1.69.24.0", {"center": v(379.5, -132) * mm, "radius": 2.5 * mm});
            skCircle(sketch, "E1.70.0.0", {"center": v(385, 0) * mm, "radius": 2.5 * mm});
            skCircle(sketch, "E1.70.1.0", {"center": v(385, -5.5) * mm, "radius": 2.5 * mm});
            skCircle(sketch, "E1.70.2.0", {"center": v(385, -11) * mm, "radius": 2.5 * mm});
            skCircle(sketch, "E1.70.3.0", {"center": v(385, -16.5) * mm, "radius": 2.5 * mm});
            skCircle(sketch, "E1.70.4.0", {"center": v(385, -22) * mm, "radius": 2.5 * mm});
            skCircle(sketch, "E1.70.5.0", {"center": v(385, -27.5) * mm, "radius": 2.5 * mm});
            skCircle(sketch, "E1.70.6.0", {"center": v(385, -33) * mm, "radius": 2.5 * mm});
            skCircle(sketch, "E1.70.7.0", {"center": v(385, -38.5) * mm, "radius": 2.5 * mm});
            skCircle(sketch, "E1.70.8.0", {"center": v(385, -44) * mm, "radius": 2.5 * mm});
            skCircle(sketch, "E1.70.9.0", {"center": v(385, -49.5) * mm, "radius": 2.5 * mm});
            skCircle(sketch, "E1.70.10.0", {"center": v(385, -55) * mm, "radius": 2.5 * mm});
            skCircle(sketch, "E1.70.11.0", {"center": v(385, -60.5) * mm, "radius": 2.5 * mm});
            skCircle(sketch, "E1.70.12.0", {"center": v(385, -66) * mm, "radius": 2.5 * mm});
            skCircle(sketch, "E1.70.13.0", {"center": v(385, -71.5) * mm, "radius": 2.5 * mm});
            skCircle(sketch, "E1.70.14.0", {"center": v(385, -77) * mm, "radius": 2.5 * mm});
            skCircle(sketch, "E1.70.15.0", {"center": v(385, -82.5) * mm, "radius": 2.5 * mm});
            skCircle(sketch, "E1.70.16.0", {"center": v(385, -88) * mm, "radius": 2.5 * mm});
            skCircle(sketch, "E1.70.17.0", {"center": v(385, -93.5) * mm, "radius": 2.5 * mm});
            skCircle(sketch, "E1.70.18.0", {"center": v(385, -99) * mm, "radius": 2.5 * mm});
            skCircle(sketch, "E1.70.19.0", {"center": v(385, -104.5) * mm, "radius": 2.5 * mm});
            skCircle(sketch, "E1.70.20.0", {"center": v(385, -110) * mm, "radius": 2.5 * mm});
            skCircle(sketch, "E1.70.21.0", {"center": v(385, -115.5) * mm, "radius": 2.5 * mm});
            skCircle(sketch, "E1.70.22.0", {"center": v(385, -121) * mm, "radius": 2.5 * mm});
            skCircle(sketch, "E1.70.23.0", {"center": v(385, -126.5) * mm, "radius": 2.5 * mm});
            skCircle(sketch, "E1.70.24.0", {"center": v(385, -132) * mm, "radius": 2.5 * mm});
            skCircle(sketch, "E1.71.0.0", {"center": v(390.5, 0) * mm, "radius": 2.5 * mm});
            skCircle(sketch, "E1.71.1.0", {"center": v(390.5, -5.5) * mm, "radius": 2.5 * mm});
            skCircle(sketch, "E1.71.2.0", {"center": v(390.5, -11) * mm, "radius": 2.5 * mm});
            skCircle(sketch, "E1.71.3.0", {"center": v(390.5, -16.5) * mm, "radius": 2.5 * mm});
            skCircle(sketch, "E1.71.4.0", {"center": v(390.5, -22) * mm, "radius": 2.5 * mm});
            skCircle(sketch, "E1.71.5.0", {"center": v(390.5, -27.5) * mm, "radius": 2.5 * mm});
            skCircle(sketch, "E1.71.6.0", {"center": v(390.5, -33) * mm, "radius": 2.5 * mm});
            skCircle(sketch, "E1.71.7.0", {"center": v(390.5, -38.5) * mm, "radius": 2.5 * mm});
            skCircle(sketch, "E1.71.8.0", {"center": v(390.5, -44) * mm, "radius": 2.5 * mm});
            skCircle(sketch, "E1.71.9.0", {"center": v(390.5, -49.5) * mm, "radius": 2.5 * mm});
            skCircle(sketch, "E1.71.10.0", {"center": v(390.5, -55) * mm, "radius": 2.5 * mm});
            skCircle(sketch, "E1.71.11.0", {"center": v(390.5, -60.5) * mm, "radius": 2.5 * mm});
            skCircle(sketch, "E1.71.12.0", {"center": v(390.5, -66) * mm, "radius": 2.5 * mm});
            skCircle(sketch, "E1.71.13.0", {"center": v(390.5, -71.5) * mm, "radius": 2.5 * mm});
            skCircle(sketch, "E1.71.14.0", {"center": v(390.5, -77) * mm, "radius": 2.5 * mm});
            skCircle(sketch, "E1.71.15.0", {"center": v(390.5, -82.5) * mm, "radius": 2.5 * mm});
            skCircle(sketch, "E1.71.16.0", {"center": v(390.5, -88) * mm, "radius": 2.5 * mm});
            skCircle(sketch, "E1.71.17.0", {"center": v(390.5, -93.5) * mm, "radius": 2.5 * mm});
            skCircle(sketch, "E1.71.18.0", {"center": v(390.5, -99) * mm, "radius": 2.5 * mm});
            skCircle(sketch, "E1.71.19.0", {"center": v(390.5, -104.5) * mm, "radius": 2.5 * mm});
            skCircle(sketch, "E1.71.20.0", {"center": v(390.5, -110) * mm, "radius": 2.5 * mm});
            skCircle(sketch, "E1.71.21.0", {"center": v(390.5, -115.5) * mm, "radius": 2.5 * mm});
            skCircle(sketch, "E1.71.22.0", {"center": v(390.5, -121) * mm, "radius": 2.5 * mm});
            skCircle(sketch, "E1.71.23.0", {"center": v(390.5, -126.5) * mm, "radius": 2.5 * mm});
            skCircle(sketch, "E1.71.24.0", {"center": v(390.5, -132) * mm, "radius": 2.5 * mm});
            skCircle(sketch, "E1.72.0.0", {"center": v(396, 0) * mm, "radius": 2.5 * mm});
            skCircle(sketch, "E1.72.1.0", {"center": v(396, -5.5) * mm, "radius": 2.5 * mm});
            skCircle(sketch, "E1.72.2.0", {"center": v(396, -11) * mm, "radius": 2.5 * mm});
            skCircle(sketch, "E1.72.3.0", {"center": v(396, -16.5) * mm, "radius": 2.5 * mm});
            skCircle(sketch, "E1.72.4.0", {"center": v(396, -22) * mm, "radius": 2.5 * mm});
            skCircle(sketch, "E1.72.5.0", {"center": v(396, -27.5) * mm, "radius": 2.5 * mm});
            skCircle(sketch, "E1.72.6.0", {"center": v(396, -33) * mm, "radius": 2.5 * mm});
            skCircle(sketch, "E1.72.7.0", {"center": v(396, -38.5) * mm, "radius": 2.5 * mm});
            skCircle(sketch, "E1.72.8.0", {"center": v(396, -44) * mm, "radius": 2.5 * mm});
            skCircle(sketch, "E1.72.9.0", {"center": v(396, -49.5) * mm, "radius": 2.5 * mm});
            skCircle(sketch, "E1.72.10.0", {"center": v(396, -55) * mm, "radius": 2.5 * mm});
            skCircle(sketch, "E1.72.11.0", {"center": v(396, -60.5) * mm, "radius": 2.5 * mm});
            skCircle(sketch, "E1.72.12.0", {"center": v(396, -66) * mm, "radius": 2.5 * mm});
            skCircle(sketch, "E1.72.13.0", {"center": v(396, -71.5) * mm, "radius": 2.5 * mm});
            skCircle(sketch, "E1.72.14.0", {"center": v(396, -77) * mm, "radius": 2.5 * mm});
            skCircle(sketch, "E1.72.15.0", {"center": v(396, -82.5) * mm, "radius": 2.5 * mm});
            skCircle(sketch, "E1.72.16.0", {"center": v(396, -88) * mm, "radius": 2.5 * mm});
            skCircle(sketch, "E1.72.17.0", {"center": v(396, -93.5) * mm, "radius": 2.5 * mm});
            skCircle(sketch, "E1.72.18.0", {"center": v(396, -99) * mm, "radius": 2.5 * mm});
            skCircle(sketch, "E1.72.19.0", {"center": v(396, -104.5) * mm, "radius": 2.5 * mm});
            skCircle(sketch, "E1.72.20.0", {"center": v(396, -110) * mm, "radius": 2.5 * mm});
            skCircle(sketch, "E1.72.21.0", {"center": v(396, -115.5) * mm, "radius": 2.5 * mm});
            skCircle(sketch, "E1.72.22.0", {"center": v(396, -121) * mm, "radius": 2.5 * mm});
            skCircle(sketch, "E1.72.23.0", {"center": v(396, -126.5) * mm, "radius": 2.5 * mm});
            skCircle(sketch, "E1.72.24.0", {"center": v(396, -132) * mm, "radius": 2.5 * mm});
            skCircle(sketch, "E1.73.0.0", {"center": v(401.5, 0) * mm, "radius": 2.5 * mm});
            skCircle(sketch, "E1.73.1.0", {"center": v(401.5, -5.5) * mm, "radius": 2.5 * mm});
            skCircle(sketch, "E1.73.2.0", {"center": v(401.5, -11) * mm, "radius": 2.5 * mm});
            skCircle(sketch, "E1.73.3.0", {"center": v(401.5, -16.5) * mm, "radius": 2.5 * mm});
            skCircle(sketch, "E1.73.4.0", {"center": v(401.5, -22) * mm, "radius": 2.5 * mm});
            skCircle(sketch, "E1.73.5.0", {"center": v(401.5, -27.5) * mm, "radius": 2.5 * mm});
            skCircle(sketch, "E1.73.6.0", {"center": v(401.5, -33) * mm, "radius": 2.5 * mm});
            skCircle(sketch, "E1.73.7.0", {"center": v(401.5, -38.5) * mm, "radius": 2.5 * mm});
            skCircle(sketch, "E1.73.8.0", {"center": v(401.5, -44) * mm, "radius": 2.5 * mm});
            skCircle(sketch, "E1.73.9.0", {"center": v(401.5, -49.5) * mm, "radius": 2.5 * mm});
            skCircle(sketch, "E1.73.10.0", {"center": v(401.5, -55) * mm, "radius": 2.5 * mm});
            skCircle(sketch, "E1.73.11.0", {"center": v(401.5, -60.5) * mm, "radius": 2.5 * mm});
            skCircle(sketch, "E1.73.12.0", {"center": v(401.5, -66) * mm, "radius": 2.5 * mm});
            skCircle(sketch, "E1.73.13.0", {"center": v(401.5, -71.5) * mm, "radius": 2.5 * mm});
            skCircle(sketch, "E1.73.14.0", {"center": v(401.5, -77) * mm, "radius": 2.5 * mm});
            skCircle(sketch, "E1.73.15.0", {"center": v(401.5, -82.5) * mm, "radius": 2.5 * mm});
            skCircle(sketch, "E1.73.16.0", {"center": v(401.5, -88) * mm, "radius": 2.5 * mm});
            skCircle(sketch, "E1.73.17.0", {"center": v(401.5, -93.5) * mm, "radius": 2.5 * mm});
            skCircle(sketch, "E1.73.18.0", {"center": v(401.5, -99) * mm, "radius": 2.5 * mm});
            skCircle(sketch, "E1.73.19.0", {"center": v(401.5, -104.5) * mm, "radius": 2.5 * mm});
            skCircle(sketch, "E1.73.20.0", {"center": v(401.5, -110) * mm, "radius": 2.5 * mm});
            skCircle(sketch, "E1.73.21.0", {"center": v(401.5, -115.5) * mm, "radius": 2.5 * mm});
            skCircle(sketch, "E1.73.22.0", {"center": v(401.5, -121) * mm, "radius": 2.5 * mm});
            skCircle(sketch, "E1.73.23.0", {"center": v(401.5, -126.5) * mm, "radius": 2.5 * mm});
            skCircle(sketch, "E1.73.24.0", {"center": v(401.5, -132) * mm, "radius": 2.5 * mm});
            skCircle(sketch, "E1.74.0.0", {"center": v(407, 0) * mm, "radius": 2.5 * mm});
            skCircle(sketch, "E1.74.1.0", {"center": v(407, -5.5) * mm, "radius": 2.5 * mm});
            skCircle(sketch, "E1.74.2.0", {"center": v(407, -11) * mm, "radius": 2.5 * mm});
            skCircle(sketch, "E1.74.3.0", {"center": v(407, -16.5) * mm, "radius": 2.5 * mm});
            skCircle(sketch, "E1.74.4.0", {"center": v(407, -22) * mm, "radius": 2.5 * mm});
            skCircle(sketch, "E1.74.5.0", {"center": v(407, -27.5) * mm, "radius": 2.5 * mm});
            skCircle(sketch, "E1.74.6.0", {"center": v(407, -33) * mm, "radius": 2.5 * mm});
            skCircle(sketch, "E1.74.7.0", {"center": v(407, -38.5) * mm, "radius": 2.5 * mm});
            skCircle(sketch, "E1.74.8.0", {"center": v(407, -44) * mm, "radius": 2.5 * mm});
            skCircle(sketch, "E1.74.9.0", {"center": v(407, -49.5) * mm, "radius": 2.5 * mm});
            skCircle(sketch, "E1.74.10.0", {"center": v(407, -55) * mm, "radius": 2.5 * mm});
            skCircle(sketch, "E1.74.11.0", {"center": v(407, -60.5) * mm, "radius": 2.5 * mm});
            skCircle(sketch, "E1.74.12.0", {"center": v(407, -66) * mm, "radius": 2.5 * mm});
            skCircle(sketch, "E1.74.13.0", {"center": v(407, -71.5) * mm, "radius": 2.5 * mm});
            skCircle(sketch, "E1.74.14.0", {"center": v(407, -77) * mm, "radius": 2.5 * mm});
            skCircle(sketch, "E1.74.15.0", {"center": v(407, -82.5) * mm, "radius": 2.5 * mm});
            skCircle(sketch, "E1.74.16.0", {"center": v(407, -88) * mm, "radius": 2.5 * mm});
            skCircle(sketch, "E1.74.17.0", {"center": v(407, -93.5) * mm, "radius": 2.5 * mm});
            skCircle(sketch, "E1.74.18.0", {"center": v(407, -99) * mm, "radius": 2.5 * mm});
            skCircle(sketch, "E1.74.19.0", {"center": v(407, -104.5) * mm, "radius": 2.5 * mm});
            skCircle(sketch, "E1.74.20.0", {"center": v(407, -110) * mm, "radius": 2.5 * mm});
            skCircle(sketch, "E1.74.21.0", {"center": v(407, -115.5) * mm, "radius": 2.5 * mm});
            skCircle(sketch, "E1.74.22.0", {"center": v(407, -121) * mm, "radius": 2.5 * mm});
            skCircle(sketch, "E1.74.23.0", {"center": v(407, -126.5) * mm, "radius": 2.5 * mm});
            skCircle(sketch, "E1.74.24.0", {"center": v(407, -132) * mm, "radius": 2.5 * mm});
            skCircle(sketch, "E1.75.0.0", {"center": v(412.5, 0) * mm, "radius": 2.5 * mm});
            skCircle(sketch, "E1.75.1.0", {"center": v(412.5, -5.5) * mm, "radius": 2.5 * mm});
            skCircle(sketch, "E1.75.2.0", {"center": v(412.5, -11) * mm, "radius": 2.5 * mm});
            skCircle(sketch, "E1.75.3.0", {"center": v(412.5, -16.5) * mm, "radius": 2.5 * mm});
            skCircle(sketch, "E1.75.4.0", {"center": v(412.5, -22) * mm, "radius": 2.5 * mm});
            skCircle(sketch, "E1.75.5.0", {"center": v(412.5, -27.5) * mm, "radius": 2.5 * mm});
            skCircle(sketch, "E1.75.6.0", {"center": v(412.5, -33) * mm, "radius": 2.5 * mm});
            skCircle(sketch, "E1.75.7.0", {"center": v(412.5, -38.5) * mm, "radius": 2.5 * mm});
            skCircle(sketch, "E1.75.8.0", {"center": v(412.5, -44) * mm, "radius": 2.5 * mm});
            skCircle(sketch, "E1.75.9.0", {"center": v(412.5, -49.5) * mm, "radius": 2.5 * mm});
            skCircle(sketch, "E1.75.10.0", {"center": v(412.5, -55) * mm, "radius": 2.5 * mm});
            skCircle(sketch, "E1.75.11.0", {"center": v(412.5, -60.5) * mm, "radius": 2.5 * mm});
            skCircle(sketch, "E1.75.12.0", {"center": v(412.5, -66) * mm, "radius": 2.5 * mm});
            skCircle(sketch, "E1.75.13.0", {"center": v(412.5, -71.5) * mm, "radius": 2.5 * mm});
            skCircle(sketch, "E1.75.14.0", {"center": v(412.5, -77) * mm, "radius": 2.5 * mm});
            skCircle(sketch, "E1.75.15.0", {"center": v(412.5, -82.5) * mm, "radius": 2.5 * mm});
            skCircle(sketch, "E1.75.16.0", {"center": v(412.5, -88) * mm, "radius": 2.5 * mm});
            skCircle(sketch, "E1.75.17.0", {"center": v(412.5, -93.5) * mm, "radius": 2.5 * mm});
            skCircle(sketch, "E1.75.18.0", {"center": v(412.5, -99) * mm, "radius": 2.5 * mm});
            skCircle(sketch, "E1.75.19.0", {"center": v(412.5, -104.5) * mm, "radius": 2.5 * mm});
            skCircle(sketch, "E1.75.20.0", {"center": v(412.5, -110) * mm, "radius": 2.5 * mm});
            skCircle(sketch, "E1.75.21.0", {"center": v(412.5, -115.5) * mm, "radius": 2.5 * mm});
            skCircle(sketch, "E1.75.22.0", {"center": v(412.5, -121) * mm, "radius": 2.5 * mm});
            skCircle(sketch, "E1.75.23.0", {"center": v(412.5, -126.5) * mm, "radius": 2.5 * mm});
            skCircle(sketch, "E1.75.24.0", {"center": v(412.5, -132) * mm, "radius": 2.5 * mm});
            skCircle(sketch, "E1.76.0.0", {"center": v(418, 0) * mm, "radius": 2.5 * mm});
            skCircle(sketch, "E1.76.1.0", {"center": v(418, -5.5) * mm, "radius": 2.5 * mm});
            skCircle(sketch, "E1.76.2.0", {"center": v(418, -11) * mm, "radius": 2.5 * mm});
            skCircle(sketch, "E1.76.3.0", {"center": v(418, -16.5) * mm, "radius": 2.5 * mm});
            skCircle(sketch, "E1.76.4.0", {"center": v(418, -22) * mm, "radius": 2.5 * mm});
            skCircle(sketch, "E1.76.5.0", {"center": v(418, -27.5) * mm, "radius": 2.5 * mm});
            skCircle(sketch, "E1.76.6.0", {"center": v(418, -33) * mm, "radius": 2.5 * mm});
            skCircle(sketch, "E1.76.7.0", {"center": v(418, -38.5) * mm, "radius": 2.5 * mm});
            skCircle(sketch, "E1.76.8.0", {"center": v(418, -44) * mm, "radius": 2.5 * mm});
            skCircle(sketch, "E1.76.9.0", {"center": v(418, -49.5) * mm, "radius": 2.5 * mm});
            skCircle(sketch, "E1.76.10.0", {"center": v(418, -55) * mm, "radius": 2.5 * mm});
            skCircle(sketch, "E1.76.11.0", {"center": v(418, -60.5) * mm, "radius": 2.5 * mm});
            skCircle(sketch, "E1.76.12.0", {"center": v(418, -66) * mm, "radius": 2.5 * mm});
            skCircle(sketch, "E1.76.13.0", {"center": v(418, -71.5) * mm, "radius": 2.5 * mm});
            skCircle(sketch, "E1.76.14.0", {"center": v(418, -77) * mm, "radius": 2.5 * mm});
            skCircle(sketch, "E1.76.15.0", {"center": v(418, -82.5) * mm, "radius": 2.5 * mm});
            skCircle(sketch, "E1.76.16.0", {"center": v(418, -88) * mm, "radius": 2.5 * mm});
            skCircle(sketch, "E1.76.17.0", {"center": v(418, -93.5) * mm, "radius": 2.5 * mm});
            skCircle(sketch, "E1.76.18.0", {"center": v(418, -99) * mm, "radius": 2.5 * mm});
            skCircle(sketch, "E1.76.19.0", {"center": v(418, -104.5) * mm, "radius": 2.5 * mm});
            skCircle(sketch, "E1.76.20.0", {"center": v(418, -110) * mm, "radius": 2.5 * mm});
            skCircle(sketch, "E1.76.21.0", {"center": v(418, -115.5) * mm, "radius": 2.5 * mm});
            skCircle(sketch, "E1.76.22.0", {"center": v(418, -121) * mm, "radius": 2.5 * mm});
            skCircle(sketch, "E1.76.23.0", {"center": v(418, -126.5) * mm, "radius": 2.5 * mm});
            skCircle(sketch, "E1.76.24.0", {"center": v(418, -132) * mm, "radius": 2.5 * mm});
            skCircle(sketch, "E1.77.0.0", {"center": v(423.5, 0) * mm, "radius": 2.5 * mm});
            skCircle(sketch, "E1.77.1.0", {"center": v(423.5, -5.5) * mm, "radius": 2.5 * mm});
            skCircle(sketch, "E1.77.2.0", {"center": v(423.5, -11) * mm, "radius": 2.5 * mm});
            skCircle(sketch, "E1.77.3.0", {"center": v(423.5, -16.5) * mm, "radius": 2.5 * mm});
            skCircle(sketch, "E1.77.4.0", {"center": v(423.5, -22) * mm, "radius": 2.5 * mm});
            skCircle(sketch, "E1.77.5.0", {"center": v(423.5, -27.5) * mm, "radius": 2.5 * mm});
            skCircle(sketch, "E1.77.6.0", {"center": v(423.5, -33) * mm, "radius": 2.5 * mm});
            skCircle(sketch, "E1.77.7.0", {"center": v(423.5, -38.5) * mm, "radius": 2.5 * mm});
            skCircle(sketch, "E1.77.8.0", {"center": v(423.5, -44) * mm, "radius": 2.5 * mm});
            skCircle(sketch, "E1.77.9.0", {"center": v(423.5, -49.5) * mm, "radius": 2.5 * mm});
            skCircle(sketch, "E1.77.10.0", {"center": v(423.5, -55) * mm, "radius": 2.5 * mm});
            skCircle(sketch, "E1.77.11.0", {"center": v(423.5, -60.5) * mm, "radius": 2.5 * mm});
            skCircle(sketch, "E1.77.12.0", {"center": v(423.5, -66) * mm, "radius": 2.5 * mm});
            skCircle(sketch, "E1.77.13.0", {"center": v(423.5, -71.5) * mm, "radius": 2.5 * mm});
            skCircle(sketch, "E1.77.14.0", {"center": v(423.5, -77) * mm, "radius": 2.5 * mm});
            skCircle(sketch, "E1.77.15.0", {"center": v(423.5, -82.5) * mm, "radius": 2.5 * mm});
            skCircle(sketch, "E1.77.16.0", {"center": v(423.5, -88) * mm, "radius": 2.5 * mm});
            skCircle(sketch, "E1.77.17.0", {"center": v(423.5, -93.5) * mm, "radius": 2.5 * mm});
            skCircle(sketch, "E1.77.18.0", {"center": v(423.5, -99) * mm, "radius": 2.5 * mm});
            skCircle(sketch, "E1.77.19.0", {"center": v(423.5, -104.5) * mm, "radius": 2.5 * mm});
            skCircle(sketch, "E1.77.20.0", {"center": v(423.5, -110) * mm, "radius": 2.5 * mm});
            skCircle(sketch, "E1.77.21.0", {"center": v(423.5, -115.5) * mm, "radius": 2.5 * mm});
            skCircle(sketch, "E1.77.22.0", {"center": v(423.5, -121) * mm, "radius": 2.5 * mm});
            skCircle(sketch, "E1.77.23.0", {"center": v(423.5, -126.5) * mm, "radius": 2.5 * mm});
            skCircle(sketch, "E1.77.24.0", {"center": v(423.5, -132) * mm, "radius": 2.5 * mm});
            skCircle(sketch, "E1.78.0.0", {"center": v(429, 0) * mm, "radius": 2.5 * mm});
            skCircle(sketch, "E1.78.1.0", {"center": v(429, -5.5) * mm, "radius": 2.5 * mm});
            skCircle(sketch, "E1.78.2.0", {"center": v(429, -11) * mm, "radius": 2.5 * mm});
            skCircle(sketch, "E1.78.3.0", {"center": v(429, -16.5) * mm, "radius": 2.5 * mm});
            skCircle(sketch, "E1.78.4.0", {"center": v(429, -22) * mm, "radius": 2.5 * mm});
            skCircle(sketch, "E1.78.5.0", {"center": v(429, -27.5) * mm, "radius": 2.5 * mm});
            skCircle(sketch, "E1.78.6.0", {"center": v(429, -33) * mm, "radius": 2.5 * mm});
            skCircle(sketch, "E1.78.7.0", {"center": v(429, -38.5) * mm, "radius": 2.5 * mm});
            skCircle(sketch, "E1.78.8.0", {"center": v(429, -44) * mm, "radius": 2.5 * mm});
            skCircle(sketch, "E1.78.9.0", {"center": v(429, -49.5) * mm, "radius": 2.5 * mm});
            skCircle(sketch, "E1.78.10.0", {"center": v(429, -55) * mm, "radius": 2.5 * mm});
            skCircle(sketch, "E1.78.11.0", {"center": v(429, -60.5) * mm, "radius": 2.5 * mm});
            skCircle(sketch, "E1.78.12.0", {"center": v(429, -66) * mm, "radius": 2.5 * mm});
            skCircle(sketch, "E1.78.13.0", {"center": v(429, -71.5) * mm, "radius": 2.5 * mm});
            skCircle(sketch, "E1.78.14.0", {"center": v(429, -77) * mm, "radius": 2.5 * mm});
            skCircle(sketch, "E1.78.15.0", {"center": v(429, -82.5) * mm, "radius": 2.5 * mm});
            skCircle(sketch, "E1.78.16.0", {"center": v(429, -88) * mm, "radius": 2.5 * mm});
            skCircle(sketch, "E1.78.17.0", {"center": v(429, -93.5) * mm, "radius": 2.5 * mm});
            skCircle(sketch, "E1.78.18.0", {"center": v(429, -99) * mm, "radius": 2.5 * mm});
            skCircle(sketch, "E1.78.19.0", {"center": v(429, -104.5) * mm, "radius": 2.5 * mm});
            skCircle(sketch, "E1.78.20.0", {"center": v(429, -110) * mm, "radius": 2.5 * mm});
            skCircle(sketch, "E1.78.21.0", {"center": v(429, -115.5) * mm, "radius": 2.5 * mm});
            skCircle(sketch, "E1.78.22.0", {"center": v(429, -121) * mm, "radius": 2.5 * mm});
            skCircle(sketch, "E1.78.23.0", {"center": v(429, -126.5) * mm, "radius": 2.5 * mm});
            skCircle(sketch, "E1.78.24.0", {"center": v(429, -132) * mm, "radius": 2.5 * mm});
            skCircle(sketch, "E1.79.0.0", {"center": v(434.5, 0) * mm, "radius": 2.5 * mm});
            skCircle(sketch, "E1.79.1.0", {"center": v(434.5, -5.5) * mm, "radius": 2.5 * mm});
            skCircle(sketch, "E1.79.2.0", {"center": v(434.5, -11) * mm, "radius": 2.5 * mm});
            skCircle(sketch, "E1.79.3.0", {"center": v(434.5, -16.5) * mm, "radius": 2.5 * mm});
            skCircle(sketch, "E1.79.4.0", {"center": v(434.5, -22) * mm, "radius": 2.5 * mm});
            skCircle(sketch, "E1.79.5.0", {"center": v(434.5, -27.5) * mm, "radius": 2.5 * mm});
            skCircle(sketch, "E1.79.6.0", {"center": v(434.5, -33) * mm, "radius": 2.5 * mm});
            skCircle(sketch, "E1.79.7.0", {"center": v(434.5, -38.5) * mm, "radius": 2.5 * mm});
            skCircle(sketch, "E1.79.8.0", {"center": v(434.5, -44) * mm, "radius": 2.5 * mm});
            skCircle(sketch, "E1.79.9.0", {"center": v(434.5, -49.5) * mm, "radius": 2.5 * mm});
            skCircle(sketch, "E1.79.10.0", {"center": v(434.5, -55) * mm, "radius": 2.5 * mm});
            skCircle(sketch, "E1.79.11.0", {"center": v(434.5, -60.5) * mm, "radius": 2.5 * mm});
            skCircle(sketch, "E1.79.12.0", {"center": v(434.5, -66) * mm, "radius": 2.5 * mm});
            skCircle(sketch, "E1.79.13.0", {"center": v(434.5, -71.5) * mm, "radius": 2.5 * mm});
            skCircle(sketch, "E1.79.14.0", {"center": v(434.5, -77) * mm, "radius": 2.5 * mm});
            skCircle(sketch, "E1.79.15.0", {"center": v(434.5, -82.5) * mm, "radius": 2.5 * mm});
            skCircle(sketch, "E1.79.16.0", {"center": v(434.5, -88) * mm, "radius": 2.5 * mm});
            skCircle(sketch, "E1.79.17.0", {"center": v(434.5, -93.5) * mm, "radius": 2.5 * mm});
            skCircle(sketch, "E1.79.18.0", {"center": v(434.5, -99) * mm, "radius": 2.5 * mm});
            skCircle(sketch, "E1.79.19.0", {"center": v(434.5, -104.5) * mm, "radius": 2.5 * mm});
            skCircle(sketch, "E1.79.20.0", {"center": v(434.5, -110) * mm, "radius": 2.5 * mm});
            skCircle(sketch, "E1.79.21.0", {"center": v(434.5, -115.5) * mm, "radius": 2.5 * mm});
            skCircle(sketch, "E1.79.22.0", {"center": v(434.5, -121) * mm, "radius": 2.5 * mm});
            skCircle(sketch, "E1.79.23.0", {"center": v(434.5, -126.5) * mm, "radius": 2.5 * mm});
            skCircle(sketch, "E1.79.24.0", {"center": v(434.5, -132) * mm, "radius": 2.5 * mm});
            skCircle(sketch, "E1.80.0.0", {"center": v(440, 0) * mm, "radius": 2.5 * mm});
            skCircle(sketch, "E1.80.1.0", {"center": v(440, -5.5) * mm, "radius": 2.5 * mm});
            skCircle(sketch, "E1.80.2.0", {"center": v(440, -11) * mm, "radius": 2.5 * mm});
            skCircle(sketch, "E1.80.3.0", {"center": v(440, -16.5) * mm, "radius": 2.5 * mm});
            skCircle(sketch, "E1.80.4.0", {"center": v(440, -22) * mm, "radius": 2.5 * mm});
            skCircle(sketch, "E1.80.5.0", {"center": v(440, -27.5) * mm, "radius": 2.5 * mm});
            skCircle(sketch, "E1.80.6.0", {"center": v(440, -33) * mm, "radius": 2.5 * mm});
            skCircle(sketch, "E1.80.7.0", {"center": v(440, -38.5) * mm, "radius": 2.5 * mm});
            skCircle(sketch, "E1.80.8.0", {"center": v(440, -44) * mm, "radius": 2.5 * mm});
            skCircle(sketch, "E1.80.9.0", {"center": v(440, -49.5) * mm, "radius": 2.5 * mm});
            skCircle(sketch, "E1.80.10.0", {"center": v(440, -55) * mm, "radius": 2.5 * mm});
            skCircle(sketch, "E1.80.11.0", {"center": v(440, -60.5) * mm, "radius": 2.5 * mm});
            skCircle(sketch, "E1.80.12.0", {"center": v(440, -66) * mm, "radius": 2.5 * mm});
            skCircle(sketch, "E1.80.13.0", {"center": v(440, -71.5) * mm, "radius": 2.5 * mm});
            skCircle(sketch, "E1.80.14.0", {"center": v(440, -77) * mm, "radius": 2.5 * mm});
            skCircle(sketch, "E1.80.15.0", {"center": v(440, -82.5) * mm, "radius": 2.5 * mm});
            skCircle(sketch, "E1.80.16.0", {"center": v(440, -88) * mm, "radius": 2.5 * mm});
            skCircle(sketch, "E1.80.17.0", {"center": v(440, -93.5) * mm, "radius": 2.5 * mm});
            skCircle(sketch, "E1.80.18.0", {"center": v(440, -99) * mm, "radius": 2.5 * mm});
            skCircle(sketch, "E1.80.19.0", {"center": v(440, -104.5) * mm, "radius": 2.5 * mm});
            skCircle(sketch, "E1.80.20.0", {"center": v(440, -110) * mm, "radius": 2.5 * mm});
            skCircle(sketch, "E1.80.21.0", {"center": v(440, -115.5) * mm, "radius": 2.5 * mm});
            skCircle(sketch, "E1.80.22.0", {"center": v(440, -121) * mm, "radius": 2.5 * mm});
            skCircle(sketch, "E1.80.23.0", {"center": v(440, -126.5) * mm, "radius": 2.5 * mm});
            skCircle(sketch, "E1.80.24.0", {"center": v(440, -132) * mm, "radius": 2.5 * mm});
            skCircle(sketch, "E1.81.0.0", {"center": v(445.5, 0) * mm, "radius": 2.5 * mm});
            skCircle(sketch, "E1.81.1.0", {"center": v(445.5, -5.5) * mm, "radius": 2.5 * mm});
            skCircle(sketch, "E1.81.2.0", {"center": v(445.5, -11) * mm, "radius": 2.5 * mm});
            skCircle(sketch, "E1.81.3.0", {"center": v(445.5, -16.5) * mm, "radius": 2.5 * mm});
            skCircle(sketch, "E1.81.4.0", {"center": v(445.5, -22) * mm, "radius": 2.5 * mm});
            skCircle(sketch, "E1.81.5.0", {"center": v(445.5, -27.5) * mm, "radius": 2.5 * mm});
            skCircle(sketch, "E1.81.6.0", {"center": v(445.5, -33) * mm, "radius": 2.5 * mm});
            skCircle(sketch, "E1.81.7.0", {"center": v(445.5, -38.5) * mm, "radius": 2.5 * mm});
            skCircle(sketch, "E1.81.8.0", {"center": v(445.5, -44) * mm, "radius": 2.5 * mm});
            skCircle(sketch, "E1.81.9.0", {"center": v(445.5, -49.5) * mm, "radius": 2.5 * mm});
            skCircle(sketch, "E1.81.10.0", {"center": v(445.5, -55) * mm, "radius": 2.5 * mm});
            skCircle(sketch, "E1.81.11.0", {"center": v(445.5, -60.5) * mm, "radius": 2.5 * mm});
            skCircle(sketch, "E1.81.12.0", {"center": v(445.5, -66) * mm, "radius": 2.5 * mm});
            skCircle(sketch, "E1.81.13.0", {"center": v(445.5, -71.5) * mm, "radius": 2.5 * mm});
            skCircle(sketch, "E1.81.14.0", {"center": v(445.5, -77) * mm, "radius": 2.5 * mm});
            skCircle(sketch, "E1.81.15.0", {"center": v(445.5, -82.5) * mm, "radius": 2.5 * mm});
            skCircle(sketch, "E1.81.16.0", {"center": v(445.5, -88) * mm, "radius": 2.5 * mm});
            skCircle(sketch, "E1.81.17.0", {"center": v(445.5, -93.5) * mm, "radius": 2.5 * mm});
            skCircle(sketch, "E1.81.18.0", {"center": v(445.5, -99) * mm, "radius": 2.5 * mm});
            skCircle(sketch, "E1.81.19.0", {"center": v(445.5, -104.5) * mm, "radius": 2.5 * mm});
            skCircle(sketch, "E1.81.20.0", {"center": v(445.5, -110) * mm, "radius": 2.5 * mm});
            skCircle(sketch, "E1.81.21.0", {"center": v(445.5, -115.5) * mm, "radius": 2.5 * mm});
            skCircle(sketch, "E1.81.22.0", {"center": v(445.5, -121) * mm, "radius": 2.5 * mm});
            skCircle(sketch, "E1.81.23.0", {"center": v(445.5, -126.5) * mm, "radius": 2.5 * mm});
            skCircle(sketch, "E1.81.24.0", {"center": v(445.5, -132) * mm, "radius": 2.5 * mm});
            skCircle(sketch, "E1.82.0.0", {"center": v(451, 0) * mm, "radius": 2.5 * mm});
            skCircle(sketch, "E1.82.1.0", {"center": v(451, -5.5) * mm, "radius": 2.5 * mm});
            skCircle(sketch, "E1.82.2.0", {"center": v(451, -11) * mm, "radius": 2.5 * mm});
            skCircle(sketch, "E1.82.3.0", {"center": v(451, -16.5) * mm, "radius": 2.5 * mm});
            skCircle(sketch, "E1.82.4.0", {"center": v(451, -22) * mm, "radius": 2.5 * mm});
            skCircle(sketch, "E1.82.5.0", {"center": v(451, -27.5) * mm, "radius": 2.5 * mm});
            skCircle(sketch, "E1.82.6.0", {"center": v(451, -33) * mm, "radius": 2.5 * mm});
            skCircle(sketch, "E1.82.7.0", {"center": v(451, -38.5) * mm, "radius": 2.5 * mm});
            skCircle(sketch, "E1.82.8.0", {"center": v(451, -44) * mm, "radius": 2.5 * mm});
            skCircle(sketch, "E1.82.9.0", {"center": v(451, -49.5) * mm, "radius": 2.5 * mm});
            skCircle(sketch, "E1.82.10.0", {"center": v(451, -55) * mm, "radius": 2.5 * mm});
            skCircle(sketch, "E1.82.11.0", {"center": v(451, -60.5) * mm, "radius": 2.5 * mm});
            skCircle(sketch, "E1.82.12.0", {"center": v(451, -66) * mm, "radius": 2.5 * mm});
            skCircle(sketch, "E1.82.13.0", {"center": v(451, -71.5) * mm, "radius": 2.5 * mm});
            skCircle(sketch, "E1.82.14.0", {"center": v(451, -77) * mm, "radius": 2.5 * mm});
            skCircle(sketch, "E1.82.15.0", {"center": v(451, -82.5) * mm, "radius": 2.5 * mm});
            skCircle(sketch, "E1.82.16.0", {"center": v(451, -88) * mm, "radius": 2.5 * mm});
            skCircle(sketch, "E1.82.17.0", {"center": v(451, -93.5) * mm, "radius": 2.5 * mm});
            skCircle(sketch, "E1.82.18.0", {"center": v(451, -99) * mm, "radius": 2.5 * mm});
            skCircle(sketch, "E1.82.19.0", {"center": v(451, -104.5) * mm, "radius": 2.5 * mm});
            skCircle(sketch, "E1.82.20.0", {"center": v(451, -110) * mm, "radius": 2.5 * mm});
            skCircle(sketch, "E1.82.21.0", {"center": v(451, -115.5) * mm, "radius": 2.5 * mm});
            skCircle(sketch, "E1.82.22.0", {"center": v(451, -121) * mm, "radius": 2.5 * mm});
            skCircle(sketch, "E1.82.23.0", {"center": v(451, -126.5) * mm, "radius": 2.5 * mm});
            skCircle(sketch, "E1.82.24.0", {"center": v(451, -132) * mm, "radius": 2.5 * mm});
            skCircle(sketch, "E1.83.0.0", {"center": v(456.5, 0) * mm, "radius": 2.5 * mm});
            skCircle(sketch, "E1.83.1.0", {"center": v(456.5, -5.5) * mm, "radius": 2.5 * mm});
            skCircle(sketch, "E1.83.2.0", {"center": v(456.5, -11) * mm, "radius": 2.5 * mm});
            skCircle(sketch, "E1.83.3.0", {"center": v(456.5, -16.5) * mm, "radius": 2.5 * mm});
            skCircle(sketch, "E1.83.4.0", {"center": v(456.5, -22) * mm, "radius": 2.5 * mm});
            skCircle(sketch, "E1.83.5.0", {"center": v(456.5, -27.5) * mm, "radius": 2.5 * mm});
            skCircle(sketch, "E1.83.6.0", {"center": v(456.5, -33) * mm, "radius": 2.5 * mm});
            skCircle(sketch, "E1.83.7.0", {"center": v(456.5, -38.5) * mm, "radius": 2.5 * mm});
            skCircle(sketch, "E1.83.8.0", {"center": v(456.5, -44) * mm, "radius": 2.5 * mm});
            skCircle(sketch, "E1.83.9.0", {"center": v(456.5, -49.5) * mm, "radius": 2.5 * mm});
            skCircle(sketch, "E1.83.10.0", {"center": v(456.5, -55) * mm, "radius": 2.5 * mm});
            skCircle(sketch, "E1.83.11.0", {"center": v(456.5, -60.5) * mm, "radius": 2.5 * mm});
            skCircle(sketch, "E1.83.12.0", {"center": v(456.5, -66) * mm, "radius": 2.5 * mm});
            skCircle(sketch, "E1.83.13.0", {"center": v(456.5, -71.5) * mm, "radius": 2.5 * mm});
            skCircle(sketch, "E1.83.14.0", {"center": v(456.5, -77) * mm, "radius": 2.5 * mm});
            skCircle(sketch, "E1.83.15.0", {"center": v(456.5, -82.5) * mm, "radius": 2.5 * mm});
            skCircle(sketch, "E1.83.16.0", {"center": v(456.5, -88) * mm, "radius": 2.5 * mm});
            skCircle(sketch, "E1.83.17.0", {"center": v(456.5, -93.5) * mm, "radius": 2.5 * mm});
            skCircle(sketch, "E1.83.18.0", {"center": v(456.5, -99) * mm, "radius": 2.5 * mm});
            skCircle(sketch, "E1.83.19.0", {"center": v(456.5, -104.5) * mm, "radius": 2.5 * mm});
            skCircle(sketch, "E1.83.20.0", {"center": v(456.5, -110) * mm, "radius": 2.5 * mm});
            skCircle(sketch, "E1.83.21.0", {"center": v(456.5, -115.5) * mm, "radius": 2.5 * mm});
            skCircle(sketch, "E1.83.22.0", {"center": v(456.5, -121) * mm, "radius": 2.5 * mm});
            skCircle(sketch, "E1.83.23.0", {"center": v(456.5, -126.5) * mm, "radius": 2.5 * mm});
            skCircle(sketch, "E1.83.24.0", {"center": v(456.5, -132) * mm, "radius": 2.5 * mm});
            skCircle(sketch, "E1.84.0.0", {"center": v(462, 0) * mm, "radius": 2.5 * mm});
            skCircle(sketch, "E1.84.1.0", {"center": v(462, -5.5) * mm, "radius": 2.5 * mm});
            skCircle(sketch, "E1.84.2.0", {"center": v(462, -11) * mm, "radius": 2.5 * mm});
            skCircle(sketch, "E1.84.3.0", {"center": v(462, -16.5) * mm, "radius": 2.5 * mm});
            skCircle(sketch, "E1.84.4.0", {"center": v(462, -22) * mm, "radius": 2.5 * mm});
            skCircle(sketch, "E1.84.5.0", {"center": v(462, -27.5) * mm, "radius": 2.5 * mm});
            skCircle(sketch, "E1.84.6.0", {"center": v(462, -33) * mm, "radius": 2.5 * mm});
            skCircle(sketch, "E1.84.7.0", {"center": v(462, -38.5) * mm, "radius": 2.5 * mm});
            skCircle(sketch, "E1.84.8.0", {"center": v(462, -44) * mm, "radius": 2.5 * mm});
            skCircle(sketch, "E1.84.9.0", {"center": v(462, -49.5) * mm, "radius": 2.5 * mm});
            skCircle(sketch, "E1.84.10.0", {"center": v(462, -55) * mm, "radius": 2.5 * mm});
            skCircle(sketch, "E1.84.11.0", {"center": v(462, -60.5) * mm, "radius": 2.5 * mm});
            skCircle(sketch, "E1.84.12.0", {"center": v(462, -66) * mm, "radius": 2.5 * mm});
            skCircle(sketch, "E1.84.13.0", {"center": v(462, -71.5) * mm, "radius": 2.5 * mm});
            skCircle(sketch, "E1.84.14.0", {"center": v(462, -77) * mm, "radius": 2.5 * mm});
            skCircle(sketch, "E1.84.15.0", {"center": v(462, -82.5) * mm, "radius": 2.5 * mm});
            skCircle(sketch, "E1.84.16.0", {"center": v(462, -88) * mm, "radius": 2.5 * mm});
            skCircle(sketch, "E1.84.17.0", {"center": v(462, -93.5) * mm, "radius": 2.5 * mm});
            skCircle(sketch, "E1.84.18.0", {"center": v(462, -99) * mm, "radius": 2.5 * mm});
            skCircle(sketch, "E1.84.19.0", {"center": v(462, -104.5) * mm, "radius": 2.5 * mm});
            skCircle(sketch, "E1.84.20.0", {"center": v(462, -110) * mm, "radius": 2.5 * mm});
            skCircle(sketch, "E1.84.21.0", {"center": v(462, -115.5) * mm, "radius": 2.5 * mm});
            skCircle(sketch, "E1.84.22.0", {"center": v(462, -121) * mm, "radius": 2.5 * mm});
            skCircle(sketch, "E1.84.23.0", {"center": v(462, -126.5) * mm, "radius": 2.5 * mm});
            skCircle(sketch, "E1.84.24.0", {"center": v(462, -132) * mm, "radius": 2.5 * mm});
            skCircle(sketch, "E1.85.0.0", {"center": v(467.5, 0) * mm, "radius": 2.5 * mm});
            skCircle(sketch, "E1.85.1.0", {"center": v(467.5, -5.5) * mm, "radius": 2.5 * mm});
            skCircle(sketch, "E1.85.2.0", {"center": v(467.5, -11) * mm, "radius": 2.5 * mm});
            skCircle(sketch, "E1.85.3.0", {"center": v(467.5, -16.5) * mm, "radius": 2.5 * mm});
            skCircle(sketch, "E1.85.4.0", {"center": v(467.5, -22) * mm, "radius": 2.5 * mm});
            skCircle(sketch, "E1.85.5.0", {"center": v(467.5, -27.5) * mm, "radius": 2.5 * mm});
            skCircle(sketch, "E1.85.6.0", {"center": v(467.5, -33) * mm, "radius": 2.5 * mm});
            skCircle(sketch, "E1.85.7.0", {"center": v(467.5, -38.5) * mm, "radius": 2.5 * mm});
            skCircle(sketch, "E1.85.8.0", {"center": v(467.5, -44) * mm, "radius": 2.5 * mm});
            skCircle(sketch, "E1.85.9.0", {"center": v(467.5, -49.5) * mm, "radius": 2.5 * mm});
            skCircle(sketch, "E1.85.10.0", {"center": v(467.5, -55) * mm, "radius": 2.5 * mm});
            skCircle(sketch, "E1.85.11.0", {"center": v(467.5, -60.5) * mm, "radius": 2.5 * mm});
            skCircle(sketch, "E1.85.12.0", {"center": v(467.5, -66) * mm, "radius": 2.5 * mm});
            skCircle(sketch, "E1.85.13.0", {"center": v(467.5, -71.5) * mm, "radius": 2.5 * mm});
            skCircle(sketch, "E1.85.14.0", {"center": v(467.5, -77) * mm, "radius": 2.5 * mm});
            skCircle(sketch, "E1.85.15.0", {"center": v(467.5, -82.5) * mm, "radius": 2.5 * mm});
            skCircle(sketch, "E1.85.16.0", {"center": v(467.5, -88) * mm, "radius": 2.5 * mm});
            skCircle(sketch, "E1.85.17.0", {"center": v(467.5, -93.5) * mm, "radius": 2.5 * mm});
            skCircle(sketch, "E1.85.18.0", {"center": v(467.5, -99) * mm, "radius": 2.5 * mm});
            skCircle(sketch, "E1.85.19.0", {"center": v(467.5, -104.5) * mm, "radius": 2.5 * mm});
            skCircle(sketch, "E1.85.20.0", {"center": v(467.5, -110) * mm, "radius": 2.5 * mm});
            skCircle(sketch, "E1.85.21.0", {"center": v(467.5, -115.5) * mm, "radius": 2.5 * mm});
            skCircle(sketch, "E1.85.22.0", {"center": v(467.5, -121) * mm, "radius": 2.5 * mm});
            skCircle(sketch, "E1.85.23.0", {"center": v(467.5, -126.5) * mm, "radius": 2.5 * mm});
            skCircle(sketch, "E1.85.24.0", {"center": v(467.5, -132) * mm, "radius": 2.5 * mm});
            skCircle(sketch, "E1.86.0.0", {"center": v(473, 0) * mm, "radius": 2.5 * mm});
            skCircle(sketch, "E1.86.1.0", {"center": v(473, -5.5) * mm, "radius": 2.5 * mm});
            skCircle(sketch, "E1.86.2.0", {"center": v(473, -11) * mm, "radius": 2.5 * mm});
            skCircle(sketch, "E1.86.3.0", {"center": v(473, -16.5) * mm, "radius": 2.5 * mm});
            skCircle(sketch, "E1.86.4.0", {"center": v(473, -22) * mm, "radius": 2.5 * mm});
            skCircle(sketch, "E1.86.5.0", {"center": v(473, -27.5) * mm, "radius": 2.5 * mm});
            skCircle(sketch, "E1.86.6.0", {"center": v(473, -33) * mm, "radius": 2.5 * mm});
            skCircle(sketch, "E1.86.7.0", {"center": v(473, -38.5) * mm, "radius": 2.5 * mm});
            skCircle(sketch, "E1.86.8.0", {"center": v(473, -44) * mm, "radius": 2.5 * mm});
            skCircle(sketch, "E1.86.9.0", {"center": v(473, -49.5) * mm, "radius": 2.5 * mm});
            skCircle(sketch, "E1.86.10.0", {"center": v(473, -55) * mm, "radius": 2.5 * mm});
            skCircle(sketch, "E1.86.11.0", {"center": v(473, -60.5) * mm, "radius": 2.5 * mm});
            skCircle(sketch, "E1.86.12.0", {"center": v(473, -66) * mm, "radius": 2.5 * mm});
            skCircle(sketch, "E1.86.13.0", {"center": v(473, -71.5) * mm, "radius": 2.5 * mm});
            skCircle(sketch, "E1.86.14.0", {"center": v(473, -77) * mm, "radius": 2.5 * mm});
            skCircle(sketch, "E1.86.15.0", {"center": v(473, -82.5) * mm, "radius": 2.5 * mm});
            skCircle(sketch, "E1.86.16.0", {"center": v(473, -88) * mm, "radius": 2.5 * mm});
            skCircle(sketch, "E1.86.17.0", {"center": v(473, -93.5) * mm, "radius": 2.5 * mm});
            skCircle(sketch, "E1.86.18.0", {"center": v(473, -99) * mm, "radius": 2.5 * mm});
            skCircle(sketch, "E1.86.19.0", {"center": v(473, -104.5) * mm, "radius": 2.5 * mm});
            skCircle(sketch, "E1.86.20.0", {"center": v(473, -110) * mm, "radius": 2.5 * mm});
            skCircle(sketch, "E1.86.21.0", {"center": v(473, -115.5) * mm, "radius": 2.5 * mm});
            skCircle(sketch, "E1.86.22.0", {"center": v(473, -121) * mm, "radius": 2.5 * mm});
            skCircle(sketch, "E1.86.23.0", {"center": v(473, -126.5) * mm, "radius": 2.5 * mm});
            skCircle(sketch, "E1.86.24.0", {"center": v(473, -132) * mm, "radius": 2.5 * mm});
            skCircle(sketch, "E1.87.0.0", {"center": v(478.5, 0) * mm, "radius": 2.5 * mm});
            skCircle(sketch, "E1.87.1.0", {"center": v(478.5, -5.5) * mm, "radius": 2.5 * mm});
            skCircle(sketch, "E1.87.2.0", {"center": v(478.5, -11) * mm, "radius": 2.5 * mm});
            skCircle(sketch, "E1.87.3.0", {"center": v(478.5, -16.5) * mm, "radius": 2.5 * mm});
            skCircle(sketch, "E1.87.4.0", {"center": v(478.5, -22) * mm, "radius": 2.5 * mm});
            skCircle(sketch, "E1.87.5.0", {"center": v(478.5, -27.5) * mm, "radius": 2.5 * mm});
            skCircle(sketch, "E1.87.6.0", {"center": v(478.5, -33) * mm, "radius": 2.5 * mm});
            skCircle(sketch, "E1.87.7.0", {"center": v(478.5, -38.5) * mm, "radius": 2.5 * mm});
            skCircle(sketch, "E1.87.8.0", {"center": v(478.5, -44) * mm, "radius": 2.5 * mm});
            skCircle(sketch, "E1.87.9.0", {"center": v(478.5, -49.5) * mm, "radius": 2.5 * mm});
            skCircle(sketch, "E1.87.10.0", {"center": v(478.5, -55) * mm, "radius": 2.5 * mm});
            skCircle(sketch, "E1.87.11.0", {"center": v(478.5, -60.5) * mm, "radius": 2.5 * mm});
            skCircle(sketch, "E1.87.12.0", {"center": v(478.5, -66) * mm, "radius": 2.5 * mm});
            skCircle(sketch, "E1.87.13.0", {"center": v(478.5, -71.5) * mm, "radius": 2.5 * mm});
            skCircle(sketch, "E1.87.14.0", {"center": v(478.5, -77) * mm, "radius": 2.5 * mm});
            skCircle(sketch, "E1.87.15.0", {"center": v(478.5, -82.5) * mm, "radius": 2.5 * mm});
            skCircle(sketch, "E1.87.16.0", {"center": v(478.5, -88) * mm, "radius": 2.5 * mm});
            skCircle(sketch, "E1.87.17.0", {"center": v(478.5, -93.5) * mm, "radius": 2.5 * mm});
            skCircle(sketch, "E1.87.18.0", {"center": v(478.5, -99) * mm, "radius": 2.5 * mm});
            skCircle(sketch, "E1.87.19.0", {"center": v(478.5, -104.5) * mm, "radius": 2.5 * mm});
            skCircle(sketch, "E1.87.20.0", {"center": v(478.5, -110) * mm, "radius": 2.5 * mm});
            skCircle(sketch, "E1.87.21.0", {"center": v(478.5, -115.5) * mm, "radius": 2.5 * mm});
            skCircle(sketch, "E1.87.22.0", {"center": v(478.5, -121) * mm, "radius": 2.5 * mm});
            skCircle(sketch, "E1.87.23.0", {"center": v(478.5, -126.5) * mm, "radius": 2.5 * mm});
            skCircle(sketch, "E1.87.24.0", {"center": v(478.5, -132) * mm, "radius": 2.5 * mm});
            skCircle(sketch, "E1.88.0.0", {"center": v(484, 0) * mm, "radius": 2.5 * mm});
            skCircle(sketch, "E1.88.1.0", {"center": v(484, -5.5) * mm, "radius": 2.5 * mm});
            skCircle(sketch, "E1.88.2.0", {"center": v(484, -11) * mm, "radius": 2.5 * mm});
            skCircle(sketch, "E1.88.3.0", {"center": v(484, -16.5) * mm, "radius": 2.5 * mm});
            skCircle(sketch, "E1.88.4.0", {"center": v(484, -22) * mm, "radius": 2.5 * mm});
            skCircle(sketch, "E1.88.5.0", {"center": v(484, -27.5) * mm, "radius": 2.5 * mm});
            skCircle(sketch, "E1.88.6.0", {"center": v(484, -33) * mm, "radius": 2.5 * mm});
            skCircle(sketch, "E1.88.7.0", {"center": v(484, -38.5) * mm, "radius": 2.5 * mm});
            skCircle(sketch, "E1.88.8.0", {"center": v(484, -44) * mm, "radius": 2.5 * mm});
            skCircle(sketch, "E1.88.9.0", {"center": v(484, -49.5) * mm, "radius": 2.5 * mm});
            skCircle(sketch, "E1.88.10.0", {"center": v(484, -55) * mm, "radius": 2.5 * mm});
            skCircle(sketch, "E1.88.11.0", {"center": v(484, -60.5) * mm, "radius": 2.5 * mm});
            skCircle(sketch, "E1.88.12.0", {"center": v(484, -66) * mm, "radius": 2.5 * mm});
            skCircle(sketch, "E1.88.13.0", {"center": v(484, -71.5) * mm, "radius": 2.5 * mm});
            skCircle(sketch, "E1.88.14.0", {"center": v(484, -77) * mm, "radius": 2.5 * mm});
            skCircle(sketch, "E1.88.15.0", {"center": v(484, -82.5) * mm, "radius": 2.5 * mm});
            skCircle(sketch, "E1.88.16.0", {"center": v(484, -88) * mm, "radius": 2.5 * mm});
            skCircle(sketch, "E1.88.17.0", {"center": v(484, -93.5) * mm, "radius": 2.5 * mm});
            skCircle(sketch, "E1.88.18.0", {"center": v(484, -99) * mm, "radius": 2.5 * mm});
            skCircle(sketch, "E1.88.19.0", {"center": v(484, -104.5) * mm, "radius": 2.5 * mm});
            skCircle(sketch, "E1.88.20.0", {"center": v(484, -110) * mm, "radius": 2.5 * mm});
            skCircle(sketch, "E1.88.21.0", {"center": v(484, -115.5) * mm, "radius": 2.5 * mm});
            skCircle(sketch, "E1.88.22.0", {"center": v(484, -121) * mm, "radius": 2.5 * mm});
            skCircle(sketch, "E1.88.23.0", {"center": v(484, -126.5) * mm, "radius": 2.5 * mm});
            skCircle(sketch, "E1.88.24.0", {"center": v(484, -132) * mm, "radius": 2.5 * mm});
            skCircle(sketch, "E1.89.0.0", {"center": v(489.5, 0) * mm, "radius": 2.5 * mm});
            skCircle(sketch, "E1.89.1.0", {"center": v(489.5, -5.5) * mm, "radius": 2.5 * mm});
            skCircle(sketch, "E1.89.2.0", {"center": v(489.5, -11) * mm, "radius": 2.5 * mm});
            skCircle(sketch, "E1.89.3.0", {"center": v(489.5, -16.5) * mm, "radius": 2.5 * mm});
            skCircle(sketch, "E1.89.4.0", {"center": v(489.5, -22) * mm, "radius": 2.5 * mm});
            skCircle(sketch, "E1.89.5.0", {"center": v(489.5, -27.5) * mm, "radius": 2.5 * mm});
            skCircle(sketch, "E1.89.6.0", {"center": v(489.5, -33) * mm, "radius": 2.5 * mm});
            skCircle(sketch, "E1.89.7.0", {"center": v(489.5, -38.5) * mm, "radius": 2.5 * mm});
            skCircle(sketch, "E1.89.8.0", {"center": v(489.5, -44) * mm, "radius": 2.5 * mm});
            skCircle(sketch, "E1.89.9.0", {"center": v(489.5, -49.5) * mm, "radius": 2.5 * mm});
            skCircle(sketch, "E1.89.10.0", {"center": v(489.5, -55) * mm, "radius": 2.5 * mm});
            skCircle(sketch, "E1.89.11.0", {"center": v(489.5, -60.5) * mm, "radius": 2.5 * mm});
            skCircle(sketch, "E1.89.12.0", {"center": v(489.5, -66) * mm, "radius": 2.5 * mm});
            skCircle(sketch, "E1.89.13.0", {"center": v(489.5, -71.5) * mm, "radius": 2.5 * mm});
            skCircle(sketch, "E1.89.14.0", {"center": v(489.5, -77) * mm, "radius": 2.5 * mm});
            skCircle(sketch, "E1.89.15.0", {"center": v(489.5, -82.5) * mm, "radius": 2.5 * mm});
            skCircle(sketch, "E1.89.16.0", {"center": v(489.5, -88) * mm, "radius": 2.5 * mm});
            skCircle(sketch, "E1.89.17.0", {"center": v(489.5, -93.5) * mm, "radius": 2.5 * mm});
            skCircle(sketch, "E1.89.18.0", {"center": v(489.5, -99) * mm, "radius": 2.5 * mm});
            skCircle(sketch, "E1.89.19.0", {"center": v(489.5, -104.5) * mm, "radius": 2.5 * mm});
            skCircle(sketch, "E1.89.20.0", {"center": v(489.5, -110) * mm, "radius": 2.5 * mm});
            skCircle(sketch, "E1.89.21.0", {"center": v(489.5, -115.5) * mm, "radius": 2.5 * mm});
            skCircle(sketch, "E1.89.22.0", {"center": v(489.5, -121) * mm, "radius": 2.5 * mm});
            skCircle(sketch, "E1.89.23.0", {"center": v(489.5, -126.5) * mm, "radius": 2.5 * mm});
            skCircle(sketch, "E1.89.24.0", {"center": v(489.5, -132) * mm, "radius": 2.5 * mm});
            skCircle(sketch, "E1.90.0.0", {"center": v(495, 0) * mm, "radius": 2.5 * mm});
            skCircle(sketch, "E1.90.1.0", {"center": v(495, -5.5) * mm, "radius": 2.5 * mm});
            skCircle(sketch, "E1.90.2.0", {"center": v(495, -11) * mm, "radius": 2.5 * mm});
            skCircle(sketch, "E1.90.3.0", {"center": v(495, -16.5) * mm, "radius": 2.5 * mm});
            skCircle(sketch, "E1.90.4.0", {"center": v(495, -22) * mm, "radius": 2.5 * mm});
            skCircle(sketch, "E1.90.5.0", {"center": v(495, -27.5) * mm, "radius": 2.5 * mm});
            skCircle(sketch, "E1.90.6.0", {"center": v(495, -33) * mm, "radius": 2.5 * mm});
            skCircle(sketch, "E1.90.7.0", {"center": v(495, -38.5) * mm, "radius": 2.5 * mm});
            skCircle(sketch, "E1.90.8.0", {"center": v(495, -44) * mm, "radius": 2.5 * mm});
            skCircle(sketch, "E1.90.9.0", {"center": v(495, -49.5) * mm, "radius": 2.5 * mm});
            skCircle(sketch, "E1.90.10.0", {"center": v(495, -55) * mm, "radius": 2.5 * mm});
            skCircle(sketch, "E1.90.11.0", {"center": v(495, -60.5) * mm, "radius": 2.5 * mm});
            skCircle(sketch, "E1.90.12.0", {"center": v(495, -66) * mm, "radius": 2.5 * mm});
            skCircle(sketch, "E1.90.13.0", {"center": v(495, -71.5) * mm, "radius": 2.5 * mm});
            skCircle(sketch, "E1.90.14.0", {"center": v(495, -77) * mm, "radius": 2.5 * mm});
            skCircle(sketch, "E1.90.15.0", {"center": v(495, -82.5) * mm, "radius": 2.5 * mm});
            skCircle(sketch, "E1.90.16.0", {"center": v(495, -88) * mm, "radius": 2.5 * mm});
            skCircle(sketch, "E1.90.17.0", {"center": v(495, -93.5) * mm, "radius": 2.5 * mm});
            skCircle(sketch, "E1.90.18.0", {"center": v(495, -99) * mm, "radius": 2.5 * mm});
            skCircle(sketch, "E1.90.19.0", {"center": v(495, -104.5) * mm, "radius": 2.5 * mm});
            skCircle(sketch, "E1.90.20.0", {"center": v(495, -110) * mm, "radius": 2.5 * mm});
            skCircle(sketch, "E1.90.21.0", {"center": v(495, -115.5) * mm, "radius": 2.5 * mm});
            skCircle(sketch, "E1.90.22.0", {"center": v(495, -121) * mm, "radius": 2.5 * mm});
            skCircle(sketch, "E1.90.23.0", {"center": v(495, -126.5) * mm, "radius": 2.5 * mm});
            skCircle(sketch, "E1.90.24.0", {"center": v(495, -132) * mm, "radius": 2.5 * mm});
            skCircle(sketch, "E1.91.0.0", {"center": v(500.5, 0) * mm, "radius": 2.5 * mm});
            skCircle(sketch, "E1.91.1.0", {"center": v(500.5, -5.5) * mm, "radius": 2.5 * mm});
            skCircle(sketch, "E1.91.2.0", {"center": v(500.5, -11) * mm, "radius": 2.5 * mm});
            skCircle(sketch, "E1.91.3.0", {"center": v(500.5, -16.5) * mm, "radius": 2.5 * mm});
            skCircle(sketch, "E1.91.4.0", {"center": v(500.5, -22) * mm, "radius": 2.5 * mm});
            skCircle(sketch, "E1.91.5.0", {"center": v(500.5, -27.5) * mm, "radius": 2.5 * mm});
            skCircle(sketch, "E1.91.6.0", {"center": v(500.5, -33) * mm, "radius": 2.5 * mm});
            skCircle(sketch, "E1.91.7.0", {"center": v(500.5, -38.5) * mm, "radius": 2.5 * mm});
            skCircle(sketch, "E1.91.8.0", {"center": v(500.5, -44) * mm, "radius": 2.5 * mm});
            skCircle(sketch, "E1.91.9.0", {"center": v(500.5, -49.5) * mm, "radius": 2.5 * mm});
            skCircle(sketch, "E1.91.10.0", {"center": v(500.5, -55) * mm, "radius": 2.5 * mm});
            skCircle(sketch, "E1.91.11.0", {"center": v(500.5, -60.5) * mm, "radius": 2.5 * mm});
            skCircle(sketch, "E1.91.12.0", {"center": v(500.5, -66) * mm, "radius": 2.5 * mm});
            skCircle(sketch, "E1.91.13.0", {"center": v(500.5, -71.5) * mm, "radius": 2.5 * mm});
            skCircle(sketch, "E1.91.14.0", {"center": v(500.5, -77) * mm, "radius": 2.5 * mm});
            skCircle(sketch, "E1.91.15.0", {"center": v(500.5, -82.5) * mm, "radius": 2.5 * mm});
            skCircle(sketch, "E1.91.16.0", {"center": v(500.5, -88) * mm, "radius": 2.5 * mm});
            skCircle(sketch, "E1.91.17.0", {"center": v(500.5, -93.5) * mm, "radius": 2.5 * mm});
            skCircle(sketch, "E1.91.18.0", {"center": v(500.5, -99) * mm, "radius": 2.5 * mm});
            skCircle(sketch, "E1.91.19.0", {"center": v(500.5, -104.5) * mm, "radius": 2.5 * mm});
            skCircle(sketch, "E1.91.20.0", {"center": v(500.5, -110) * mm, "radius": 2.5 * mm});
            skCircle(sketch, "E1.91.21.0", {"center": v(500.5, -115.5) * mm, "radius": 2.5 * mm});
            skCircle(sketch, "E1.91.22.0", {"center": v(500.5, -121) * mm, "radius": 2.5 * mm});
            skCircle(sketch, "E1.91.23.0", {"center": v(500.5, -126.5) * mm, "radius": 2.5 * mm});
            skCircle(sketch, "E1.91.24.0", {"center": v(500.5, -132) * mm, "radius": 2.5 * mm});
            skCircle(sketch, "E1.92.0.0", {"center": v(506, 0) * mm, "radius": 2.5 * mm});
            skCircle(sketch, "E1.92.1.0", {"center": v(506, -5.5) * mm, "radius": 2.5 * mm});
            skCircle(sketch, "E1.92.2.0", {"center": v(506, -11) * mm, "radius": 2.5 * mm});
            skCircle(sketch, "E1.92.3.0", {"center": v(506, -16.5) * mm, "radius": 2.5 * mm});
            skCircle(sketch, "E1.92.4.0", {"center": v(506, -22) * mm, "radius": 2.5 * mm});
            skCircle(sketch, "E1.92.5.0", {"center": v(506, -27.5) * mm, "radius": 2.5 * mm});
            skCircle(sketch, "E1.92.6.0", {"center": v(506, -33) * mm, "radius": 2.5 * mm});
            skCircle(sketch, "E1.92.7.0", {"center": v(506, -38.5) * mm, "radius": 2.5 * mm});
            skCircle(sketch, "E1.92.8.0", {"center": v(506, -44) * mm, "radius": 2.5 * mm});
            skCircle(sketch, "E1.92.9.0", {"center": v(506, -49.5) * mm, "radius": 2.5 * mm});
            skCircle(sketch, "E1.92.10.0", {"center": v(506, -55) * mm, "radius": 2.5 * mm});
            skCircle(sketch, "E1.92.11.0", {"center": v(506, -60.5) * mm, "radius": 2.5 * mm});
            skCircle(sketch, "E1.92.12.0", {"center": v(506, -66) * mm, "radius": 2.5 * mm});
            skCircle(sketch, "E1.92.13.0", {"center": v(506, -71.5) * mm, "radius": 2.5 * mm});
            skCircle(sketch, "E1.92.14.0", {"center": v(506, -77) * mm, "radius": 2.5 * mm});
            skCircle(sketch, "E1.92.15.0", {"center": v(506, -82.5) * mm, "radius": 2.5 * mm});
            skCircle(sketch, "E1.92.16.0", {"center": v(506, -88) * mm, "radius": 2.5 * mm});
            skCircle(sketch, "E1.92.17.0", {"center": v(506, -93.5) * mm, "radius": 2.5 * mm});
            skCircle(sketch, "E1.92.18.0", {"center": v(506, -99) * mm, "radius": 2.5 * mm});
            skCircle(sketch, "E1.92.19.0", {"center": v(506, -104.5) * mm, "radius": 2.5 * mm});
            skCircle(sketch, "E1.92.20.0", {"center": v(506, -110) * mm, "radius": 2.5 * mm});
            skCircle(sketch, "E1.92.21.0", {"center": v(506, -115.5) * mm, "radius": 2.5 * mm});
            skCircle(sketch, "E1.92.22.0", {"center": v(506, -121) * mm, "radius": 2.5 * mm});
            skCircle(sketch, "E1.92.23.0", {"center": v(506, -126.5) * mm, "radius": 2.5 * mm});
            skCircle(sketch, "E1.92.24.0", {"center": v(506, -132) * mm, "radius": 2.5 * mm});
            skCircle(sketch, "E1.93.0.0", {"center": v(511.5, 0) * mm, "radius": 2.5 * mm});
            skCircle(sketch, "E1.93.1.0", {"center": v(511.5, -5.5) * mm, "radius": 2.5 * mm});
            skCircle(sketch, "E1.93.2.0", {"center": v(511.5, -11) * mm, "radius": 2.5 * mm});
            skCircle(sketch, "E1.93.3.0", {"center": v(511.5, -16.5) * mm, "radius": 2.5 * mm});
            skCircle(sketch, "E1.93.4.0", {"center": v(511.5, -22) * mm, "radius": 2.5 * mm});
            skCircle(sketch, "E1.93.5.0", {"center": v(511.5, -27.5) * mm, "radius": 2.5 * mm});
            skCircle(sketch, "E1.93.6.0", {"center": v(511.5, -33) * mm, "radius": 2.5 * mm});
            skCircle(sketch, "E1.93.7.0", {"center": v(511.5, -38.5) * mm, "radius": 2.5 * mm});
            skCircle(sketch, "E1.93.8.0", {"center": v(511.5, -44) * mm, "radius": 2.5 * mm});
            skCircle(sketch, "E1.93.9.0", {"center": v(511.5, -49.5) * mm, "radius": 2.5 * mm});
            skCircle(sketch, "E1.93.10.0", {"center": v(511.5, -55) * mm, "radius": 2.5 * mm});
            skCircle(sketch, "E1.93.11.0", {"center": v(511.5, -60.5) * mm, "radius": 2.5 * mm});
            skCircle(sketch, "E1.93.12.0", {"center": v(511.5, -66) * mm, "radius": 2.5 * mm});
            skCircle(sketch, "E1.93.13.0", {"center": v(511.5, -71.5) * mm, "radius": 2.5 * mm});
            skCircle(sketch, "E1.93.14.0", {"center": v(511.5, -77) * mm, "radius": 2.5 * mm});
            skCircle(sketch, "E1.93.15.0", {"center": v(511.5, -82.5) * mm, "radius": 2.5 * mm});
            skCircle(sketch, "E1.93.16.0", {"center": v(511.5, -88) * mm, "radius": 2.5 * mm});
            skCircle(sketch, "E1.93.17.0", {"center": v(511.5, -93.5) * mm, "radius": 2.5 * mm});
            skCircle(sketch, "E1.93.18.0", {"center": v(511.5, -99) * mm, "radius": 2.5 * mm});
            skCircle(sketch, "E1.93.19.0", {"center": v(511.5, -104.5) * mm, "radius": 2.5 * mm});
            skCircle(sketch, "E1.93.20.0", {"center": v(511.5, -110) * mm, "radius": 2.5 * mm});
            skCircle(sketch, "E1.93.21.0", {"center": v(511.5, -115.5) * mm, "radius": 2.5 * mm});
            skCircle(sketch, "E1.93.22.0", {"center": v(511.5, -121) * mm, "radius": 2.5 * mm});
            skCircle(sketch, "E1.93.23.0", {"center": v(511.5, -126.5) * mm, "radius": 2.5 * mm});
            skCircle(sketch, "E1.93.24.0", {"center": v(511.5, -132) * mm, "radius": 2.5 * mm});
            skCircle(sketch, "E1.94.0.0", {"center": v(517, 0) * mm, "radius": 2.5 * mm});
            skCircle(sketch, "E1.94.1.0", {"center": v(517, -5.5) * mm, "radius": 2.5 * mm});
            skCircle(sketch, "E1.94.2.0", {"center": v(517, -11) * mm, "radius": 2.5 * mm});
            skCircle(sketch, "E1.94.3.0", {"center": v(517, -16.5) * mm, "radius": 2.5 * mm});
            skCircle(sketch, "E1.94.4.0", {"center": v(517, -22) * mm, "radius": 2.5 * mm});
            skCircle(sketch, "E1.94.5.0", {"center": v(517, -27.5) * mm, "radius": 2.5 * mm});
            skCircle(sketch, "E1.94.6.0", {"center": v(517, -33) * mm, "radius": 2.5 * mm});
            skCircle(sketch, "E1.94.7.0", {"center": v(517, -38.5) * mm, "radius": 2.5 * mm});
            skCircle(sketch, "E1.94.8.0", {"center": v(517, -44) * mm, "radius": 2.5 * mm});
            skCircle(sketch, "E1.94.9.0", {"center": v(517, -49.5) * mm, "radius": 2.5 * mm});
            skCircle(sketch, "E1.94.10.0", {"center": v(517, -55) * mm, "radius": 2.5 * mm});
            skCircle(sketch, "E1.94.11.0", {"center": v(517, -60.5) * mm, "radius": 2.5 * mm});
            skCircle(sketch, "E1.94.12.0", {"center": v(517, -66) * mm, "radius": 2.5 * mm});
            skCircle(sketch, "E1.94.13.0", {"center": v(517, -71.5) * mm, "radius": 2.5 * mm});
            skCircle(sketch, "E1.94.14.0", {"center": v(517, -77) * mm, "radius": 2.5 * mm});
            skCircle(sketch, "E1.94.15.0", {"center": v(517, -82.5) * mm, "radius": 2.5 * mm});
            skCircle(sketch, "E1.94.16.0", {"center": v(517, -88) * mm, "radius": 2.5 * mm});
            skCircle(sketch, "E1.94.17.0", {"center": v(517, -93.5) * mm, "radius": 2.5 * mm});
            skCircle(sketch, "E1.94.18.0", {"center": v(517, -99) * mm, "radius": 2.5 * mm});
            skCircle(sketch, "E1.94.19.0", {"center": v(517, -104.5) * mm, "radius": 2.5 * mm});
            skCircle(sketch, "E1.94.20.0", {"center": v(517, -110) * mm, "radius": 2.5 * mm});
            skCircle(sketch, "E1.94.21.0", {"center": v(517, -115.5) * mm, "radius": 2.5 * mm});
            skCircle(sketch, "E1.94.22.0", {"center": v(517, -121) * mm, "radius": 2.5 * mm});
            skCircle(sketch, "E1.94.23.0", {"center": v(517, -126.5) * mm, "radius": 2.5 * mm});
            skCircle(sketch, "E1.94.24.0", {"center": v(517, -132) * mm, "radius": 2.5 * mm});
            skCircle(sketch, "E1.95.0.0", {"center": v(522.5, 0) * mm, "radius": 2.5 * mm});
            skCircle(sketch, "E1.95.1.0", {"center": v(522.5, -5.5) * mm, "radius": 2.5 * mm});
            skCircle(sketch, "E1.95.2.0", {"center": v(522.5, -11) * mm, "radius": 2.5 * mm});
            skCircle(sketch, "E1.95.3.0", {"center": v(522.5, -16.5) * mm, "radius": 2.5 * mm});
            skCircle(sketch, "E1.95.4.0", {"center": v(522.5, -22) * mm, "radius": 2.5 * mm});
            skCircle(sketch, "E1.95.5.0", {"center": v(522.5, -27.5) * mm, "radius": 2.5 * mm});
            skCircle(sketch, "E1.95.6.0", {"center": v(522.5, -33) * mm, "radius": 2.5 * mm});
            skCircle(sketch, "E1.95.7.0", {"center": v(522.5, -38.5) * mm, "radius": 2.5 * mm});
            skCircle(sketch, "E1.95.8.0", {"center": v(522.5, -44) * mm, "radius": 2.5 * mm});
            skCircle(sketch, "E1.95.9.0", {"center": v(522.5, -49.5) * mm, "radius": 2.5 * mm});
            skCircle(sketch, "E1.95.10.0", {"center": v(522.5, -55) * mm, "radius": 2.5 * mm});
            skCircle(sketch, "E1.95.11.0", {"center": v(522.5, -60.5) * mm, "radius": 2.5 * mm});
            skCircle(sketch, "E1.95.12.0", {"center": v(522.5, -66) * mm, "radius": 2.5 * mm});
            skCircle(sketch, "E1.95.13.0", {"center": v(522.5, -71.5) * mm, "radius": 2.5 * mm});
            skCircle(sketch, "E1.95.14.0", {"center": v(522.5, -77) * mm, "radius": 2.5 * mm});
            skCircle(sketch, "E1.95.15.0", {"center": v(522.5, -82.5) * mm, "radius": 2.5 * mm});
            skCircle(sketch, "E1.95.16.0", {"center": v(522.5, -88) * mm, "radius": 2.5 * mm});
            skCircle(sketch, "E1.95.17.0", {"center": v(522.5, -93.5) * mm, "radius": 2.5 * mm});
            skCircle(sketch, "E1.95.18.0", {"center": v(522.5, -99) * mm, "radius": 2.5 * mm});
            skCircle(sketch, "E1.95.19.0", {"center": v(522.5, -104.5) * mm, "radius": 2.5 * mm});
            skCircle(sketch, "E1.95.20.0", {"center": v(522.5, -110) * mm, "radius": 2.5 * mm});
            skCircle(sketch, "E1.95.21.0", {"center": v(522.5, -115.5) * mm, "radius": 2.5 * mm});
            skCircle(sketch, "E1.95.22.0", {"center": v(522.5, -121) * mm, "radius": 2.5 * mm});
            skCircle(sketch, "E1.95.23.0", {"center": v(522.5, -126.5) * mm, "radius": 2.5 * mm});
            skCircle(sketch, "E1.95.24.0", {"center": v(522.5, -132) * mm, "radius": 2.5 * mm});
            skCircle(sketch, "E1.96.0.0", {"center": v(528, 0) * mm, "radius": 2.5 * mm});
            skCircle(sketch, "E1.96.1.0", {"center": v(528, -5.5) * mm, "radius": 2.5 * mm});
            skCircle(sketch, "E1.96.2.0", {"center": v(528, -11) * mm, "radius": 2.5 * mm});
            skCircle(sketch, "E1.96.3.0", {"center": v(528, -16.5) * mm, "radius": 2.5 * mm});
            skCircle(sketch, "E1.96.4.0", {"center": v(528, -22) * mm, "radius": 2.5 * mm});
            skCircle(sketch, "E1.96.5.0", {"center": v(528, -27.5) * mm, "radius": 2.5 * mm});
            skCircle(sketch, "E1.96.6.0", {"center": v(528, -33) * mm, "radius": 2.5 * mm});
            skCircle(sketch, "E1.96.7.0", {"center": v(528, -38.5) * mm, "radius": 2.5 * mm});
            skCircle(sketch, "E1.96.8.0", {"center": v(528, -44) * mm, "radius": 2.5 * mm});
            skCircle(sketch, "E1.96.9.0", {"center": v(528, -49.5) * mm, "radius": 2.5 * mm});
            skCircle(sketch, "E1.96.10.0", {"center": v(528, -55) * mm, "radius": 2.5 * mm});
            skCircle(sketch, "E1.96.11.0", {"center": v(528, -60.5) * mm, "radius": 2.5 * mm});
            skCircle(sketch, "E1.96.12.0", {"center": v(528, -66) * mm, "radius": 2.5 * mm});
            skCircle(sketch, "E1.96.13.0", {"center": v(528, -71.5) * mm, "radius": 2.5 * mm});
            skCircle(sketch, "E1.96.14.0", {"center": v(528, -77) * mm, "radius": 2.5 * mm});
            skCircle(sketch, "E1.96.15.0", {"center": v(528, -82.5) * mm, "radius": 2.5 * mm});
            skCircle(sketch, "E1.96.16.0", {"center": v(528, -88) * mm, "radius": 2.5 * mm});
            skCircle(sketch, "E1.96.17.0", {"center": v(528, -93.5) * mm, "radius": 2.5 * mm});
            skCircle(sketch, "E1.96.18.0", {"center": v(528, -99) * mm, "radius": 2.5 * mm});
            skCircle(sketch, "E1.96.19.0", {"center": v(528, -104.5) * mm, "radius": 2.5 * mm});
            skCircle(sketch, "E1.96.20.0", {"center": v(528, -110) * mm, "radius": 2.5 * mm});
            skCircle(sketch, "E1.96.21.0", {"center": v(528, -115.5) * mm, "radius": 2.5 * mm});
            skCircle(sketch, "E1.96.22.0", {"center": v(528, -121) * mm, "radius": 2.5 * mm});
            skCircle(sketch, "E1.96.23.0", {"center": v(528, -126.5) * mm, "radius": 2.5 * mm});
            skCircle(sketch, "E1.96.24.0", {"center": v(528, -132) * mm, "radius": 2.5 * mm});
            skCircle(sketch, "E1.97.0.0", {"center": v(533.5, 0) * mm, "radius": 2.5 * mm});
            skCircle(sketch, "E1.97.1.0", {"center": v(533.5, -5.5) * mm, "radius": 2.5 * mm});
            skCircle(sketch, "E1.97.2.0", {"center": v(533.5, -11) * mm, "radius": 2.5 * mm});
            skCircle(sketch, "E1.97.3.0", {"center": v(533.5, -16.5) * mm, "radius": 2.5 * mm});
            skCircle(sketch, "E1.97.4.0", {"center": v(533.5, -22) * mm, "radius": 2.5 * mm});
            skCircle(sketch, "E1.97.5.0", {"center": v(533.5, -27.5) * mm, "radius": 2.5 * mm});
            skCircle(sketch, "E1.97.6.0", {"center": v(533.5, -33) * mm, "radius": 2.5 * mm});
            skCircle(sketch, "E1.97.7.0", {"center": v(533.5, -38.5) * mm, "radius": 2.5 * mm});
            skCircle(sketch, "E1.97.8.0", {"center": v(533.5, -44) * mm, "radius": 2.5 * mm});
            skCircle(sketch, "E1.97.9.0", {"center": v(533.5, -49.5) * mm, "radius": 2.5 * mm});
            skCircle(sketch, "E1.97.10.0", {"center": v(533.5, -55) * mm, "radius": 2.5 * mm});
            skCircle(sketch, "E1.97.11.0", {"center": v(533.5, -60.5) * mm, "radius": 2.5 * mm});
            skCircle(sketch, "E1.97.12.0", {"center": v(533.5, -66) * mm, "radius": 2.5 * mm});
            skCircle(sketch, "E1.97.13.0", {"center": v(533.5, -71.5) * mm, "radius": 2.5 * mm});
            skCircle(sketch, "E1.97.14.0", {"center": v(533.5, -77) * mm, "radius": 2.5 * mm});
            skCircle(sketch, "E1.97.15.0", {"center": v(533.5, -82.5) * mm, "radius": 2.5 * mm});
            skCircle(sketch, "E1.97.16.0", {"center": v(533.5, -88) * mm, "radius": 2.5 * mm});
            skCircle(sketch, "E1.97.17.0", {"center": v(533.5, -93.5) * mm, "radius": 2.5 * mm});
            skCircle(sketch, "E1.97.18.0", {"center": v(533.5, -99) * mm, "radius": 2.5 * mm});
            skCircle(sketch, "E1.97.19.0", {"center": v(533.5, -104.5) * mm, "radius": 2.5 * mm});
            skCircle(sketch, "E1.97.20.0", {"center": v(533.5, -110) * mm, "radius": 2.5 * mm});
            skCircle(sketch, "E1.97.21.0", {"center": v(533.5, -115.5) * mm, "radius": 2.5 * mm});
            skCircle(sketch, "E1.97.22.0", {"center": v(533.5, -121) * mm, "radius": 2.5 * mm});
            skCircle(sketch, "E1.97.23.0", {"center": v(533.5, -126.5) * mm, "radius": 2.5 * mm});
            skCircle(sketch, "E1.97.24.0", {"center": v(533.5, -132) * mm, "radius": 2.5 * mm});
            skCircle(sketch, "E1.98.0.0", {"center": v(539, 0) * mm, "radius": 2.5 * mm});
            skCircle(sketch, "E1.98.1.0", {"center": v(539, -5.5) * mm, "radius": 2.5 * mm});
            skCircle(sketch, "E1.98.2.0", {"center": v(539, -11) * mm, "radius": 2.5 * mm});
            skCircle(sketch, "E1.98.3.0", {"center": v(539, -16.5) * mm, "radius": 2.5 * mm});
            skCircle(sketch, "E1.98.4.0", {"center": v(539, -22) * mm, "radius": 2.5 * mm});
            skCircle(sketch, "E1.98.5.0", {"center": v(539, -27.5) * mm, "radius": 2.5 * mm});
            skCircle(sketch, "E1.98.6.0", {"center": v(539, -33) * mm, "radius": 2.5 * mm});
            skCircle(sketch, "E1.98.7.0", {"center": v(539, -38.5) * mm, "radius": 2.5 * mm});
            skCircle(sketch, "E1.98.8.0", {"center": v(539, -44) * mm, "radius": 2.5 * mm});
            skCircle(sketch, "E1.98.9.0", {"center": v(539, -49.5) * mm, "radius": 2.5 * mm});
            skCircle(sketch, "E1.98.10.0", {"center": v(539, -55) * mm, "radius": 2.5 * mm});
            skCircle(sketch, "E1.98.11.0", {"center": v(539, -60.5) * mm, "radius": 2.5 * mm});
            skCircle(sketch, "E1.98.12.0", {"center": v(539, -66) * mm, "radius": 2.5 * mm});
            skCircle(sketch, "E1.98.13.0", {"center": v(539, -71.5) * mm, "radius": 2.5 * mm});
            skCircle(sketch, "E1.98.14.0", {"center": v(539, -77) * mm, "radius": 2.5 * mm});
            skCircle(sketch, "E1.98.15.0", {"center": v(539, -82.5) * mm, "radius": 2.5 * mm});
            skCircle(sketch, "E1.98.16.0", {"center": v(539, -88) * mm, "radius": 2.5 * mm});
            skCircle(sketch, "E1.98.17.0", {"center": v(539, -93.5) * mm, "radius": 2.5 * mm});
            skCircle(sketch, "E1.98.18.0", {"center": v(539, -99) * mm, "radius": 2.5 * mm});
            skCircle(sketch, "E1.98.19.0", {"center": v(539, -104.5) * mm, "radius": 2.5 * mm});
            skCircle(sketch, "E1.98.20.0", {"center": v(539, -110) * mm, "radius": 2.5 * mm});
            skCircle(sketch, "E1.98.21.0", {"center": v(539, -115.5) * mm, "radius": 2.5 * mm});
            skCircle(sketch, "E1.98.22.0", {"center": v(539, -121) * mm, "radius": 2.5 * mm});
            skCircle(sketch, "E1.98.23.0", {"center": v(539, -126.5) * mm, "radius": 2.5 * mm});
            skCircle(sketch, "E1.98.24.0", {"center": v(539, -132) * mm, "radius": 2.5 * mm});
            skCircle(sketch, "E1.99.0.0", {"center": v(544.5, 0) * mm, "radius": 2.5 * mm});
            skCircle(sketch, "E1.99.1.0", {"center": v(544.5, -5.5) * mm, "radius": 2.5 * mm});
            skCircle(sketch, "E1.99.2.0", {"center": v(544.5, -11) * mm, "radius": 2.5 * mm});
            skCircle(sketch, "E1.99.3.0", {"center": v(544.5, -16.5) * mm, "radius": 2.5 * mm});
            skCircle(sketch, "E1.99.4.0", {"center": v(544.5, -22) * mm, "radius": 2.5 * mm});
            skCircle(sketch, "E1.99.5.0", {"center": v(544.5, -27.5) * mm, "radius": 2.5 * mm});
            skCircle(sketch, "E1.99.6.0", {"center": v(544.5, -33) * mm, "radius": 2.5 * mm});
            skCircle(sketch, "E1.99.7.0", {"center": v(544.5, -38.5) * mm, "radius": 2.5 * mm});
            skCircle(sketch, "E1.99.8.0", {"center": v(544.5, -44) * mm, "radius": 2.5 * mm});
            skCircle(sketch, "E1.99.9.0", {"center": v(544.5, -49.5) * mm, "radius": 2.5 * mm});
            skCircle(sketch, "E1.99.10.0", {"center": v(544.5, -55) * mm, "radius": 2.5 * mm});
            skCircle(sketch, "E1.99.11.0", {"center": v(544.5, -60.5) * mm, "radius": 2.5 * mm});
            skCircle(sketch, "E1.99.12.0", {"center": v(544.5, -66) * mm, "radius": 2.5 * mm});
            skCircle(sketch, "E1.99.13.0", {"center": v(544.5, -71.5) * mm, "radius": 2.5 * mm});
            skCircle(sketch, "E1.99.14.0", {"center": v(544.5, -77) * mm, "radius": 2.5 * mm});
            skCircle(sketch, "E1.99.15.0", {"center": v(544.5, -82.5) * mm, "radius": 2.5 * mm});
            skCircle(sketch, "E1.99.16.0", {"center": v(544.5, -88) * mm, "radius": 2.5 * mm});
            skCircle(sketch, "E1.99.17.0", {"center": v(544.5, -93.5) * mm, "radius": 2.5 * mm});
            skCircle(sketch, "E1.99.18.0", {"center": v(544.5, -99) * mm, "radius": 2.5 * mm});
            skCircle(sketch, "E1.99.19.0", {"center": v(544.5, -104.5) * mm, "radius": 2.5 * mm});
            skCircle(sketch, "E1.99.20.0", {"center": v(544.5, -110) * mm, "radius": 2.5 * mm});
            skCircle(sketch, "E1.99.21.0", {"center": v(544.5, -115.5) * mm, "radius": 2.5 * mm});
            skCircle(sketch, "E1.99.22.0", {"center": v(544.5, -121) * mm, "radius": 2.5 * mm});
            skCircle(sketch, "E1.99.23.0", {"center": v(544.5, -126.5) * mm, "radius": 2.5 * mm});
            skCircle(sketch, "E1.99.24.0", {"center": v(544.5, -132) * mm, "radius": 2.5 * mm});
            skLineSegment(sketch, "E1.direction1", {"start": v(0, 0) * mm, "end": v(5.5, 0) * mm, "construction": true});
            skLineSegment(sketch, "E1.direction2", {"start": v(0, 0) * mm, "end": v(0, -5.5) * mm, "construction": true});
            skSolve(sketch);
        }
        {
            var Q0;
            Q0 = qSketchRegion(id + "F0", true);
            extrude(context, id + "F1", {"entities" : qUnion([Q0]), "depth" : 25 * mm});
        }
    });
